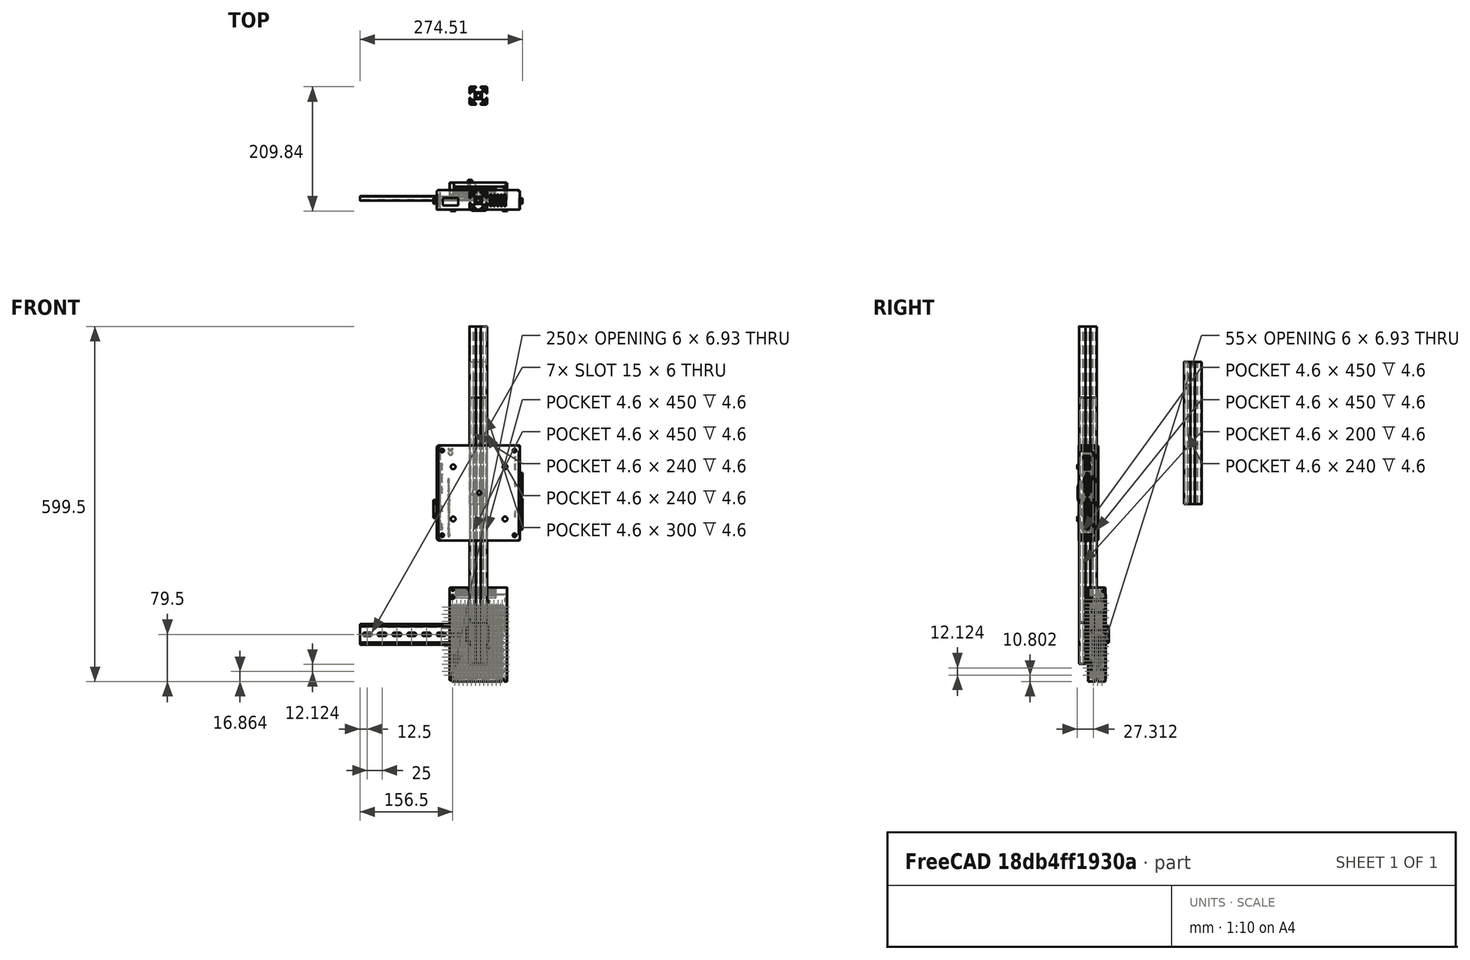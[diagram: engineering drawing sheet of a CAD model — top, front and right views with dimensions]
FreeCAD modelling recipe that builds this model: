
FCSTD DOCUMENT  (FreeCAD 1.0R39319 (Git))
Label: electronics-box
License: All rights reserved
objects: App::Link×40, App::FeaturePython×40, Part::Feature×11, App::Part×1, Assembly::JointGroup×1, Assembly::AssemblyObject×1
note: 11 computed .brp shape members not serialized (recipe doc carries the construction recipe); baked Part::Feature solids carry a one-line shape summary decoded from their .brp
EXTERNAL_REF file=din_mount.FCStd obj=Part
EXTERNAL_REF file=power-supply-bracket.FCStd obj=Part
EXTERNAL_REF file=dlp-power-supply-bracket.FCStd obj=Part
EXTERNAL_REF file=smc100c-bracket.FCStd obj=Part
EXTERNAL_REF file=ports-panel.FCStd obj=Part

FEATURE [Part::Feature] Part__Feature  label="alu-prof-3030-200-000"
  shape: bbox 30 x 30 x 200 mm, 122 faces (baked)
FEATURE [Part::Feature] Part__Feature001  label="alu-prof-3030-300-000"
  shape: bbox 30 x 30 x 300 mm, 122 faces (baked)
FEATURE [Part::Feature] Part__Feature002  label="alu-prof-3030-450-000"
  shape: bbox 30 x 30 x 450 mm, 122 faces (baked)
FEATURE [App::Link] alu_prof_3030_300_000  label="alu-prof-3030-300-001"
  LinkedObject = -> Part__Feature001
FEATURE [App::Link] alu_prof_3030_450_000  label="alu-prof-3030-450-001"
  LinkPlacement = pos=(415,-2.4e-15,235) rot=(0,-1,0;1.5708rad)
  LinkedObject = -> Part__Feature002
  Placement = pos=(415,-2.4e-15,235) rot=(0,-1,0;1.5708rad)
FEATURE [App::FeaturePython] GroundedJoint  # Assembly grounded joint (typed FeaturePython)
  ObjectToGround = -> alu_prof_3030_300_000
FEATURE [App::FeaturePython] Joint  label="Fixed"  # Assembly joint (typed FeaturePython)
  Activated = true
  AngleMax = 0
  AngleMin = 0
  Detach1 = false
  Detach2 = false
  Distance = 0
  Distance2 = 0
  EnableAngleMax = false
  EnableAngleMin = false
  EnableLengthMax = false
  EnableLengthMin = false
  JointType = 0 (Fixed)
  LengthMax = 0
  LengthMin = 0
  Offset2 = pos=(0,0,0) rot=(0,0,-1;1.5708rad)
  Placement1 = pos=(-15,-8.7,400) rot=(0.57735,0.57735,0.57735;4.18879rad)
  Placement2 = pos=(15,-8.7,220) rot=(0,0.707107,0.707107;3.14159rad)
  Reference1 = -> Assembly [alu_prof_3030_450_000.Edge78,alu_prof_3030_450_000.Edge78]
  Reference2 = -> Assembly [alu_prof_3030_300_000.Edge7,alu_prof_3030_300_000.Edge7]
FEATURE [App::Link] alu_prof_3030_300_001  label="alu-prof-3030-300-002"
  LinkPlacement = pos=(480,-1.166e-13,740) rot=(0,1,0;3.14159rad)
  LinkedObject = -> Part__Feature001
  Placement = pos=(480,-1.166e-13,740) rot=(0,1,0;3.14159rad)
FEATURE [App::Link] alu_prof_3030_200_000  label="alu-prof-3030-200-001"
  LinkPlacement = pos=(480,-235,505) rot=(1,0,0;4.71239rad)
  LinkedObject = -> Part__Feature
  Placement = pos=(480,-235,505) rot=(1,0,0;4.71239rad)
FEATURE [App::Link] alu_prof_3030_200_001  label="alu-prof-3030-200-002"
  LinkPlacement = pos=(9.88e-14,-235,505) rot=(-1,0,0;1.5708rad)
  LinkedObject = -> Part__Feature
  Placement = pos=(9.88e-14,-235,505) rot=(-1,0,0;1.5708rad)
FEATURE [App::Link] alu_prof_3030_200_002  label="alu-prof-3030-200-003"
  LinkPlacement = pos=(-9.59e-14,-235,235) rot=(1,0,0;4.71239rad)
  LinkedObject = -> Part__Feature
  Placement = pos=(-9.59e-14,-235,235) rot=(1,0,0;4.71239rad)
FEATURE [App::Link] alu_prof_3030_200_003  label="alu-prof-3030-200-004"
  LinkPlacement = pos=(480,-235,235) rot=(-1,0,0;1.5708rad)
  LinkedObject = -> Part__Feature
  Placement = pos=(480,-235,235) rot=(-1,0,0;1.5708rad)
FEATURE [App::FeaturePython] Joint001  label="Fixed001"  # Assembly joint (typed FeaturePython)
  Activated = true
  AngleMax = 0
  AngleMin = 0
  Detach1 = false
  Detach2 = false
  Distance = 0
  Distance2 = 0
  EnableAngleMax = false
  EnableAngleMin = false
  EnableLengthMax = false
  EnableLengthMin = false
  JointType = 0 (Fixed)
  LengthMax = 0
  LengthMin = 0
  Offset2 = pos=(0,0,0) rot=(0,0,-1;1.5708rad)
  Placement1 = pos=(15,-8.7,520) rot=(0.57735,0.57735,0.57735;4.18879rad)
  Placement2 = pos=(-15,-8.7,-50) rot=(0,-0.707107,0.707107;3.14159rad)
  Reference1 = -> Assembly [alu_prof_3030_300_001.Edge5,alu_prof_3030_300_001.Edge5]
  Reference2 = -> Assembly [alu_prof_3030_450_000.Edge153,alu_prof_3030_450_000.Edge153]
FEATURE [App::FeaturePython] Joint002  label="Fixed002"  # Assembly joint (typed FeaturePython)
  Activated = true
  AngleMax = 0
  AngleMin = 0
  Detach1 = false
  Detach2 = false
  Distance = 0
  Distance2 = 0
  EnableAngleMax = false
  EnableAngleMin = false
  EnableLengthMax = false
  EnableLengthMin = false
  JointType = 0 (Fixed)
  LengthMax = 0
  LengthMin = 0
  Offset2 = pos=(0,0,0) rot=(0,0,1;1.5708rad)
  Placement1 = pos=(-8.7,15,220) rot=(-0.707107,0,0.707107;3.14159rad)
  Placement2 = pos=(-8.7,-15,220) rot=(0.57735,-0.57735,0.57735;4.18879rad)
  Reference1 = -> Assembly [alu_prof_3030_200_002.Edge133,alu_prof_3030_200_002.Edge133]
  Reference2 = -> Assembly [alu_prof_3030_300_000.Edge205,alu_prof_3030_300_000.Edge205]
FEATURE [App::FeaturePython] Joint003  label="Fixed003"  # Assembly joint (typed FeaturePython)
  Activated = true
  AngleMax = 0
  AngleMin = 0
  Detach1 = false
  Detach2 = false
  Distance = 0
  Distance2 = 0
  EnableAngleMax = false
  EnableAngleMin = false
  EnableLengthMax = false
  EnableLengthMin = false
  JointType = 0 (Fixed)
  LengthMax = 0
  LengthMin = 0
  Offset2 = pos=(0,0,0) rot=(0,0,1;1.5708rad)
  Placement1 = pos=(-8.7,15,220) rot=(-0.707107,0,0.707107;3.14159rad)
  Placement2 = pos=(8.7,-15,520) rot=(0.57735,-0.57735,0.57735;4.18879rad)
  Reference1 = -> Assembly [alu_prof_3030_200_003.Edge133,alu_prof_3030_200_003.Edge133]
  Reference2 = -> Assembly [alu_prof_3030_300_001.Edge263,alu_prof_3030_300_001.Edge263]
FEATURE [App::FeaturePython] Joint004  label="Fixed004"  # Assembly joint (typed FeaturePython)
  Activated = true
  AngleMax = 0
  AngleMin = 0
  Detach1 = false
  Detach2 = false
  Distance = 0
  Distance2 = 0
  EnableAngleMax = false
  EnableAngleMin = false
  EnableLengthMax = false
  EnableLengthMin = false
  JointType = 0 (Fixed)
  LengthMax = 0
  LengthMin = 0
  Offset2 = pos=(0,0,0) rot=(0,0,-1;1.5708rad)
  Placement1 = pos=(-8.7,-15,220) rot=(0.707107,0,0.707107;3.14159rad)
  Placement2 = pos=(-8.7,-15,520) rot=(0.57735,0.57735,0.57735;2.0944rad)
  Reference1 = -> Assembly [alu_prof_3030_200_001.Edge205,alu_prof_3030_200_001.Edge205]
  Reference2 = -> Assembly [alu_prof_3030_300_000.Edge203,alu_prof_3030_300_000.Edge203]
FEATURE [App::FeaturePython] Joint005  label="Fixed005"  # Assembly joint (typed FeaturePython)
  Activated = true
  AngleMax = 0
  AngleMin = 0
  Detach1 = false
  Detach2 = false
  Distance = 0
  Distance2 = 0
  EnableAngleMax = false
  EnableAngleMin = false
  EnableLengthMax = false
  EnableLengthMin = false
  JointType = 0 (Fixed)
  LengthMax = 0
  LengthMin = 0
  Offset2 = pos=(0,0,0) rot=(0,0,-1;1.5708rad)
  Placement1 = pos=(-8.7,-15,220) rot=(0.707107,0,0.707107;3.14159rad)
  Placement2 = pos=(8.7,-15,220) rot=(0.57735,0.57735,0.57735;2.0944rad)
  Reference1 = -> Assembly [alu_prof_3030_200_000.Edge205,alu_prof_3030_200_000.Edge205]
  Reference2 = -> Assembly [alu_prof_3030_300_001.Edge264,alu_prof_3030_300_001.Edge264]
FEATURE [App::Link] alu_prof_3030_450_003  label="alu-prof-3030-450-004"
  LinkPlacement = pos=(415,-2e-15,505) rot=(0,1,0;4.71239rad)
  LinkedObject = -> Part__Feature002
  Placement = pos=(415,-2e-15,505) rot=(0,1,0;4.71239rad)
FEATURE [App::FeaturePython] Joint010  label="Fixed010"  # Assembly joint (typed FeaturePython)
  Activated = true
  AngleMax = 0
  AngleMin = 0
  Detach1 = false
  Detach2 = false
  Distance = 0
  Distance2 = 0
  EnableAngleMax = false
  EnableAngleMin = false
  EnableLengthMax = false
  EnableLengthMin = false
  JointType = 0 (Fixed)
  LengthMax = 0
  LengthMin = 0
  Offset2 = pos=(0,0,0) rot=(0,0,1;1.5708rad)
  Placement1 = pos=(15,-8.7,400) rot=(-0.57735,-0.57735,0.57735;4.18879rad)
  Placement2 = pos=(15,-8.7,520) rot=(1,0,0;4.71239rad)
  Reference1 = -> Assembly [alu_prof_3030_450_003.Edge14,alu_prof_3030_450_003.Edge14]
  Reference2 = -> Assembly [alu_prof_3030_300_000.Edge5,alu_prof_3030_300_000.Edge5]
FEATURE [Part::Feature] Part__Feature003  label="3030-angle-bracket-000"
  shape: bbox 36.72 x 36.72 x 28 mm, 72 faces (baked)
FEATURE [Part::Feature] Part__Feature004  label="SMC100CC"
  shape: bbox 150.5 x 35.5 x 163 mm, 2390 faces (baked)
FEATURE [Part::Feature] Part__Feature005  label="alu-prof-3030-240-000"
  Placement = pos=(0,177,0) rot=(0,0,1;0rad)
  shape: bbox 30 x 30 x 240 mm, 122 faces (baked)
FEATURE [App::Link] _030_angle_bracket_000  label="3030-angle-bracket-001"
  LinkPlacement = pos=(0.3,-197.5,250) rot=(-0.57735,-0.57735,-0.57735;4.18879rad)
  LinkedObject = -> Part__Feature003
  Placement = pos=(0.3,-197.5,250) rot=(-0.57735,-0.57735,-0.57735;4.18879rad)
FEATURE [App::Link] _030_angle_bracket_001  label="3030-angle-bracket-002"
  LinkPlacement = pos=(32.5,-15,505) rot=(1,0,0;3.14159rad)
  LinkedObject = -> Part__Feature003
  Placement = pos=(32.5,-15,505) rot=(1,0,0;3.14159rad)
FEATURE [App::Link] _030_angle_bracket_002  label="3030-angle-bracket-003"
  LinkPlacement = pos=(0.1,-15,267.5) rot=(0.707107,0,0.707107;3.14159rad)
  LinkedObject = -> Part__Feature003
  Placement = pos=(0.1,-15,267.5) rot=(0.707107,0,0.707107;3.14159rad)
FEATURE [App::Link] _030_angle_bracket_003  label="3030-angle-bracket-004"
  LinkPlacement = pos=(15,0.1,472.5) rot=(0.57735,0.57735,-0.57735;2.0944rad)
  LinkedObject = -> Part__Feature003
  Placement = pos=(15,0.1,472.5) rot=(0.57735,0.57735,-0.57735;2.0944rad)
FEATURE [App::Link] _030_angle_bracket_004  label="3030-angle-bracket-005"
  LinkPlacement = pos=(0.3,-215,472.5) rot=(0,-1,0;4.71239rad)
  LinkedObject = -> Part__Feature003
  Placement = pos=(0.3,-215,472.5) rot=(0,-1,0;4.71239rad)
FEATURE [App::Link] _030_angle_bracket_005  label="3030-angle-bracket-006"
  LinkPlacement = pos=(-0.3,-32.5,490) rot=(0.57735,-0.57735,0.57735;4.18879rad)
  LinkedObject = -> Part__Feature003
  Placement = pos=(-0.3,-32.5,490) rot=(0.57735,-0.57735,0.57735;4.18879rad)
FEATURE [App::FeaturePython] Joint013  label="Fixed013"  # Assembly joint (typed FeaturePython)
  Activated = true
  AngleMax = 0
  AngleMin = 0
  Detach1 = false
  Detach2 = false
  Distance = 0
  Distance2 = 0
  EnableAngleMax = false
  EnableAngleMin = false
  EnableLengthMax = false
  EnableLengthMin = false
  JointType = 0 (Fixed)
  LengthMax = 0
  LengthMin = 0
  Offset2 = pos=(0,0,13) rot=(0,0,1;1.5708rad)
  Placement1 = pos=(-17.5,0,0) rot=(0,0,1;0rad)
  Placement2 = pos=(15,0,220) rot=(1,0,0;4.71239rad)
  Reference1 = -> Assembly [_030_angle_bracket_001.Edge3,_030_angle_bracket_001.Edge3]
  Reference2 = -> Assembly [alu_prof_3030_200_001.Edge7,alu_prof_3030_200_001.Vertex4]
FEATURE [App::FeaturePython] Joint014  label="Fixed014"  # Assembly joint (typed FeaturePython)
  Activated = true
  AngleMax = 0
  AngleMin = 0
  Detach1 = false
  Detach2 = false
  Distance = 0
  Distance2 = 0
  EnableAngleMax = false
  EnableAngleMin = false
  EnableLengthMax = false
  EnableLengthMin = false
  JointType = 0 (Fixed)
  LengthMax = 0
  LengthMin = 0
  Offset2 = pos=(0,0,9) rot=(0,0,1;0rad)
  Placement1 = pos=(-17.5,0,3.4e-15) rot=(0,0,1;0rad)
  Placement2 = pos=(-0.3,15,220) rot=(-0.707107,0,0.707107;3.14159rad)
  Reference1 = -> Assembly [_030_angle_bracket_005.Edge3,_030_angle_bracket_005.Edge3]
  Reference2 = -> Assembly [alu_prof_3030_200_001.Edge73,alu_prof_3030_200_001.Edge73]
FEATURE [App::FeaturePython] Joint015  label="Fixed015"  # Assembly joint (typed FeaturePython)
  Activated = true
  AngleMax = 0
  AngleMin = 0
  Detach1 = false
  Detach2 = false
  Distance = 0
  Distance2 = 0
  EnableAngleMax = false
  EnableAngleMin = false
  EnableLengthMax = false
  EnableLengthMin = false
  JointType = 0 (Fixed)
  LengthMax = 0
  LengthMin = 0
  Offset2 = pos=(0,0,4.5) rot=(0,0,-1;1.5708rad)
  Placement1 = pos=(-17.5,1.8e-15,-3e-16) rot=(0,0,1;0rad)
  Placement2 = pos=(-15,0.1,400) rot=(0,0.707107,0.707107;3.14159rad)
  Reference1 = -> Assembly [_030_angle_bracket_003.Edge3,_030_angle_bracket_003.Edge3]
  Reference2 = -> Assembly [alu_prof_3030_450_003.Edge78,alu_prof_3030_450_003.Vertex78]
FEATURE [App::FeaturePython] Joint018  label="Fixed018"  # Assembly joint (typed FeaturePython)
  Activated = true
  AngleMax = 0
  AngleMin = 0
  Detach1 = false
  Detach2 = false
  Distance = 0
  Distance2 = 0
  EnableAngleMax = false
  EnableAngleMin = false
  EnableLengthMax = false
  EnableLengthMin = false
  JointType = 0 (Fixed)
  LengthMax = 0
  LengthMin = 0
  Offset2 = pos=(0,0,-4.5) rot=(0,0,-1;1.5708rad)
  Placement1 = pos=(-4.4,-15,220) rot=(0.707107,0,0.707107;3.14159rad)
  Placement2 = pos=(-17.5,0,-4.5) rot=(0,0,-1;1.5708rad)
  Reference1 = -> Assembly [alu_prof_3030_200_002.Edge205,alu_prof_3030_200_002.Vertex138]
  Reference2 = -> Assembly [_030_angle_bracket_002.Edge3,_030_angle_bracket_002.Edge3]
FEATURE [App::Link] _030_angle_bracket_006  label="3030-angle-bracket-007"
  LinkPlacement = pos=(447.5,-0.3,250) rot=(0,0.707107,0.707107;3.14159rad)
  LinkedObject = -> Part__Feature003
  Placement = pos=(447.5,-0.3,250) rot=(0,0.707107,0.707107;3.14159rad)
FEATURE [App::FeaturePython] Joint019  label="Fixed019"  # Assembly joint (typed FeaturePython)
  Activated = true
  AngleMax = 0
  AngleMin = 0
  Detach1 = false
  Detach2 = false
  Distance = 0
  Distance2 = 0
  EnableAngleMax = false
  EnableAngleMin = false
  EnableLengthMax = false
  EnableLengthMin = false
  JointType = 0 (Fixed)
  LengthMax = 0
  LengthMin = 0
  Offset2 = pos=(0,0,-9) rot=(0,0,1;0rad)
  Placement1 = pos=(-17.5,0,-4e-16) rot=(0,0,1;0rad)
  Placement2 = pos=(15,-0.3,-50) rot=(0.57735,0.57735,0.57735;4.18879rad)
  Reference1 = -> Assembly [_030_angle_bracket_006.Edge3,_030_angle_bracket_006.Edge3]
  Reference2 = -> Assembly [alu_prof_3030_450_000.Edge197,alu_prof_3030_450_000.Edge197]
FEATURE [App::Link] _030_angle_bracket_007  label="3030-angle-bracket-008"
  LinkPlacement = pos=(465,-1.3,472.5) rot=(-0.57735,0.57735,0.57735;2.0944rad)
  LinkedObject = -> Part__Feature003
  Placement = pos=(465,-1.3,472.5) rot=(-0.57735,0.57735,0.57735;2.0944rad)
FEATURE [App::FeaturePython] Joint020  label="Fixed020"  # Assembly joint (typed FeaturePython)
  Activated = true
  AngleMax = 0
  AngleMin = 0
  Detach1 = false
  Detach2 = false
  Distance = 0
  Distance2 = 0
  EnableAngleMax = false
  EnableAngleMin = false
  EnableLengthMax = false
  EnableLengthMin = false
  JointType = 0 (Fixed)
  LengthMax = 0
  LengthMin = 0
  Offset2 = pos=(0,0,-4) rot=(0,0,-1;1.5708rad)
  Placement1 = pos=(-17.5,0,14) rot=(0,0,1;0rad)
  Placement2 = pos=(-15,12.7,-50) rot=(0,-0.707107,0.707107;3.14159rad)
  Reference1 = -> Assembly [_030_angle_bracket_007.Edge3,_030_angle_bracket_007.Vertex3]
  Reference2 = -> Assembly [alu_prof_3030_450_003.Edge173,alu_prof_3030_450_003.Edge173]
FEATURE [App::Link] _030_angle_bracket_008  label="3030-angle-bracket-009"
  LinkPlacement = pos=(32.5,-15,234.7) rot=(-1,0,0;3.14159rad)
  LinkedObject = -> Part__Feature003
  Placement = pos=(32.5,-15,234.7) rot=(-1,0,0;3.14159rad)
FEATURE [App::Link] _030_angle_bracket_009  label="3030-angle-bracket-010"
  LinkPlacement = pos=(15,0.3,267.5) rot=(0.57735,0.57735,0.57735;4.18879rad)
  LinkedObject = -> Part__Feature003
  Placement = pos=(15,0.3,267.5) rot=(0.57735,0.57735,0.57735;4.18879rad)
FEATURE [App::Link] _030_angle_bracket_010  label="3030-angle-bracket-011"
  LinkPlacement = pos=(447.5,-15,235.3) rot=(0,0,1;3.14159rad)
  LinkedObject = -> Part__Feature003
  Placement = pos=(447.5,-15,235.3) rot=(0,0,1;3.14159rad)
FEATURE [App::FeaturePython] Joint021  label="Fixed021"  # Assembly joint (typed FeaturePython)
  Activated = true
  AngleMax = 0
  AngleMin = 0
  Detach1 = false
  Detach2 = false
  Distance = 0
  Distance2 = 0
  EnableAngleMax = false
  EnableAngleMin = false
  EnableLengthMax = false
  EnableLengthMin = false
  JointType = 0 (Fixed)
  LengthMax = 0
  LengthMin = 0
  Offset2 = pos=(0,0,9) rot=(0,0,1;1.5708rad)
  Placement1 = pos=(-17.5,0,0) rot=(0,0,1;0rad)
  Placement2 = pos=(15,0.3,220) rot=(1,0,0;4.71239rad)
  Reference1 = -> Assembly [_030_angle_bracket_008.Edge3,_030_angle_bracket_008.Edge3]
  Reference2 = -> Assembly [alu_prof_3030_200_002.Edge7,alu_prof_3030_200_002.Edge7]
FEATURE [App::FeaturePython] Joint022  label="Fixed022"  # Assembly joint (typed FeaturePython)
  Activated = true
  AngleMax = 0
  AngleMin = 0
  Detach1 = false
  Detach2 = false
  Distance = 0
  Distance2 = 0
  EnableAngleMax = false
  EnableAngleMin = false
  EnableLengthMax = false
  EnableLengthMin = false
  JointType = 0 (Fixed)
  LengthMax = 0
  LengthMin = 0
  Offset2 = pos=(0,0,-9) rot=(0,0,1;1.5708rad)
  Placement1 = pos=(-17.5,3.6e-15,-6e-16) rot=(0,0,1;0rad)
  Placement2 = pos=(15,0.3,400) rot=(-1,0,0;4.71239rad)
  Reference1 = -> Assembly [_030_angle_bracket_009.Edge3,_030_angle_bracket_009.Edge3]
  Reference2 = -> Assembly [alu_prof_3030_450_000.Edge14,alu_prof_3030_450_000.Edge14]
FEATURE [App::FeaturePython] Joint023  label="Fixed023"  # Assembly joint (typed FeaturePython)
  Activated = true
  AngleMax = 0
  AngleMin = 0
  Detach1 = false
  Detach2 = false
  Distance = 0
  Distance2 = 0
  EnableAngleMax = false
  EnableAngleMin = false
  EnableLengthMax = false
  EnableLengthMin = false
  JointType = 0 (Fixed)
  LengthMax = 0
  LengthMin = 0
  Offset2 = pos=(0,0,9) rot=(0,0,1;0rad)
  Placement1 = pos=(-17.5,0,0) rot=(0,0,1;0rad)
  Placement2 = pos=(0.3,-15,-50) rot=(0.707107,0,0.707107;3.14159rad)
  Reference1 = -> Assembly [_030_angle_bracket_010.Edge3,_030_angle_bracket_010.Edge3]
  Reference2 = -> Assembly [alu_prof_3030_450_000.Edge151,alu_prof_3030_450_000.Edge151]
FEATURE [App::Link] _030_angle_bracket_011  label="3030-angle-bracket-012"
  LinkPlacement = pos=(480.3,-15,267.5) rot=(0.707107,0,0.707107;3.14159rad)
  LinkedObject = -> Part__Feature003
  Placement = pos=(480.3,-15,267.5) rot=(0.707107,0,0.707107;3.14159rad)
FEATURE [App::Link] _030_angle_bracket_012  label="3030-angle-bracket-013"
  LinkPlacement = pos=(480.3,-197.5,250) rot=(0.57735,0.57735,0.57735;2.0944rad)
  LinkedObject = -> Part__Feature003
  Placement = pos=(480.3,-197.5,250) rot=(0.57735,0.57735,0.57735;2.0944rad)
FEATURE [App::Link] _030_angle_bracket_013  label="3030-angle-bracket-014"
  LinkPlacement = pos=(479.7,-215,472.5) rot=(0,1,0;1.5708rad)
  LinkedObject = -> Part__Feature003
  Placement = pos=(479.7,-215,472.5) rot=(0,1,0;1.5708rad)
FEATURE [App::FeaturePython] Joint024  label="Fixed024"  # Assembly joint (typed FeaturePython)
  Activated = true
  AngleMax = 0
  AngleMin = 0
  Detach1 = false
  Detach2 = false
  Distance = 0
  Distance2 = 0
  EnableAngleMax = false
  EnableAngleMin = false
  EnableLengthMax = false
  EnableLengthMin = false
  JointType = 0 (Fixed)
  LengthMax = 0
  LengthMin = 0
  Offset2 = pos=(0,0,9) rot=(0,0,1;1.5708rad)
  Placement1 = pos=(-17.5,-1.8e-15,0) rot=(0,0,1;0rad)
  Placement2 = pos=(0.3,-15,220) rot=(0.57735,-0.57735,0.57735;4.18879rad)
  Reference1 = -> Assembly [_030_angle_bracket_011.Edge3,_030_angle_bracket_011.Edge3]
  Reference2 = -> Assembly [alu_prof_3030_200_003.Edge205,alu_prof_3030_200_003.Edge205]
FEATURE [App::Link] _030_angle_bracket_014  label="3030-angle-bracket-015"
  LinkPlacement = pos=(480.3,-32.5,490) rot=(-0.57735,0.57735,-0.57735;2.0944rad)
  LinkedObject = -> Part__Feature003
  Placement = pos=(480.3,-32.5,490) rot=(-0.57735,0.57735,-0.57735;2.0944rad)
FEATURE [App::Link] _030_angle_bracket_015  label="3030-angle-bracket-016"
  LinkPlacement = pos=(447.5,-15,504.7) rot=(0,0,-1;3.14159rad)
  LinkedObject = -> Part__Feature003
  Placement = pos=(447.5,-15,504.7) rot=(0,0,-1;3.14159rad)
FEATURE [App::FeaturePython] Joint027  label="Fixed027"  # Assembly joint (typed FeaturePython)
  Activated = true
  AngleMax = 0
  AngleMin = 0
  Detach1 = false
  Detach2 = false
  Distance = 0
  Distance2 = 0
  EnableAngleMax = false
  EnableAngleMin = false
  EnableLengthMax = false
  EnableLengthMin = false
  JointType = 0 (Fixed)
  LengthMax = 0
  LengthMin = 0
  Offset2 = pos=(0,0,-9) rot=(0,0,1;0rad)
  Placement1 = pos=(-17.5,0,0) rot=(0,0,1;0rad)
  Placement2 = pos=(-0.3,-15,-50) rot=(0.707107,0,0.707107;3.14159rad)
  Reference1 = -> Assembly [_030_angle_bracket_015.Edge3,_030_angle_bracket_015.Edge3]
  Reference2 = -> Assembly [alu_prof_3030_450_003.Edge131,alu_prof_3030_450_003.Edge131]
FEATURE [App::FeaturePython] Joint028  label="Fixed028"  # Assembly joint (typed FeaturePython)
  Activated = true
  AngleMax = 0
  AngleMin = 0
  Detach1 = false
  Detach2 = false
  Distance = 0
  Distance2 = 0
  EnableAngleMax = false
  EnableAngleMin = false
  EnableLengthMax = false
  EnableLengthMin = false
  JointType = 0 (Fixed)
  LengthMax = 0
  LengthMin = 0
  Offset2 = pos=(0,0,-9) rot=(0,0,1;0rad)
  Placement1 = pos=(-17.5,0,0) rot=(0,0,1;0rad)
  Placement2 = pos=(0.3,15,220) rot=(-0.707107,0,0.707107;3.14159rad)
  Reference1 = -> Assembly [_030_angle_bracket_014.Edge3,_030_angle_bracket_014.Edge3]
  Reference2 = -> Assembly [alu_prof_3030_200_000.Edge133,alu_prof_3030_200_000.Edge133]
FEATURE [App::FeaturePython] Joint029  label="Fixed029"  # Assembly joint (typed FeaturePython)
  Activated = true
  AngleMax = 0
  AngleMin = 0
  Detach1 = false
  Detach2 = false
  Distance = 0
  Distance2 = 0
  EnableAngleMax = false
  EnableAngleMin = false
  EnableLengthMax = false
  EnableLengthMin = false
  JointType = 0 (Fixed)
  LengthMax = 0
  LengthMin = 0
  Offset2 = pos=(0,0,9) rot=(0,0,1;0rad)
  Placement1 = pos=(-17.5,-2.84e-14,1.2e-15) rot=(0,0,1;0rad)
  Placement2 = pos=(0.3,-15,20) rot=(0.707107,0,0.707107;3.14159rad)
  Reference1 = -> Assembly [_030_angle_bracket_000.Edge3,_030_angle_bracket_000.Edge3]
  Reference2 = -> Assembly [alu_prof_3030_200_002.Edge203,alu_prof_3030_200_002.Edge203]
FEATURE [App::FeaturePython] Joint030  label="Fixed030"  # Assembly joint (typed FeaturePython)
  Activated = true
  AngleMax = 0
  AngleMin = 0
  Detach1 = false
  Detach2 = false
  Distance = 0
  Distance2 = 0
  EnableAngleMax = false
  EnableAngleMin = false
  EnableLengthMax = false
  EnableLengthMin = false
  JointType = 0 (Fixed)
  LengthMax = 0
  LengthMin = 0
  Offset2 = pos=(0,0,5) rot=(0,0,-1;1.5708rad)
  Placement1 = pos=(-17.5,0,-14) rot=(0,0,1;0rad)
  Placement2 = pos=(-13.7,15,20) rot=(-0.57735,-0.57735,0.57735;2.0944rad)
  Reference1 = -> Assembly [_030_angle_bracket_004.Edge3,_030_angle_bracket_004.Vertex4]
  Reference2 = -> Assembly [alu_prof_3030_200_001.Edge131,alu_prof_3030_200_001.Edge131]
FEATURE [App::FeaturePython] Joint031  label="Fixed031"  # Assembly joint (typed FeaturePython)
  Activated = true
  AngleMax = 0
  AngleMin = 0
  Detach1 = false
  Detach2 = false
  Distance = 0
  Distance2 = 0
  EnableAngleMax = false
  EnableAngleMin = false
  EnableLengthMax = false
  EnableLengthMin = false
  JointType = 0 (Fixed)
  LengthMax = 0
  LengthMin = 0
  Offset2 = pos=(0,0,9) rot=(0,0,1;0rad)
  Placement1 = pos=(-17.5,0,0) rot=(0,0,1;0rad)
  Placement2 = pos=(0.3,-15,20) rot=(0.707107,0,0.707107;3.14159rad)
  Reference1 = -> Assembly [_030_angle_bracket_012.Edge3,_030_angle_bracket_012.Edge3]
  Reference2 = -> Assembly [alu_prof_3030_200_003.Edge203,alu_prof_3030_200_003.Edge203]
FEATURE [App::FeaturePython] Joint032  label="Fixed032"  # Assembly joint (typed FeaturePython)
  Activated = true
  AngleMax = 0
  AngleMin = 0
  Detach1 = false
  Detach2 = false
  Distance = 0
  Distance2 = 0
  EnableAngleMax = false
  EnableAngleMin = false
  EnableLengthMax = false
  EnableLengthMin = false
  JointType = 0 (Fixed)
  LengthMax = 0
  LengthMin = 0
  Offset2 = pos=(0,0,9) rot=(0,0,-1;1.5708rad)
  Placement1 = pos=(-17.5,0,0) rot=(0,0,1;0rad)
  Placement2 = pos=(-0.3,15,20) rot=(-0.57735,-0.57735,0.57735;2.0944rad)
  Reference1 = -> Assembly [_030_angle_bracket_013.Edge3,_030_angle_bracket_013.Edge3]
  Reference2 = -> Assembly [alu_prof_3030_200_000.Edge71,alu_prof_3030_200_000.Edge71]
FEATURE [App::Link] din_mount_part
  LinkPlacement = pos=(480,-79,490) rot=(0.707107,-0.707107,0;3.14159rad)
  LinkedObject = -> <external din_mount.FCStd>#Part
  Placement = pos=(480,-79,490) rot=(0.707107,-0.707107,0;3.14159rad)
FEATURE [App::Link] din_mount_part001
  LinkPlacement = pos=(480,-140,490) rot=(0.707107,-0.707107,0;3.14159rad)
  LinkedObject = -> <external din_mount.FCStd>#Part
  Placement = pos=(480,-140,490) rot=(0.707107,-0.707107,0;3.14159rad)
FEATURE [App::FeaturePython] Joint033  label="Fixed033"  # Assembly joint (typed FeaturePython)
  Activated = true
  AngleMax = 0
  AngleMin = 0
  Detach1 = false
  Detach2 = false
  Distance = 0
  Distance2 = 0
  EnableAngleMax = false
  EnableAngleMin = false
  EnableLengthMax = false
  EnableLengthMin = false
  JointType = 0 (Fixed)
  LengthMax = 0
  LengthMin = 0
  Offset2 = pos=(2,0,-36) rot=(0,0,-1;1.5708rad)
  Placement1 = pos=(0,15,0) rot=(-0.707107,0,0.707107;3.14159rad)
  Placement2 = pos=(-15,15,156) rot=(-0.707107,0.707107,0;3.14159rad)
  Reference1 = -> Assembly [din_mount_part.Body.Edge27,din_mount_part.Body.Edge27]
  Reference2 = -> Assembly [alu_prof_3030_200_000.Edge132,alu_prof_3030_200_000.Edge132]
FEATURE [Part::Feature] Part__Feature006  label="din_rail_180mm"
  shape: bbox 180 x 7.5 x 35 mm, 50 faces (baked)
FEATURE [App::Link] din_rail_180mm  label="din_rail_180mm001"
  LinkPlacement = pos=(465,3,437.5) rot=(0,0,-1;4.71239rad)
  LinkedObject = -> Part__Feature006
  Placement = pos=(465,3,437.5) rot=(0,0,-1;4.71239rad)
FEATURE [App::FeaturePython] Joint034  label="Fixed034"  # Assembly joint (typed FeaturePython)
  Activated = true
  AngleMax = 0
  AngleMin = 0
  Detach1 = false
  Detach2 = false
  Distance = 0
  Distance2 = 0
  EnableAngleMax = false
  EnableAngleMin = false
  EnableLengthMax = false
  EnableLengthMin = false
  JointType = 0 (Fixed)
  LengthMax = 0
  LengthMin = 0
  Offset1 = pos=(-7,0,0) rot=(0,0,1;0rad)
  Placement1 = pos=(-32,-7.92893,2.5) rot=(0,0,1;0rad)
  Placement2 = pos=(25,-7.92893,2.5) rot=(0,0,1;0rad)
  Reference1 = -> Assembly [din_mount_part001.Body.Edge37,din_mount_part001.Body.Edge37]
  Reference2 = -> Assembly [din_mount_part.Body.Edge47,din_mount_part.Body.Edge47]
FEATURE [App::FeaturePython] Joint035  label="Fixed035"  # Assembly joint (typed FeaturePython)
  Activated = true
  AngleMax = 0
  AngleMin = 0
  Detach1 = false
  Detach2 = false
  Distance = 0
  Distance2 = 0
  EnableAngleMax = false
  EnableAngleMin = false
  EnableLengthMax = false
  EnableLengthMin = false
  JointType = 0 (Fixed)
  LengthMax = 0
  LengthMin = 0
  Offset1 = pos=(0,-49,0) rot=(0,0,1;0rad)
  Offset2 = pos=(0,0,0) rot=(0,0,1;1.5708rad)
  Placement1 = pos=(-82,-8.2e-15,1.733e-13) rot=(-0.57735,-0.57735,0.57735;4.18879rad)
  Placement2 = pos=(0,15,52.5) rot=(0.57735,0.57735,0.57735;4.18879rad)
  Reference1 = -> Assembly [din_rail_180mm.Edge62,din_rail_180mm.Edge62]
  Reference2 = -> Assembly [din_mount_part.Body.Edge30,din_mount_part.Body.Edge30]
FEATURE [App::Link] alu_prof_3030_450_004  label="alu-prof-3030-450-005"
  LinkPlacement = pos=(65,-5.3e-15,415) rot=(0,-1,0;4.71239rad)
  LinkedObject = -> Part__Feature002
  Placement = pos=(65,-5.3e-15,415) rot=(0,-1,0;4.71239rad)
FEATURE [App::Link] _030_angle_bracket_016  label="3030-angle-bracket-017"
  LinkPlacement = pos=(32.5,-0.2,400) rot=(-1,0,0;1.5708rad)
  LinkedObject = -> Part__Feature003
  Placement = pos=(32.5,-0.2,400) rot=(-1,0,0;1.5708rad)
FEATURE [App::Link] _030_angle_bracket_017  label="3030-angle-bracket-018"
  LinkPlacement = pos=(447.5,-0.3,400) rot=(0,0.707107,-0.707107;3.14159rad)
  LinkedObject = -> Part__Feature003
  Placement = pos=(447.5,-0.3,400) rot=(0,0.707107,-0.707107;3.14159rad)
FEATURE [App::FeaturePython] Joint036  label="Fixed036"  # Assembly joint (typed FeaturePython)
  Activated = true
  AngleMax = 0
  AngleMin = 0
  Detach1 = false
  Detach2 = false
  Distance = 0
  Distance2 = 0
  EnableAngleMax = false
  EnableAngleMin = false
  EnableLengthMax = false
  EnableLengthMin = false
  JointType = 0 (Fixed)
  LengthMax = 0
  LengthMin = 0
  Offset1 = pos=(0,-90,0) rot=(0,0,1;0rad)
  Offset2 = pos=(0,0,0) rot=(0,0,1;3.14159rad)
  Placement1 = pos=(-105,8.7,400) rot=(0.57735,0.57735,0.57735;4.18879rad)
  Placement2 = pos=(15,8.7,-50) rot=(0.57735,-0.57735,-0.57735;4.18879rad)
  Reference1 = -> Assembly [alu_prof_3030_450_004.Edge58,alu_prof_3030_450_004.Edge58]
  Reference2 = -> Assembly [alu_prof_3030_450_003.Edge197,alu_prof_3030_450_003.Edge197]
FEATURE [App::FeaturePython] Joint037  label="Fixed037"  # Assembly joint (typed FeaturePython)
  Activated = true
  AngleMax = 0
  AngleMin = 0
  Detach1 = false
  Detach2 = false
  Distance = 0
  Distance2 = 0
  EnableAngleMax = false
  EnableAngleMin = false
  EnableLengthMax = false
  EnableLengthMin = false
  JointType = 0 (Fixed)
  LengthMax = 0
  LengthMin = 0
  Offset2 = pos=(0,0,22.5) rot=(0,0,1;0rad)
  Placement1 = pos=(-17.5,0,14) rot=(0,0,1;0rad)
  Placement2 = pos=(15,13.8,-50) rot=(0.57735,0.57735,0.57735;4.18879rad)
  Reference1 = -> Assembly [_030_angle_bracket_016.Edge3,_030_angle_bracket_016.Vertex3]
  Reference2 = -> Assembly [alu_prof_3030_450_004.Edge217,alu_prof_3030_450_004.Edge217]
FEATURE [App::FeaturePython] Joint038  label="Fixed038"  # Assembly joint (typed FeaturePython)
  Activated = true
  AngleMax = 0
  AngleMin = 0
  Detach1 = false
  Detach2 = false
  Distance = 0
  Distance2 = 0
  EnableAngleMax = false
  EnableAngleMin = false
  EnableLengthMax = false
  EnableLengthMin = false
  JointType = 0 (Fixed)
  LengthMax = 0
  LengthMin = 0
  Offset2 = pos=(0,0,9) rot=(0,0,1;0rad)
  Placement1 = pos=(-17.5,0,-6e-16) rot=(0,0,1;0rad)
  Placement2 = pos=(15,-0.3,400) rot=(-0.57735,-0.57735,0.57735;4.18879rad)
  Reference1 = -> Assembly [_030_angle_bracket_017.Edge3,_030_angle_bracket_017.Edge3]
  Reference2 = -> Assembly [alu_prof_3030_450_004.Edge34,alu_prof_3030_450_004.Edge34]
FEATURE [App::Link] power_supply_bracket_part  label="power-supply-bracket-part"
  LinkPlacement = pos=(283,15,400) rot=(0.57735,-0.57735,-0.57735;2.0944rad)
  LinkedObject = -> <external power-supply-bracket.FCStd>#Part
  Placement = pos=(283,15,400) rot=(0.57735,-0.57735,-0.57735;2.0944rad)
FEATURE [App::Link] power_supply_bracket_part001  label="power-supply-bracket-part001"
  LinkPlacement = pos=(347,15,400) rot=(0.57735,-0.57735,-0.57735;2.0944rad)
  LinkedObject = -> <external power-supply-bracket.FCStd>#Part
  Placement = pos=(347,15,400) rot=(0.57735,-0.57735,-0.57735;2.0944rad)
FEATURE [App::FeaturePython] Joint039  label="Fixed039"  # Assembly joint (typed FeaturePython)
  Activated = true
  AngleMax = 0
  AngleMin = 0
  Detach1 = false
  Detach2 = false
  Distance = 0
  Distance2 = 0
  EnableAngleMax = false
  EnableAngleMin = false
  EnableLengthMax = false
  EnableLengthMin = false
  JointType = 0 (Fixed)
  LengthMax = 0
  LengthMin = 0
  Offset2 = pos=(0,2,-120) rot=(0,0,-1;1.5708rad)
  Placement1 = pos=(0,30,-13) rot=(0,0,1;0rad)
  Placement2 = pos=(-15,15,295) rot=(-0.707107,0.707107,0;3.14159rad)
  Reference1 = -> Assembly [power_supply_bracket_part001.Body.Edge82,power_supply_bracket_part001.Body.Edge82]
  Reference2 = -> Assembly [alu_prof_3030_450_004.Edge292,alu_prof_3030_450_004.Edge292]
FEATURE [App::FeaturePython] Joint040  label="Fixed040"  # Assembly joint (typed FeaturePython)
  Activated = true
  AngleMax = 0
  AngleMin = 0
  Detach1 = false
  Detach2 = false
  Distance = 0
  Distance2 = 0
  EnableAngleMax = false
  EnableAngleMin = false
  EnableLengthMax = false
  EnableLengthMin = false
  JointType = 0 (Fixed)
  LengthMax = 0
  LengthMin = 0
  Offset2 = pos=(-30,0,0) rot=(0,0,1;0rad)
  Placement1 = pos=(15,30,-30) rot=(-0.707107,0,0.707107;3.14159rad)
  Placement2 = pos=(15,30,34) rot=(-0.707107,0,0.707107;3.14159rad)
  Reference1 = -> Assembly [power_supply_bracket_part.Body.Edge83,power_supply_bracket_part.Body.Edge83]
  Reference2 = -> Assembly [power_supply_bracket_part001.Body.Edge9,power_supply_bracket_part001.Body.Edge9]
FEATURE [Part::Feature] Part__Feature007  label="LRS-150"
  shape: bbox 97.19 x 29.5 x 159 mm, 315 faces (baked)
FEATURE [Part::Feature] Part__Feature008  label="LRS-151"
  shape: bbox 95.3 x 28.5 x 143 mm, 2203 faces (baked)
FEATURE [Part::Feature] Part__Feature009  label="LRS-152"
  shape: bbox 94.01 x 16.61 x 152.1 mm, 1017 faces (baked)
FEATURE [Part::Feature] Part__Feature010  label="LRS-153"
  shape: bbox 4.818 x 5.068 x 4.818 mm, 39 faces (baked)
FEATURE [App::Part] LRS_150  label="LRS-154"
  Group = -> [Part__Feature007,Part__Feature008,Part__Feature009,Part__Feature010]
  Origin = -> Origin002
FEATURE [App::Link] LRS_154  label="LRS-155"
  LinkPlacement = pos=(283,-104.5,414.75) rot=(-0.57735,-0.57735,0.57735;4.18879rad)
  LinkedObject = -> LRS_150
  Placement = pos=(283,-104.5,414.75) rot=(-0.57735,-0.57735,0.57735;4.18879rad)
FEATURE [App::Link] LRS_155  label="LRS-156"
  LinkPlacement = pos=(347,-103.25,414.75) rot=(-0.57735,-0.57735,0.57735;4.18879rad)
  LinkedObject = -> LRS_150
  Placement = pos=(347,-103.25,414.75) rot=(-0.57735,-0.57735,0.57735;4.18879rad)
FEATURE [App::FeaturePython] Joint041  label="Fixed041"  # Assembly joint (typed FeaturePython)
  Activated = true
  AngleMax = 0
  AngleMin = 0
  Detach1 = false
  Detach2 = false
  Distance = 0
  Distance2 = 0
  EnableAngleMax = false
  EnableAngleMin = false
  EnableLengthMax = false
  EnableLengthMin = false
  JointType = 0 (Fixed)
  LengthMax = 0
  LengthMin = 0
  Offset1 = pos=(0,0,0) rot=(0,1,0;0.785398rad)
  Placement1 = pos=(47.75,15,58.75) rot=(0,1,0;4.71239rad)
  Placement2 = pos=(177,-33,-15) rot=(-1,0,0;1.5708rad)
  Reference1 = -> Assembly [LRS_155.Part__Feature007.Edge487,LRS_155.Part__Feature007.Vertex360]
  Reference2 = -> Assembly [power_supply_bracket_part001.Body.Edge170,power_supply_bracket_part001.Body.Edge170]
FEATURE [App::FeaturePython] Joint042  label="Fixed042"  # Assembly joint (typed FeaturePython)
  Activated = true
  AngleMax = 0
  AngleMin = 0
  Detach1 = false
  Detach2 = false
  Distance = 0
  Distance2 = 0
  EnableAngleMax = false
  EnableAngleMin = false
  EnableLengthMax = false
  EnableLengthMin = false
  JointType = 0 (Fixed)
  LengthMax = 0
  LengthMin = 0
  Offset2 = pos=(0,0,0) rot=(0,0,1;3.14159rad)
  Placement1 = pos=(47.75,15,57.5) rot=(0,1,0;1.5708rad)
  Placement2 = pos=(177,-33,-15) rot=(0,0.707107,0.707107;3.14159rad)
  Reference1 = -> Assembly [LRS_154.Part__Feature007.Edge488,LRS_154.Part__Feature007.Edge488]
  Reference2 = -> Assembly [power_supply_bracket_part.Body.Edge170,power_supply_bracket_part.Body.Edge170]
FEATURE [App::Link] dlp_power_supply_bracket_part  label="dlp-power-supply-bracket-part"
  LinkPlacement = pos=(226,-36.5,425) rot=(0,0,1;0rad)
  LinkedObject = -> <external dlp-power-supply-bracket.FCStd>#Part
  Placement = pos=(226,-36.5,425) rot=(0,0,1;0rad)
FEATURE [App::FeaturePython] Joint043  label="Fixed043"  # Assembly joint (typed FeaturePython)
  Activated = true
  AngleMax = 0
  AngleMin = 0
  Detach1 = false
  Detach2 = false
  Distance = 0
  Distance2 = 0
  EnableAngleMax = false
  EnableAngleMin = false
  EnableLengthMax = false
  EnableLengthMin = false
  JointType = 0 (Fixed)
  LengthMax = 0
  LengthMin = 0
  Offset2 = pos=(0,0,-70) rot=(0,0,1;1.5708rad)
  Placement1 = pos=(0,21.5,5) rot=(0.707107,0,0.707107;3.14159rad)
  Placement2 = pos=(30,30,57) rot=(0.707107,0.707107,0;3.14159rad)
  Reference1 = -> Assembly [dlp_power_supply_bracket_part.Body.Edge15,dlp_power_supply_bracket_part.Body.Edge15]
  Reference2 = -> Assembly [power_supply_bracket_part.Body.Edge77,power_supply_bracket_part.Body.Edge77]
FEATURE [App::Link] smc100c_bracket_part  label="smc100c-bracket-part"
  LinkPlacement = pos=(171,-194,435) rot=(0,0,-1;4.71239rad)
  LinkedObject = -> <external smc100c-bracket.FCStd>#Part
  Placement = pos=(171,-194,435) rot=(0,0,-1;4.71239rad)
FEATURE [App::Link] smc100c_bracket_part001  label="smc100c-bracket-part001"
  LinkPlacement = pos=(116,-194,435) rot=(0,0,-1;4.71239rad)
  LinkedObject = -> <external smc100c-bracket.FCStd>#Part
  Placement = pos=(116,-194,435) rot=(0,0,-1;4.71239rad)
FEATURE [App::FeaturePython] Joint044  label="Fixed044"  # Assembly joint (typed FeaturePython)
  Activated = true
  AngleMax = 0
  AngleMin = 0
  Detach1 = false
  Detach2 = false
  Distance = 0
  Distance2 = 0
  EnableAngleMax = false
  EnableAngleMin = false
  EnableLengthMax = false
  EnableLengthMin = false
  JointType = 0 (Fixed)
  LengthMax = 0
  LengthMin = 0
  Offset2 = pos=(0,0,-140) rot=(0,0,1;1.5708rad)
  Placement1 = pos=(179,15,-5) rot=(0.57735,0.57735,0.57735;4.18879rad)
  Placement2 = pos=(30,30,127) rot=(0.707107,0.707107,0;3.14159rad)
  Reference1 = -> Assembly [smc100c_bracket_part.Body.Edge49,smc100c_bracket_part.Body.Edge49]
  Reference2 = -> Assembly [power_supply_bracket_part.Body.Edge77,power_supply_bracket_part.Body.Edge77]
FEATURE [App::FeaturePython] Joint045  label="Fixed045"  # Assembly joint (typed FeaturePython)
  Activated = true
  AngleMax = 0
  AngleMin = 0
  Detach1 = false
  Detach2 = false
  Distance = 0
  Distance2 = 0
  EnableAngleMax = false
  EnableAngleMin = false
  EnableLengthMax = false
  EnableLengthMin = false
  JointType = 0 (Fixed)
  LengthMax = 0
  LengthMin = 0
  Offset2 = pos=(0,0,40) rot=(0,0,1;0rad)
  Placement1 = pos=(179,15,-5) rot=(0.57735,0.57735,0.57735;4.18879rad)
  Placement2 = pos=(179,70,-5) rot=(0.57735,0.57735,0.57735;4.18879rad)
  Reference1 = -> Assembly [smc100c_bracket_part001.Body.Edge49,smc100c_bracket_part001.Body.Edge49]
  Reference2 = -> Assembly [smc100c_bracket_part.Body.Edge49,smc100c_bracket_part.Body.Vertex42]
FEATURE [App::Link] SMC100CC  label="SMC100CC001"
  LinkPlacement = pos=(92.7646,-343.5,357.708) rot=(-0.57735,0.57735,0.57735;2.0944rad)
  LinkedObject = -> Part__Feature004
  Placement = pos=(92.7646,-343.5,357.708) rot=(-0.57735,0.57735,0.57735;2.0944rad)
FEATURE [App::Link] SMC100CC001  label="SMC100CC002"
  LinkPlacement = pos=(147.765,-343.5,357.708) rot=(-0.57735,0.57735,0.57735;2.0944rad)
  LinkedObject = -> Part__Feature004
  Placement = pos=(147.765,-343.5,357.708) rot=(-0.57735,0.57735,0.57735;2.0944rad)
FEATURE [App::FeaturePython] Joint046  label="Fixed046"  # Assembly joint (typed FeaturePython)
  Activated = true
  AngleMax = 0
  AngleMin = 0
  Detach1 = false
  Detach2 = false
  Distance = 0
  Distance2 = 0
  EnableAngleMax = false
  EnableAngleMin = false
  EnableLengthMax = false
  EnableLengthMin = false
  JointType = 0 (Fixed)
  LengthMax = 0
  LengthMin = 0
  Offset2 = pos=(0,0,0) rot=(0,0,1;1.5708rad)
  Placement1 = pos=(1.70837,-17.2354,239) rot=(0,-0.707107,-0.707107;3.14159rad)
  Placement2 = pos=(89.5,6,-79) rot=(0.57735,-0.57735,0.57735;2.0944rad)
  Reference1 = -> Assembly [SMC100CC.Edge5281,SMC100CC.Edge5281]
  Reference2 = -> Assembly [smc100c_bracket_part001.Body.Edge20,smc100c_bracket_part001.Body.Edge20]
FEATURE [App::FeaturePython] Joint047  label="Fixed047"  # Assembly joint (typed FeaturePython)
  Activated = true
  AngleMax = 0
  AngleMin = 0
  Detach1 = false
  Detach2 = false
  Distance = 0
  Distance2 = 0
  EnableAngleMax = false
  EnableAngleMin = false
  EnableLengthMax = false
  EnableLengthMin = false
  JointType = 0 (Fixed)
  LengthMax = 0
  LengthMin = 0
  Offset2 = pos=(0,0,0) rot=(0,0,1;1.5708rad)
  Placement1 = pos=(1.70837,-17.2354,239) rot=(0,-0.707107,-0.707107;3.14159rad)
  Placement2 = pos=(89.5,6,-79) rot=(0.57735,-0.57735,0.57735;2.0944rad)
  Reference1 = -> Assembly [SMC100CC001.Edge5281,SMC100CC001.Edge5281]
  Reference2 = -> Assembly [smc100c_bracket_part.Body.Edge20,smc100c_bracket_part.Body.Edge20]
FEATURE [App::Link] ports_panel_part  label="ports-panel-part"
  LinkPlacement = pos=(501.2,-100,257.5) rot=(0.57735,-0.57735,-0.57735;2.0944rad)
  LinkedObject = -> <external ports-panel.FCStd>#Part
  Placement = pos=(501.2,-100,257.5) rot=(0.57735,-0.57735,-0.57735;2.0944rad)
FEATURE [App::FeaturePython] Joint048  label="Fixed048"  # Assembly joint (typed FeaturePython)
  Activated = true
  AngleMax = 0
  AngleMin = 0
  Detach1 = false
  Detach2 = false
  Distance = 0
  Distance2 = 0
  EnableAngleMax = false
  EnableAngleMin = false
  EnableLengthMax = false
  EnableLengthMin = false
  JointType = 0 (Fixed)
  LengthMax = 0
  LengthMin = 0
  Offset2 = pos=(0,0,-11.8) rot=(0,0,-1;1.5708rad)
  Placement1 = pos=(115,-2,6.2) rot=(0.57735,0.57735,0.57735;4.18879rad)
  Placement2 = pos=(15,-20.5,20) rot=(0,0.707107,0.707107;3.14159rad)
  Reference1 = -> Assembly [ports_panel_part.Body.Edge13,ports_panel_part.Body.Edge13]
  Reference2 = -> Assembly [alu_prof_3030_200_003.Edge5,alu_prof_3030_200_003.Edge5]
FEATURE [Assembly::JointGroup] Joints
  Group = -> [GroundedJoint,Joint,Joint001,Joint002,Joint003,Joint004,Joint005,Joint010,Joint013,Joint014,Joint015,Joint018,Joint019,Joint020,Joint021,Joint022,Joint023,Joint024,Joint027,Joint028,Joint029,Joint030,Joint031,Joint032,Joint033,Joint034,Joint035,Joint036,Joint037,Joint038,Joint039,Joint040,Joint041,Joint042,Joint043,Joint044,Joint045,Joint046,Joint047,Joint048]
FEATURE [Assembly::AssemblyObject] Assembly  label="electronics-box-assembly"
  Group = -> [Joints,alu_prof_3030_300_000,alu_prof_3030_450_000,GroundedJoint,Joint,alu_prof_3030_300_001,alu_prof_3030_200_000,alu_prof_3030_200_001,alu_prof_3030_200_002,alu_prof_3030_200_003,Joint001,Joint002,Joint003,Joint004,Joint005,alu_prof_3030_450_003,Joint010,_030_angle_bracket_000,_030_angle_bracket_001,_030_angle_bracket_002,_030_angle_bracket_003,_030_angle_bracket_004,_030_angle_bracket_005,+58 more]
  Origin = -> Origin
  Type = Assembly

RESOLVED EXTERNAL PARTS (link-assembly join: the EXTERNAL_REF files above that resolve inside this repo's crawl, each included once):
---- part din_mount.FCStd = doc fcstd_307fd711d50f ----
FCSTD DOCUMENT  (FreeCAD 1.0R39285 (Git))
Label: din_mount
License: All rights reserved
objects: Sketcher::SketchObject×4, PartDesign::Pad×2, PartDesign::Pocket×2, PartDesign::Chamfer×1, PartDesign::Body×1, App::Part×1
note: 24 computed .brp shape members not serialized (recipe doc carries the construction recipe); baked Part::Feature solids carry a one-line shape summary decoded from their .brp

FEATURE [Sketcher::SketchObject] Sketch
  ArcFitTolerance = 1e-06
  AttachmentSupport = -> [XY_Plane]
  FullyConstrained = true
  MakeInternals = false
  MapMode = 5
  expr: Constraints[33] = 10
  sketch-geometry (17):
    g0: LineSegment StartX=-17.9289 StartY=-15 StartZ=0 EndX=17.9289 EndY=-15 EndZ=0
    g1: LineSegment StartX=25 StartY=-7.92893 StartZ=0 EndX=25 EndY=7.92893 EndZ=0
    g2: LineSegment StartX=17.9289 StartY=15 StartZ=0 EndX=-17.9289 EndY=15 EndZ=0
    g3: LineSegment StartX=-25 StartY=7.92893 StartZ=0 EndX=-25 EndY=-7.92893 EndZ=0
    g4: GeomPoint [constr] X=0 Y=0 Z=0
    g5: ArcOfCircle [constr] CenterX=-17.9289 CenterY=7.92893 CenterZ=0 NormalX=0 NormalY=0 NormalZ=1 AngleXU=0 Radius=7.07107 StartAngle=1.5708 EndAngle=3.14159
    g6: GeomPoint [constr] X=-25 Y=15 Z=0
    g7: LineSegment StartX=-17.9289 StartY=15 StartZ=0 EndX=-25 EndY=7.92893 EndZ=0
    g8: ArcOfCircle [constr] CenterX=17.9289 CenterY=7.92893 CenterZ=0 NormalX=0 NormalY=0 NormalZ=1 AngleXU=0 Radius=7.07107 StartAngle=1e-16 EndAngle=1.5708
    g9: GeomPoint [constr] X=25 Y=15 Z=0
    g10: LineSegment StartX=25 StartY=7.92893 StartZ=0 EndX=17.9289 EndY=15 EndZ=0
    g11: ArcOfCircle [constr] CenterX=17.9289 CenterY=-7.92893 CenterZ=0 NormalX=0 NormalY=0 NormalZ=1 AngleXU=0 Radius=7.07107 StartAngle=4.71239 EndAngle=6.28319
    g12: GeomPoint [constr] X=25 Y=-15 Z=0
    g13: LineSegment StartX=17.9289 StartY=-15 StartZ=0 EndX=25 EndY=-7.92893 EndZ=0
    g14: ArcOfCircle [constr] CenterX=-17.9289 CenterY=-7.92893 CenterZ=0 NormalX=0 NormalY=0 NormalZ=1 AngleXU=0 Radius=7.07107 StartAngle=3.14159 EndAngle=4.71239
    g15: GeomPoint [constr] X=-25 Y=-15 Z=0
    g16: LineSegment StartX=-25 StartY=-7.92893 StartZ=0 EndX=-17.9289 EndY=-15 EndZ=0
  constraints (36):
    c: Horizontal(g0)
    c: Horizontal(g2)
    c: Vertical(g1)
    c: Vertical(g3)
    c: Symmetric(g9,g15,g4)
    c: Distance(g12,g15) = 50
    c: Distance(g15,g6) = 30
    c: Coincident(g4,g-1)
    c: PointOnObject(g6,g2)
    c: PointOnObject(g6,g3)
    c: Tangent(g2,g5) = -1.5708
    c: Tangent(g3,g5) = -1.5708
    c: Coincident(g7,g2)
    c: Coincident(g7,g3)
    c: PointOnObject(g9,g2)
    c: PointOnObject(g9,g1)
    c: Tangent(g2,g8) = -1.5708
    c: Tangent(g1,g8) = -1.5708
    c: Coincident(g10,g2)
    c: Coincident(g10,g1)
    c: PointOnObject(g12,g0)
    c: PointOnObject(g12,g1)
    c: Tangent(g0,g11) = -1.5708
    c: Tangent(g1,g11) = -1.5708
    c: Coincident(g13,g0)
    c: Coincident(g13,g1)
    c: PointOnObject(g15,g3)
    c: PointOnObject(g15,g0)
    c: Tangent(g3,g14) = -1.5708
    c: Tangent(g0,g14) = -1.5708
    c: Coincident(g16,g3)
    c: Coincident(g16,g0)
    c: Distance(g7,g7) = 10
    c: Distance(g10,g10) = 10
    c: Distance(g13,g13) = 10
    c: Distance(g16,g16) = 10
FEATURE [PartDesign::Pad] Pad
  Direction = (0,0,1)
  Length = 5
  Length2 = 10
  Profile = -> Sketch
  ReferenceAxis = -> Sketch [N_Axis]
  Refine = true
  Suppressed = false
  Type = 0
FEATURE [Sketcher::SketchObject] Sketch001
  ArcFitTolerance = 1e-06
  AttachmentSupport = -> [YZ_Plane]
  FullyConstrained = true
  MakeInternals = false
  MapMode = 5
  Placement = pos=(0,0,0) rot=(0.57735,0.57735,0.57735;2.0944rad)
  sketch-geometry (6):
    g0: LineSegment StartX=0 StartY=0 StartZ=0 EndX=-10 EndY=0 EndZ=0
    g1: LineSegment StartX=-10 StartY=0 StartZ=0 EndX=-10 EndY=15 EndZ=0
    g2: LineSegment StartX=0 StartY=0 StartZ=0 EndX=15 EndY=0 EndZ=0
    g3: LineSegment StartX=15 StartY=0 StartZ=0 EndX=15 EndY=60 EndZ=0
    g4: LineSegment StartX=15 StartY=60 StartZ=0 EndX=3 EndY=60 EndZ=0
    g5: LineSegment StartX=3 StartY=60 StartZ=0 EndX=-10 EndY=15 EndZ=0
  constraints (17):
    c: Distance(g0) = 10
    c: Coincident(g0,g-1)
    c: PointOnObject(g0,g-1)
    c: Distance(g1) = 15
    c: Coincident(g1,g0)
    c: Vertical(g1)
    c: Distance(g2) = 15
    c: Coincident(g2,g0)
    c: PointOnObject(g2,g-1)
    c: Distance(g3) = 60
    c: Coincident(g3,g2)
    c: Vertical(g3)
    c: Distance(g4) = 12
    c: Coincident(g4,g3)
    c: Horizontal(g4)
    c: Coincident(g5,g4)
    c: Coincident(g5,g1)
FEATURE [PartDesign::Pad] Pad001
  BaseFeature = -> Pad
  Direction = (1,0,0)
  Length = 15
  Length2 = 10
  Midplane = true
  Profile = -> Sketch001
  ReferenceAxis = -> Sketch001 [N_Axis]
  Refine = true
  Suppressed = false
  Type = 0
FEATURE [PartDesign::Chamfer] Chamfer
  Angle = 45
  Base = -> Pad001 [Edge37,Edge34,Edge29,Edge28,Edge33,Edge35,Edge30]
  BaseFeature = -> Pad001
  ChamferType = 0
  FlipDirection = false
  Refine = true
  Size = 2.5
  Size2 = 1
  SupportTransform = false
  Suppressed = false
  UseAllEdges = false
FEATURE [Sketcher::SketchObject] Sketch002
  ArcFitTolerance = 1e-06
  AttachmentSupport = -> [Chamfer]
  FullyConstrained = true
  MakeInternals = false
  MapMode = 5
  Placement = pos=(0,15,0) rot=(0,0.707107,0.707107;3.14159rad)
  sketch-geometry (2):
    g0: LineSegment [constr] StartX=0 StartY=0 StartZ=0 EndX=0 EndY=52.5 EndZ=0
    g1: Circle CenterX=0 CenterY=52.5 CenterZ=0 NormalX=0 NormalY=0 NormalZ=1 AngleXU=0 Radius=3.25
  constraints (5):
    c: Distance(g0) = 52.5
    c: Coincident(g0,g-1)
    c: Vertical(g0)
    c: Diameter(g1) = 6.5
    c: Coincident(g1,g0)
FEATURE [PartDesign::Pocket] Pocket
  BaseFeature = -> Chamfer
  Direction = (0,-1,2e-16)
  Length = 11
  Length2 = 5
  Profile = -> Sketch002
  ReferenceAxis = -> Sketch002 [N_Axis]
  Refine = true
  Suppressed = false
  Type = 0
FEATURE [Sketcher::SketchObject] Sketch003
  ArcFitTolerance = 1e-06
  AttachmentSupport = -> [Pocket]
  FullyConstrained = true
  MakeInternals = false
  MapMode = 5
  Placement = pos=(0,0,0) rot=(1,0,0;3.14159rad)
  sketch-geometry (4):
    g0: LineSegment [constr] StartX=0 StartY=0 StartZ=0 EndX=16 EndY=0 EndZ=0
    g1: LineSegment [constr] StartX=0 StartY=0 StartZ=0 EndX=-16 EndY=0 EndZ=0
    g2: Circle CenterX=-16 CenterY=0 CenterZ=0 NormalX=0 NormalY=0 NormalZ=1 AngleXU=0 Radius=2.6
    g3: Circle CenterX=16 CenterY=0 CenterZ=0 NormalX=0 NormalY=0 NormalZ=1 AngleXU=0 Radius=2.6
  constraints (10):
    c: Distance(g0) = 16
    c: Coincident(g0,g-1)
    c: PointOnObject(g0,g-1)
    c: Distance(g1) = 16
    c: Coincident(g1,g0)
    c: PointOnObject(g1,g-1)
    c: Diameter(g2) = 5.2
    c: Coincident(g2,g1)
    c: Diameter(g3) = 5.2
    c: Coincident(g3,g0)
FEATURE [PartDesign::Pocket] Pocket001
  BaseFeature = -> Pocket
  Direction = (0,0,1)
  Length = 5
  Length2 = 5
  Profile = -> Sketch003
  ReferenceAxis = -> Sketch003 [N_Axis]
  Refine = true
  Suppressed = false
  Type = 0
FEATURE [PartDesign::Body] Body  label="din_mount_body"
  AllowCompound = false
  Group = -> [Sketch,Pad,Sketch001,Pad001,Chamfer,Sketch002,Pocket,Sketch003,Pocket001]
  Origin = -> Origin
  Tip = -> Pocket001
FEATURE [App::Part] Part  label="din_mount_part"
  Group = -> [Body]
  Origin = -> Origin001
---- part dlp-power-supply-bracket.FCStd = doc fcstd_c4e9f56624bd ----
FCSTD DOCUMENT  (FreeCAD 1.0R39319 (Git))
Label: dlp-power-supply-bracket
License: All rights reserved
objects: Sketcher::SketchObject×5, PartDesign::Pad×5, PartDesign::Chamfer×3, PartDesign::Body×1, App::Part×1
note: 35 computed .brp shape members not serialized (recipe doc carries the construction recipe); baked Part::Feature solids carry a one-line shape summary decoded from their .brp

FEATURE [Sketcher::SketchObject] Sketch
  ArcFitTolerance = 1e-06
  AttachmentSupport = -> [XY_Plane001]
  FullyConstrained = true
  MakeInternals = false
  MapMode = 5
  sketch-geometry (10):
    g0: LineSegment StartX=-30.5 StartY=-16.5 StartZ=0 EndX=30.5 EndY=-16.5 EndZ=0
    g1: LineSegment StartX=30.5 StartY=-16.5 StartZ=0 EndX=30.5 EndY=16.5 EndZ=0
    g2: LineSegment StartX=30.5 StartY=16.5 StartZ=0 EndX=-30.5 EndY=16.5 EndZ=0
    g3: LineSegment StartX=-30.5 StartY=16.5 StartZ=0 EndX=-30.5 EndY=-16.5 EndZ=0
    g4: GeomPoint [constr] X=0 Y=0 Z=0
    g5: LineSegment StartX=-35.5 StartY=-21.5 StartZ=0 EndX=35.5 EndY=-21.5 EndZ=0
    g6: LineSegment StartX=35.5 StartY=-21.5 StartZ=0 EndX=35.5 EndY=21.5 EndZ=0
    g7: LineSegment StartX=35.5 StartY=21.5 StartZ=0 EndX=-35.5 EndY=21.5 EndZ=0
    g8: LineSegment StartX=-35.5 StartY=21.5 StartZ=0 EndX=-35.5 EndY=-21.5 EndZ=0
    g9: GeomPoint [constr] X=0 Y=0 Z=0
  constraints (24):
    c: Coincident(g0,g1)
    c: Coincident(g1,g2)
    c: Coincident(g2,g3)
    c: Coincident(g3,g0)
    c: Horizontal(g0)
    c: Horizontal(g2)
    c: Vertical(g1)
    c: Vertical(g3)
    c: Symmetric(g2,g0,g4)
    c: Distance(g1,g3) = 61
    c: Distance(g0,g2) = 33
    c: Coincident(g4,g-1)
    c: Coincident(g5,g6)
    c: Coincident(g6,g7)
    c: Coincident(g7,g8)
    c: Coincident(g8,g5)
    c: Horizontal(g5)
    c: Horizontal(g7)
    c: Vertical(g6)
    c: Vertical(g8)
    c: Symmetric(g7,g5,g9)
    c: Distance(g6,g8) = 71
    c: Distance(g5,g7) = 43
    c: Coincident(g9,g4)
FEATURE [PartDesign::Pad] Pad
  Direction = (0,0,1)
  Length = 10
  Length2 = 10
  Profile = -> Sketch
  ReferenceAxis = -> Sketch [N_Axis]
  Refine = true
  Suppressed = false
  Type = 0
FEATURE [Sketcher::SketchObject] Sketch001
  ArcFitTolerance = 1e-06
  AttachmentSupport = -> [Pad]
  FullyConstrained = true
  MakeInternals = false
  MapMode = 5
  Placement = pos=(0,0,0) rot=(1,0,0;3.14159rad)
  sketch-geometry (22):
    g0: LineSegment [constr] StartX=-30.5 StartY=-5 StartZ=0 EndX=30.5 EndY=-5 EndZ=0
    g1: LineSegment [constr] StartX=30.5 StartY=-5 StartZ=0 EndX=30.5 EndY=5 EndZ=0
    g2: LineSegment [constr] StartX=30.5 StartY=5 StartZ=0 EndX=-30.5 EndY=5 EndZ=0
    g3: LineSegment [constr] StartX=-30.5 StartY=5 StartZ=0 EndX=-30.5 EndY=-5 EndZ=0
    g4: GeomPoint [constr] X=0 Y=0 Z=0
    g5: LineSegment StartX=-30.5 StartY=5 StartZ=0 EndX=-35.5 EndY=5 EndZ=0
    g6: LineSegment StartX=-35.5 StartY=5 StartZ=0 EndX=-35.5 EndY=-5 EndZ=0
    g7: LineSegment StartX=-35.5 StartY=-5 StartZ=0 EndX=-30.5 EndY=-5 EndZ=0
    g8: LineSegment StartX=-30.5 StartY=-5 StartZ=0 EndX=-30.5 EndY=5 EndZ=0
    g9: LineSegment StartX=30.5 StartY=5 StartZ=0 EndX=30.5 EndY=-5 EndZ=0
    g10: LineSegment StartX=30.5 StartY=-5 StartZ=0 EndX=35.5 EndY=-5 EndZ=0
    g11: LineSegment StartX=35.5 StartY=-5 StartZ=0 EndX=35.5 EndY=5 EndZ=0
    g12: LineSegment StartX=35.5 StartY=5 StartZ=0 EndX=30.5 EndY=5 EndZ=0
    g13: LineSegment [constr] StartX=-5 StartY=-21.5 StartZ=0 EndX=5 EndY=-21.5 EndZ=0
    g14: LineSegment [constr] StartX=5 StartY=-21.5 StartZ=0 EndX=5 EndY=21.5 EndZ=0
    g15: LineSegment [constr] StartX=5 StartY=21.5 StartZ=0 EndX=-5 EndY=21.5 EndZ=0
    g16: LineSegment [constr] StartX=-5 StartY=21.5 StartZ=0 EndX=-5 EndY=-21.5 EndZ=0
    g17: GeomPoint [constr] X=0 Y=0 Z=0
    g18: LineSegment StartX=5 StartY=-21.5 StartZ=0 EndX=5 EndY=-16.5 EndZ=0
    g19: LineSegment StartX=5 StartY=-16.5 StartZ=0 EndX=-5 EndY=-16.5 EndZ=0
    g20: LineSegment StartX=-5 StartY=-16.5 StartZ=0 EndX=-5 EndY=-21.5 EndZ=0
    g21: LineSegment StartX=-5 StartY=-21.5 StartZ=0 EndX=5 EndY=-21.5 EndZ=0
  constraints (57):
    c: Coincident(g0,g1)
    c: Coincident(g1,g2)
    c: Coincident(g2,g3)
    c: Coincident(g3,g0)
    c: Horizontal(g0)
    c: Horizontal(g2)
    c: Vertical(g1)
    c: Vertical(g3)
    c: Symmetric(g2,g0,g4)
    c: Distance(g1,g3) = 61
    c: Distance(g0,g2) = 10
    c: Coincident(g4,g-1)
    c: Coincident(g5,g6)
    c: Coincident(g6,g7)
    c: Coincident(g7,g8)
    c: Coincident(g8,g5)
    c: Horizontal(g5)
    c: Horizontal(g7)
    c: Vertical(g6)
    c: Vertical(g8)
    c: Distance(g6,g8) = 5
    c: Distance(g5,g7) = 10
    c: Coincident(g5,g2)
    c: Coincident(g9,g10)
    c: Coincident(g10,g11)
    c: Coincident(g11,g12)
    c: Coincident(g12,g9)
    c: Vertical(g9)
    c: Vertical(g11)
    c: Horizontal(g10)
    c: Horizontal(g12)
    c: Distance(g9,g11) = 5
    c: Distance(g10,g12) = 10
    c: Coincident(g9,g1)
    c: Coincident(g13,g14)
    c: Coincident(g14,g15)
    c: Coincident(g15,g16)
    c: Coincident(g16,g13)
    c: Horizontal(g13)
    c: Horizontal(g15)
    c: Vertical(g14)
    c: Vertical(g16)
    c: Symmetric(g15,g13,g17)
    c: Distance(g14,g16) = 10
    c: Distance(g13,g15) = 43
    c: Coincident(g17,g4)
    c: Coincident(g18,g19)
    c: Coincident(g19,g20)
    c: Coincident(g20,g21)
    c: Coincident(g21,g18)
    c: Vertical(g18)
    c: Vertical(g20)
    c: Horizontal(g19)
    c: Horizontal(g21)
    c: Distance(g19,g21) = 5
    c: Coincident(g18,g13)
    c: PointOnObject(g19,g16)
FEATURE [PartDesign::Pad] Pad001
  BaseFeature = -> Pad
  Direction = (0,0,-1)
  Length = 120
  Length2 = 10
  Profile = -> Sketch001
  ReferenceAxis = -> Sketch001 [N_Axis]
  Refine = true
  Suppressed = false
  Type = 0
FEATURE [Sketcher::SketchObject] Sketch002
  ArcFitTolerance = 1e-06
  AttachmentSupport = -> [Pad001]
  FullyConstrained = true
  MakeInternals = false
  MapMode = 5
  Placement = pos=(0,16.5,0) rot=(1,0,0;1.5708rad)
  sketch-geometry (6):
    g0: LineSegment [constr] StartX=0 StartY=0 StartZ=0 EndX=7.2e-15 EndY=-117.5 EndZ=0
    g1: LineSegment StartX=-5 StartY=-120 StartZ=0 EndX=5 EndY=-120 EndZ=0
    g2: LineSegment StartX=5 StartY=-120 StartZ=0 EndX=5 EndY=-115 EndZ=0
    g3: LineSegment StartX=5 StartY=-115 StartZ=0 EndX=-5 EndY=-115 EndZ=0
    g4: LineSegment StartX=-5 StartY=-115 StartZ=0 EndX=-5 EndY=-120 EndZ=0
    g5: GeomPoint [constr] X=7.2e-15 Y=-117.5 Z=0
  constraints (15):
    c: Distance(g0) = 117.5
    c: Angle(g-1,g0) = -1.5708
    c: Coincident(g0,g-1)
    c: Coincident(g1,g2)
    c: Coincident(g2,g3)
    c: Coincident(g3,g4)
    c: Coincident(g4,g1)
    c: Horizontal(g1)
    c: Horizontal(g3)
    c: Vertical(g2)
    c: Vertical(g4)
    c: Symmetric(g3,g1,g5)
    c: Distance(g2,g4) = 10
    c: Distance(g1,g3) = 5
    c: Coincident(g5,g0)
FEATURE [PartDesign::Pad] Pad002
  BaseFeature = -> Pad001
  Direction = (0,-1,2e-16)
  Length = 5
  Length2 = 10
  Profile = -> Sketch002
  ReferenceAxis = -> Sketch002 [N_Axis]
  Refine = true
  Suppressed = false
  Type = 0
FEATURE [Sketcher::SketchObject] Sketch003
  ArcFitTolerance = 1e-06
  AttachmentSupport = -> [Pad002]
  FullyConstrained = true
  MakeInternals = false
  MapMode = 5
  Placement = pos=(0,0,-120) rot=(1,0,0;3.14159rad)
  sketch-geometry (15):
    g0: LineSegment [constr] StartX=-35.5 StartY=-5 StartZ=0 EndX=35.5 EndY=-5 EndZ=0
    g1: LineSegment [constr] StartX=35.5 StartY=-5 StartZ=0 EndX=35.5 EndY=5 EndZ=0
    g2: LineSegment [constr] StartX=35.5 StartY=5 StartZ=0 EndX=-35.5 EndY=5 EndZ=0
    g3: LineSegment [constr] StartX=-35.5 StartY=5 StartZ=0 EndX=-35.5 EndY=-5 EndZ=0
    g4: GeomPoint [constr] X=0 Y=0 Z=0
    g5: LineSegment StartX=-35.5 StartY=5 StartZ=0 EndX=-35.5 EndY=-5 EndZ=0
    g6: LineSegment [constr] StartX=-35.5 StartY=-5 StartZ=0 EndX=-19.5 EndY=-5 EndZ=0
    g7: LineSegment StartX=-19.5 StartY=-5 StartZ=0 EndX=-19.5 EndY=5 EndZ=0
    g8: LineSegment StartX=-19.5 StartY=5 StartZ=0 EndX=-35.5 EndY=5 EndZ=0
    g9: LineSegment StartX=35.5 StartY=5 StartZ=0 EndX=19.5 EndY=5 EndZ=0
    g10: LineSegment StartX=19.5 StartY=5 StartZ=0 EndX=19.5 EndY=-5 EndZ=0
    g11: LineSegment [constr] StartX=19.5 StartY=-5 StartZ=0 EndX=35.5 EndY=-5 EndZ=0
    g12: LineSegment StartX=35.5 StartY=-5 StartZ=0 EndX=35.5 EndY=5 EndZ=0
    g13: LineSegment StartX=-35.5 StartY=-5 StartZ=0 EndX=-19.5 EndY=-5 EndZ=0
    g14: LineSegment StartX=19.5 StartY=-5 StartZ=0 EndX=35.5 EndY=-5 EndZ=0
  constraints (38):
    c: Coincident(g0,g1)
    c: Coincident(g1,g2)
    c: Coincident(g2,g3)
    c: Coincident(g3,g0)
    c: Horizontal(g0)
    c: Horizontal(g2)
    c: Vertical(g1)
    c: Vertical(g3)
    c: Symmetric(g2,g0,g4)
    c: Distance(g1,g3) = 71
    c: Distance(g0,g2) = 10
    c: Coincident(g4,g-1)
    c: Coincident(g5,g6)
    c: Coincident(g6,g7)
    c: Coincident(g7,g8)
    c: Coincident(g8,g5)
    c: Vertical(g5)
    c: Vertical(g7)
    c: Horizontal(g6)
    c: Horizontal(g8)
    c: Distance(g5,g7) = 16
    c: Coincident(g5,g2)
    c: PointOnObject(g6,g0)
    c: Coincident(g9,g10)
    c: Coincident(g10,g11)
    c: Coincident(g11,g12)
    c: Coincident(g12,g9)
    c: Horizontal(g9)
    c: Horizontal(g11)
    c: Vertical(g10)
    c: Vertical(g12)
    c: Distance(g10,g12) = 16
    c: Coincident(g9,g1)
    c: PointOnObject(g10,g0)
    c: Coincident(g13,g0)
    c: Coincident(g13,g6)
    c: Coincident(g14,g10)
    c: Coincident(g14,g0)
FEATURE [PartDesign::Pad] Pad003
  BaseFeature = -> Pad002
  Direction = (0,0,-1)
  Length = 5
  Length2 = 10
  Profile = -> Sketch003
  ReferenceAxis = -> Sketch003 [N_Axis]
  Refine = true
  Reversed = true
  Suppressed = false
  Type = 0
FEATURE [PartDesign::Chamfer] Chamfer
  Angle = 45
  Base = -> Pad003 [Edge48,Edge53,Edge4,Edge1,Edge34,Edge31,Edge24,Edge59,Edge28,Edge58]
  BaseFeature = -> Pad003
  ChamferType = 0
  FlipDirection = false
  Refine = true
  Size = 5
  Size2 = 1
  SupportTransform = false
  Suppressed = false
  UseAllEdges = false
FEATURE [Sketcher::SketchObject] Sketch004
  ArcFitTolerance = 1e-06
  AttachmentSupport = -> [Chamfer]
  FullyConstrained = true
  MakeInternals = false
  MapMode = 5
  Placement = pos=(0,0,10) rot=(0,0,1;0rad)
  sketch-geometry (7):
    g0: LineSegment [constr] StartX=0 StartY=0 StartZ=0 EndX=0 EndY=36.5 EndZ=0
    g1: LineSegment StartX=-15 StartY=21.5 StartZ=0 EndX=15 EndY=21.5 EndZ=0
    g2: LineSegment StartX=15 StartY=21.5 StartZ=0 EndX=15 EndY=51.5 EndZ=0
    g3: LineSegment StartX=15 StartY=51.5 StartZ=0 EndX=-15 EndY=51.5 EndZ=0
    g4: LineSegment StartX=-15 StartY=51.5 StartZ=0 EndX=-15 EndY=21.5 EndZ=0
    g5: GeomPoint [constr] X=0 Y=36.5 Z=0
    g6: Circle CenterX=0 CenterY=36.5 CenterZ=0 NormalX=0 NormalY=0 NormalZ=1 AngleXU=0 Radius=2.6
  constraints (17):
    c: Distance(g0) = 36.5
    c: Coincident(g0,g-1)
    c: PointOnObject(g0,g-2)
    c: Coincident(g1,g2)
    c: Coincident(g2,g3)
    c: Coincident(g3,g4)
    c: Coincident(g4,g1)
    c: Horizontal(g1)
    c: Horizontal(g3)
    c: Vertical(g2)
    c: Vertical(g4)
    c: Symmetric(g3,g1,g5)
    c: Distance(g2,g4) = 30
    c: Distance(g1,g3) = 30
    c: Coincident(g5,g0)
    c: Diameter(g6) = 5.2
    c: Coincident(g6,g0)
FEATURE [PartDesign::Pad] Pad004
  BaseFeature = -> Chamfer
  Direction = (0,0,1)
  Length = 5
  Length2 = 10
  Profile = -> Sketch004
  ReferenceAxis = -> Sketch004 [N_Axis]
  Refine = true
  Reversed = true
  Suppressed = false
  Type = 0
FEATURE [PartDesign::Chamfer] Chamfer001
  Angle = 45
  Base = -> Pad004 [Edge40,Edge42,Edge96,Edge90]
  BaseFeature = -> Pad004
  ChamferType = 0
  FlipDirection = false
  Refine = true
  Size = 5
  Size2 = 1
  SupportTransform = false
  Suppressed = false
  UseAllEdges = false
FEATURE [PartDesign::Chamfer] Chamfer002
  Angle = 45
  Base = -> Chamfer001 [Edge78,Edge11,Edge92]
  BaseFeature = -> Chamfer001
  ChamferType = 0
  FlipDirection = false
  Refine = true
  Size = 2
  Size2 = 1
  SupportTransform = false
  Suppressed = false
  UseAllEdges = false
FEATURE [PartDesign::Body] Body  label="dlp-power-supply-bracket-body"
  AllowCompound = false
  Group = -> [Sketch,Pad,Sketch001,Pad001,Sketch002,Pad002,Sketch003,Pad003,Chamfer,Sketch004,Pad004,Chamfer001,Chamfer002]
  Origin = -> Origin001
  Tip = -> Chamfer002
FEATURE [App::Part] Part  label="dlp-power-supply-bracket-part"
  Group = -> [Body]
  Origin = -> Origin
---- part ports-panel.FCStd = doc fcstd_98e8bd0c9e7b ----
FCSTD DOCUMENT  (FreeCAD 1.0R39319 (Git))
Label: ports-panel
License: All rights reserved
objects: Sketcher::SketchObject×9, PartDesign::Pocket×7, PartDesign::Pad×2, PartDesign::Chamfer×2, PartDesign::Body×1, App::Part×1
note: 52 computed .brp shape members not serialized (recipe doc carries the construction recipe); baked Part::Feature solids carry a one-line shape summary decoded from their .brp

FEATURE [Sketcher::SketchObject] Sketch
  ArcFitTolerance = 1e-06
  AttachmentSupport = -> [XY_Plane]
  FullyConstrained = true
  MakeInternals = false
  MapMode = 5
  sketch-geometry (5):
    g0: LineSegment StartX=-115 StartY=-37.5 StartZ=0 EndX=115 EndY=-37.5 EndZ=0
    g1: LineSegment StartX=115 StartY=-37.5 StartZ=0 EndX=115 EndY=37.5 EndZ=0
    g2: LineSegment StartX=115 StartY=37.5 StartZ=0 EndX=-115 EndY=37.5 EndZ=0
    g3: LineSegment StartX=-115 StartY=37.5 StartZ=0 EndX=-115 EndY=-37.5 EndZ=0
    g4: GeomPoint [constr] X=0 Y=-1e-16 Z=0
  constraints (12):
    c: Coincident(g0,g1)
    c: Coincident(g1,g2)
    c: Coincident(g2,g3)
    c: Coincident(g3,g0)
    c: Horizontal(g0)
    c: Horizontal(g2)
    c: Vertical(g1)
    c: Vertical(g3)
    c: Symmetric(g2,g0,g4)
    c: Distance(g1,g3) = 230
    c: Distance(g0,g2) = 75
    c: Coincident(g4,g-1)
FEATURE [PartDesign::Pad] Pad
  Direction = (0,0,1)
  Length = 6.2
  Length2 = 10
  Profile = -> Sketch
  ReferenceAxis = -> Sketch [N_Axis]
  Refine = true
  Suppressed = false
  Type = 0
FEATURE [Sketcher::SketchObject] Sketch001
  ArcFitTolerance = 1e-06
  AttachmentSupport = -> [Pad]
  FullyConstrained = true
  MakeInternals = false
  MapMode = 5
  Placement = pos=(0,0,6.2) rot=(0,0,1;0rad)
  sketch-geometry (9):
    g0: LineSegment [constr] StartX=-115 StartY=-37.5 StartZ=0 EndX=115 EndY=-37.5 EndZ=0
    g1: LineSegment [constr] StartX=115 StartY=-37.5 StartZ=0 EndX=115 EndY=37.5 EndZ=0
    g2: LineSegment [constr] StartX=115 StartY=37.5 StartZ=0 EndX=-115 EndY=37.5 EndZ=0
    g3: LineSegment [constr] StartX=-115 StartY=37.5 StartZ=0 EndX=-115 EndY=-37.5 EndZ=0
    g4: GeomPoint [constr] X=0 Y=0 Z=0
    g5: LineSegment StartX=115 StartY=37.5 StartZ=0 EndX=-96 EndY=37.5 EndZ=0
    g6: LineSegment StartX=-96 StartY=37.5 StartZ=0 EndX=-96 EndY=33.5 EndZ=0
    g7: LineSegment StartX=-96 StartY=33.5 StartZ=0 EndX=115 EndY=33.5 EndZ=0
    g8: LineSegment StartX=115 StartY=33.5 StartZ=0 EndX=115 EndY=37.5 EndZ=0
  constraints (23):
    c: Coincident(g0,g1)
    c: Coincident(g1,g2)
    c: Coincident(g2,g3)
    c: Coincident(g3,g0)
    c: Horizontal(g0)
    c: Horizontal(g2)
    c: Vertical(g1)
    c: Vertical(g3)
    c: Symmetric(g2,g0,g4)
    c: Distance(g1,g3) = 230
    c: Distance(g0,g2) = 75
    c: Coincident(g4,g-1)
    c: Coincident(g5,g6)
    c: Coincident(g6,g7)
    c: Coincident(g7,g8)
    c: Coincident(g8,g5)
    c: Horizontal(g5)
    c: Horizontal(g7)
    c: Vertical(g6)
    c: Vertical(g8)
    c: Distance(g6,g8) = 211
    c: Distance(g5,g7) = 4
    c: Coincident(g5,g1)
FEATURE [PartDesign::Pocket] Pocket
  BaseFeature = -> Pad
  Direction = (0,0,-1)
  Length = 3.2
  Length2 = 5
  Profile = -> Sketch001
  ReferenceAxis = -> Sketch001 [N_Axis]
  Refine = true
  Suppressed = false
  Type = 0
FEATURE [PartDesign::Chamfer] Chamfer
  Angle = 45
  Base = -> Pocket [Edge6,Edge3,Edge8]
  BaseFeature = -> Pocket
  ChamferType = 0
  FlipDirection = false
  Refine = true
  Size = 2
  Size2 = 1
  SupportTransform = false
  Suppressed = false
  UseAllEdges = false
FEATURE [Sketcher::SketchObject] Sketch002
  ArcFitTolerance = 1e-06
  AttachmentSupport = -> [Chamfer]
  FullyConstrained = true
  MakeInternals = false
  MapMode = 5
  Placement = pos=(0,0,6.2) rot=(0,0,1;0rad)
  sketch-geometry (9):
    g0: LineSegment [constr] StartX=-100 StartY=-22.5 StartZ=0 EndX=100 EndY=-22.5 EndZ=0
    g1: LineSegment [constr] StartX=100 StartY=-22.5 StartZ=0 EndX=100 EndY=22.5 EndZ=0
    g2: LineSegment [constr] StartX=100 StartY=22.5 StartZ=0 EndX=-100 EndY=22.5 EndZ=0
    g3: LineSegment [constr] StartX=-100 StartY=22.5 StartZ=0 EndX=-100 EndY=-22.5 EndZ=0
    g4: GeomPoint [constr] X=0 Y=0 Z=0
    g5: Circle CenterX=-100 CenterY=-22.5 CenterZ=0 NormalX=0 NormalY=0 NormalZ=1 AngleXU=0 Radius=2.6
    g6: Circle CenterX=0 CenterY=-22.5 CenterZ=0 NormalX=0 NormalY=0 NormalZ=1 AngleXU=0 Radius=2.6
    g7: Circle CenterX=100 CenterY=-22.5 CenterZ=0 NormalX=0 NormalY=0 NormalZ=1 AngleXU=0 Radius=2.6
    g8: Circle CenterX=-100 CenterY=22.5 CenterZ=0 NormalX=0 NormalY=0 NormalZ=1 AngleXU=0 Radius=2.6
  constraints (20):
    c: Coincident(g0,g1)
    c: Coincident(g1,g2)
    c: Coincident(g2,g3)
    c: Coincident(g3,g0)
    c: Horizontal(g0)
    c: Horizontal(g2)
    c: Vertical(g1)
    c: Vertical(g3)
    c: Symmetric(g2,g0,g4)
    c: Distance(g1,g3) = 200
    c: Distance(g0,g2) = 45
    c: Coincident(g4,g-1)
    c: Diameter(g5) = 5.2
    c: Coincident(g5,g0)
    c: Diameter(g6) = 5.2
    c: Symmetric(g0,g0,g6)
    c: Diameter(g7) = 5.2
    c: Coincident(g7,g0)
    c: Diameter(g8) = 5.2
    c: Coincident(g8,g2)
FEATURE [PartDesign::Pocket] Pocket001
  BaseFeature = -> Chamfer
  Direction = (0,0,-1)
  Length = 10
  Length2 = 5
  Profile = -> Sketch002
  ReferenceAxis = -> Sketch002 [N_Axis]
  Refine = true
  Suppressed = false
  Type = 0
FEATURE [Sketcher::SketchObject] Sketch003
  ArcFitTolerance = 1e-06
  AttachmentSupport = -> [Pocket001]
  FullyConstrained = true
  MakeInternals = false
  MapMode = 5
  Placement = pos=(0,0,0) rot=(1,0,0;3.14159rad)
  sketch-geometry (17):
    g0: LineSegment [constr] StartX=-115 StartY=-37.5 StartZ=0 EndX=115 EndY=-37.5 EndZ=0
    g1: LineSegment [constr] StartX=115 StartY=-37.5 StartZ=0 EndX=115 EndY=37.5 EndZ=0
    g2: LineSegment [constr] StartX=115 StartY=37.5 StartZ=0 EndX=-115 EndY=37.5 EndZ=0
    g3: LineSegment [constr] StartX=-115 StartY=37.5 StartZ=0 EndX=-115 EndY=-37.5 EndZ=0
    g4: GeomPoint [constr] X=0 Y=0 Z=0
    g5: LineSegment [constr] StartX=115 StartY=37.5 StartZ=0 EndX=-115 EndY=37.5 EndZ=0
    g6: LineSegment [constr] StartX=-115 StartY=37.5 StartZ=0 EndX=-115 EndY=7.5 EndZ=0
    g7: LineSegment [constr] StartX=-115 StartY=7.5 StartZ=0 EndX=115 EndY=7.5 EndZ=0
    g8: LineSegment [constr] StartX=115 StartY=7.5 StartZ=0 EndX=115 EndY=37.5 EndZ=0
    g9: LineSegment [constr] StartX=0 StartY=0 StartZ=0 EndX=0 EndY=-1 EndZ=0
    g10: LineSegment [constr] StartX=0 StartY=-1 StartZ=0 EndX=20 EndY=-1 EndZ=0
    g11: LineSegment [constr] StartX=20 StartY=-1 StartZ=0 EndX=20 EndY=0 EndZ=0
    g12: LineSegment [constr] StartX=20 StartY=0 StartZ=0 EndX=0 EndY=0 EndZ=0
    g13: LineSegment StartX=20 StartY=-1 StartZ=0 EndX=20 EndY=-28.2 EndZ=0
    g14: LineSegment StartX=20 StartY=-28.2 StartZ=0 EndX=67.4 EndY=-28.2 EndZ=0
    g15: LineSegment StartX=67.4 StartY=-28.2 StartZ=0 EndX=67.4 EndY=-1 EndZ=0
    g16: LineSegment StartX=67.4 StartY=-1 StartZ=0 EndX=20 EndY=-1 EndZ=0
  constraints (45):
    c: Coincident(g0,g1)
    c: Coincident(g1,g2)
    c: Coincident(g2,g3)
    c: Coincident(g3,g0)
    c: Horizontal(g0)
    c: Horizontal(g2)
    c: Vertical(g1)
    c: Vertical(g3)
    c: Symmetric(g2,g0,g4)
    c: Distance(g1,g3) = 230
    c: Distance(g0,g2) = 75
    c: Coincident(g4,g-1)
    c: Coincident(g5,g6)
    c: Coincident(g6,g7)
    c: Coincident(g7,g8)
    c: Coincident(g8,g5)
    c: Horizontal(g5)
    c: Horizontal(g7)
    c: Vertical(g6)
    c: Vertical(g8)
    c: Distance(g5,g7) = 30
    c: Coincident(g5,g1)
    c: PointOnObject(g6,g3)
    c: Coincident(g9,g10)
    c: Coincident(g10,g11)
    c: Coincident(g11,g12)
    c: Coincident(g12,g9)
    c: Vertical(g9)
    c: Vertical(g11)
    c: Horizontal(g10)
    c: Horizontal(g12)
    c: Distance(g9,g11) = 20
    c: Distance(g10,g12) = 1
    c: Coincident(g9,g4)
    c: Coincident(g13,g14)
    c: Coincident(g14,g15)
    c: Coincident(g15,g16)
    c: Coincident(g16,g13)
    c: Vertical(g13)
    c: Vertical(g15)
    c: Horizontal(g14)
    c: Horizontal(g16)
    c: Distance(g13,g15) = 47.4
    c: Distance(g14,g16) = 27.2
    c: Coincident(g13,g10)
FEATURE [PartDesign::Pocket] Pocket002
  BaseFeature = -> Pocket001
  Direction = (0,0,1)
  Length = 7
  Length2 = 5
  Profile = -> Sketch003
  ReferenceAxis = -> Sketch003 [N_Axis]
  Refine = true
  Suppressed = false
  Type = 0
FEATURE [Sketcher::SketchObject] Sketch004
  ArcFitTolerance = 1e-06
  AttachmentSupport = -> [Pocket002]
  FullyConstrained = true
  MakeInternals = false
  MapMode = 5
  Placement = pos=(0,0,6.2) rot=(0,0,1;0rad)
  sketch-geometry (15):
    g0: LineSegment [constr] StartX=0 StartY=0 StartZ=0 EndX=30.7 EndY=0 EndZ=0
    g1: LineSegment [constr] StartX=30.7 StartY=0 StartZ=0 EndX=30.7 EndY=14.6 EndZ=0
    g2: LineSegment [constr] StartX=30.7 StartY=14.6 StartZ=0 EndX=0 EndY=14.6 EndZ=0
    g3: LineSegment [constr] StartX=0 StartY=14.6 StartZ=0 EndX=0 EndY=0 EndZ=0
    g4: LineSegment StartX=23.2 StartY=-0.4 StartZ=0 EndX=38.2 EndY=-0.4 EndZ=0
    g5: LineSegment StartX=38.2 StartY=-0.4 StartZ=0 EndX=38.2 EndY=29.6 EndZ=0
    g6: LineSegment StartX=38.2 StartY=29.6 StartZ=0 EndX=23.2 EndY=29.6 EndZ=0
    g7: LineSegment StartX=23.2 StartY=29.6 StartZ=0 EndX=23.2 EndY=-0.4 EndZ=0
    g8: GeomPoint [constr] X=30.7 Y=14.6 Z=0
    g9: LineSegment [constr] StartX=30.7 StartY=14.6 StartZ=0 EndX=56.7 EndY=14.6 EndZ=0
    g10: LineSegment StartX=49.2 StartY=-0.4 StartZ=0 EndX=64.2 EndY=-0.4 EndZ=0
    g11: LineSegment StartX=64.2 StartY=-0.4 StartZ=0 EndX=64.2 EndY=29.6 EndZ=0
    g12: LineSegment StartX=64.2 StartY=29.6 StartZ=0 EndX=49.2 EndY=29.6 EndZ=0
    g13: LineSegment StartX=49.2 StartY=29.6 StartZ=0 EndX=49.2 EndY=-0.4 EndZ=0
    g14: GeomPoint [constr] X=56.7 Y=14.6 Z=0
  constraints (38):
    c: Coincident(g0,g1)
    c: Coincident(g1,g2)
    c: Coincident(g2,g3)
    c: Coincident(g3,g0)
    c: Horizontal(g0)
    c: Horizontal(g2)
    c: Vertical(g1)
    c: Vertical(g3)
    c: Distance(g1,g3) = 30.7
    c: Distance(g0,g2) = 14.6
    c: Coincident(g0,g-1)
    c: Coincident(g4,g5)
    c: Coincident(g5,g6)
    c: Coincident(g6,g7)
    c: Coincident(g7,g4)
    c: Horizontal(g4)
    c: Horizontal(g6)
    c: Vertical(g5)
    c: Vertical(g7)
    c: Symmetric(g6,g4,g8)
    c: Distance(g5,g7) = 15
    c: Distance(g4,g6) = 30
    c: Coincident(g8,g1)
    c: Distance(g9) = 26
    c: Coincident(g9,g1)
    c: Horizontal(g9)
    c: Coincident(g10,g11)
    c: Coincident(g11,g12)
    c: Coincident(g12,g13)
    c: Coincident(g13,g10)
    c: Horizontal(g10)
    c: Horizontal(g12)
    c: Vertical(g11)
    c: Vertical(g13)
    c: Symmetric(g12,g10,g14)
    c: Distance(g11,g13) = 15
    c: Distance(g10,g12) = 30
    c: Coincident(g14,g9)
FEATURE [PartDesign::Pocket] Pocket003
  BaseFeature = -> Pocket002
  Direction = (0,0,-1)
  Length = 5.6
  Length2 = 5
  Profile = -> Sketch004
  ReferenceAxis = -> Sketch004 [N_Axis]
  Refine = true
  Suppressed = false
  Type = 0
FEATURE [Sketcher::SketchObject] Sketch005
  ArcFitTolerance = 1e-06
  AttachmentSupport = -> [Pocket003]
  FullyConstrained = true
  MakeInternals = false
  MapMode = 5
  Placement = pos=(0,0,6.2) rot=(0,0,1;0rad)
  sketch-geometry (18):
    g0: LineSegment [constr] StartX=-115 StartY=-37.5 StartZ=0 EndX=115 EndY=-37.5 EndZ=0
    g1: LineSegment [constr] StartX=115 StartY=-37.5 StartZ=0 EndX=115 EndY=37.5 EndZ=0
    g2: LineSegment [constr] StartX=115 StartY=37.5 StartZ=0 EndX=-115 EndY=37.5 EndZ=0
    g3: LineSegment [constr] StartX=-115 StartY=37.5 StartZ=0 EndX=-115 EndY=-37.5 EndZ=0
    g4: GeomPoint [constr] X=0 Y=0 Z=0
    g5: LineSegment [constr] StartX=115 StartY=-37.5 StartZ=0 EndX=115 EndY=-7.5 EndZ=0
    g6: LineSegment [constr] StartX=115 StartY=-7.5 StartZ=0 EndX=-115 EndY=-7.5 EndZ=0
    g7: LineSegment [constr] StartX=-115 StartY=-7.5 StartZ=0 EndX=-115 EndY=-37.5 EndZ=0
    g8: LineSegment [constr] StartX=-115 StartY=-37.5 StartZ=0 EndX=115 EndY=-37.5 EndZ=0
    g9: LineSegment [constr] StartX=0 StartY=0 StartZ=0 EndX=0 EndY=14.2 EndZ=0
    g10: LineSegment [constr] StartX=0 StartY=14.2 StartZ=0 EndX=-40 EndY=14.2 EndZ=0
    g11: LineSegment [constr] StartX=-40 StartY=14.2 StartZ=0 EndX=-40 EndY=0 EndZ=0
    g12: LineSegment [constr] StartX=-40 StartY=0 StartZ=0 EndX=0 EndY=0 EndZ=0
    g13: LineSegment StartX=-48 StartY=7.6 StartZ=0 EndX=-32 EndY=7.6 EndZ=0
    g14: LineSegment StartX=-32 StartY=7.6 StartZ=0 EndX=-32 EndY=20.8 EndZ=0
    g15: LineSegment StartX=-32 StartY=20.8 StartZ=0 EndX=-48 EndY=20.8 EndZ=0
    g16: LineSegment StartX=-48 StartY=20.8 StartZ=0 EndX=-48 EndY=7.6 EndZ=0
    g17: GeomPoint [constr] X=-40 Y=14.2 Z=0
  constraints (46):
    c: Coincident(g0,g1)
    c: Coincident(g1,g2)
    c: Coincident(g2,g3)
    c: Coincident(g3,g0)
    c: Horizontal(g0)
    c: Horizontal(g2)
    c: Vertical(g1)
    c: Vertical(g3)
    c: Symmetric(g2,g0,g4)
    c: Distance(g1,g3) = 230
    c: Distance(g0,g2) = 75
    c: Coincident(g4,g-1)
    c: Coincident(g5,g6)
    c: Coincident(g6,g7)
    c: Coincident(g7,g8)
    c: Coincident(g8,g5)
    c: Vertical(g5)
    c: Vertical(g7)
    c: Horizontal(g6)
    c: Horizontal(g8)
    c: Distance(g6,g8) = 30
    c: Coincident(g5,g0)
    c: PointOnObject(g6,g3)
    c: Coincident(g9,g10)
    c: Coincident(g10,g11)
    c: Coincident(g11,g12)
    c: Coincident(g12,g9)
    c: Vertical(g9)
    c: Vertical(g11)
    c: Horizontal(g10)
    c: Horizontal(g12)
    c: Distance(g9,g11) = 40
    c: Distance(g10,g12) = 14.2
    c: Coincident(g9,g4)
    c: Coincident(g13,g14)
    c: Coincident(g14,g15)
    c: Coincident(g15,g16)
    c: Coincident(g16,g13)
    c: Horizontal(g13)
    c: Horizontal(g15)
    c: Vertical(g14)
    c: Vertical(g16)
    c: Symmetric(g15,g13,g17)
    c: Distance(g14,g16) = 16
    c: Distance(g13,g15) = 13.2
    c: Coincident(g17,g10)
FEATURE [PartDesign::Pocket] Pocket004
  BaseFeature = -> Pocket003
  Direction = (0,0,-1)
  Length = 8
  Length2 = 5
  Profile = -> Sketch005
  ReferenceAxis = -> Sketch005 [N_Axis]
  Refine = true
  Suppressed = false
  Type = 0
FEATURE [Sketcher::SketchObject] Sketch006
  ArcFitTolerance = 1e-06
  AttachmentSupport = -> [Pocket004]
  FullyConstrained = true
  MakeInternals = false
  MapMode = 5
  Placement = pos=(0,0,6.2) rot=(0,0,1;0rad)
  sketch-geometry (9):
    g0: LineSegment [constr] StartX=0 StartY=0 StartZ=0 EndX=0 EndY=14.2 EndZ=0
    g1: LineSegment [constr] StartX=0 StartY=14.2 StartZ=0 EndX=-40 EndY=14.2 EndZ=0
    g2: LineSegment [constr] StartX=-40 StartY=14.2 StartZ=0 EndX=-40 EndY=0 EndZ=0
    g3: LineSegment [constr] StartX=-40 StartY=0 StartZ=0 EndX=0 EndY=0 EndZ=0
    g4: LineSegment StartX=-50.25 StartY=4.95 StartZ=0 EndX=-29.75 EndY=4.95 EndZ=0
    g5: LineSegment StartX=-29.75 StartY=4.95 StartZ=0 EndX=-29.75 EndY=23.45 EndZ=0
    g6: LineSegment StartX=-29.75 StartY=23.45 StartZ=0 EndX=-50.25 EndY=23.45 EndZ=0
    g7: LineSegment StartX=-50.25 StartY=23.45 StartZ=0 EndX=-50.25 EndY=4.95 EndZ=0
    g8: GeomPoint [constr] X=-40 Y=14.2 Z=0
  constraints (23):
    c: Coincident(g0,g1)
    c: Coincident(g1,g2)
    c: Coincident(g2,g3)
    c: Coincident(g3,g0)
    c: Vertical(g0)
    c: Vertical(g2)
    c: Horizontal(g1)
    c: Horizontal(g3)
    c: Distance(g0,g2) = 40
    c: Distance(g1,g3) = 14.2
    c: Coincident(g0,g-1)
    c: Coincident(g4,g5)
    c: Coincident(g5,g6)
    c: Coincident(g6,g7)
    c: Coincident(g7,g4)
    c: Horizontal(g4)
    c: Horizontal(g6)
    c: Vertical(g5)
    c: Vertical(g7)
    c: Symmetric(g6,g4,g8)
    c: Distance(g5,g7) = 20.5
    c: Distance(g4,g6) = 18.5
    c: Coincident(g8,g1)
FEATURE [PartDesign::Pocket] Pocket005
  BaseFeature = -> Pocket004
  Direction = (0,0,-1)
  Length = 5.6
  Length2 = 5
  Profile = -> Sketch006
  ReferenceAxis = -> Sketch006 [N_Axis]
  Refine = true
  Suppressed = false
  Type = 0
FEATURE [Sketcher::SketchObject] Sketch007
  ArcFitTolerance = 1e-06
  AttachmentSupport = -> [Pocket005]
  FullyConstrained = true
  MakeInternals = false
  MapMode = 5
  Placement = pos=(0,0,6.2) rot=(0,0,1;0rad)
  sketch-geometry (14):
    g0: LineSegment [constr] StartX=0 StartY=0 StartZ=0 EndX=0 EndY=14.2 EndZ=0
    g1: LineSegment [constr] StartX=0 StartY=14.2 StartZ=0 EndX=-40 EndY=14.2 EndZ=0
    g2: LineSegment [constr] StartX=-40 StartY=14.2 StartZ=0 EndX=-40 EndY=0 EndZ=0
    g3: LineSegment [constr] StartX=-40 StartY=0 StartZ=0 EndX=0 EndY=0 EndZ=0
    g4: LineSegment StartX=-50.25 StartY=4.95 StartZ=0 EndX=-29.75 EndY=4.95 EndZ=0
    g5: LineSegment StartX=-29.75 StartY=4.95 StartZ=0 EndX=-29.75 EndY=23.45 EndZ=0
    g6: LineSegment StartX=-29.75 StartY=23.45 StartZ=0 EndX=-50.25 EndY=23.45 EndZ=0
    g7: LineSegment StartX=-50.25 StartY=23.45 StartZ=0 EndX=-50.25 EndY=4.95 EndZ=0
    g8: GeomPoint [constr] X=-40 Y=14.2 Z=0
    g9: LineSegment StartX=-53.5 StartY=1.7 StartZ=0 EndX=-26.5 EndY=1.7 EndZ=0
    g10: LineSegment StartX=-26.5 StartY=1.7 StartZ=0 EndX=-26.5 EndY=26.7 EndZ=0
    g11: LineSegment StartX=-26.5 StartY=26.7 StartZ=0 EndX=-53.5 EndY=26.7 EndZ=0
    g12: LineSegment StartX=-53.5 StartY=26.7 StartZ=0 EndX=-53.5 EndY=1.7 EndZ=0
    g13: GeomPoint [constr] X=-40 Y=14.2 Z=0
  constraints (35):
    c: Coincident(g0,g1)
    c: Coincident(g1,g2)
    c: Coincident(g2,g3)
    c: Coincident(g3,g0)
    c: Vertical(g0)
    c: Vertical(g2)
    c: Horizontal(g1)
    c: Horizontal(g3)
    c: Distance(g0,g2) = 40
    c: Distance(g1,g3) = 14.2
    c: Coincident(g0,g-1)
    c: Coincident(g4,g5)
    c: Coincident(g5,g6)
    c: Coincident(g6,g7)
    c: Coincident(g7,g4)
    c: Horizontal(g4)
    c: Horizontal(g6)
    c: Vertical(g5)
    c: Vertical(g7)
    c: Symmetric(g6,g4,g8)
    c: Distance(g5,g7) = 20.5
    c: Distance(g4,g6) = 18.5
    c: Coincident(g8,g1)
    c: Coincident(g9,g10)
    c: Coincident(g10,g11)
    c: Coincident(g11,g12)
    c: Coincident(g12,g9)
    c: Horizontal(g9)
    c: Horizontal(g11)
    c: Vertical(g10)
    c: Vertical(g12)
    c: Symmetric(g11,g9,g13)
    c: Distance(g10,g12) = 27
    c: Distance(g9,g11) = 25
    c: Coincident(g13,g1)
FEATURE [PartDesign::Pad] Pad001
  BaseFeature = -> Pocket005
  Direction = (0,0,1)
  Length = 20
  Length2 = 10
  Profile = -> Sketch007
  ReferenceAxis = -> Sketch007 [N_Axis]
  Refine = true
  Suppressed = false
  Type = 0
FEATURE [PartDesign::Chamfer] Chamfer001
  Angle = 45
  Base = -> Pad001 [Edge72,Edge73,Edge77,Edge75]
  BaseFeature = -> Pad001
  ChamferType = 0
  FlipDirection = false
  Refine = true
  Size = 3
  Size2 = 1
  SupportTransform = false
  Suppressed = false
  UseAllEdges = false
FEATURE [Sketcher::SketchObject] Sketch008
  ArcFitTolerance = 1e-06
  AttachmentSupport = -> [Chamfer001]
  FullyConstrained = true
  MakeInternals = false
  MapMode = 5
  Placement = pos=(-53.5,0,0) rot=(0.57735,-0.57735,-0.57735;2.0944rad)
  sketch-geometry (9):
    g0: LineSegment [constr] StartX=0 StartY=0 StartZ=0 EndX=0 EndY=6.2 EndZ=0
    g1: LineSegment [constr] StartX=0 StartY=6.2 StartZ=0 EndX=-26.7 EndY=6.2 EndZ=0
    g2: LineSegment [constr] StartX=-26.7 StartY=6.2 StartZ=0 EndX=-26.7 EndY=0 EndZ=0
    g3: LineSegment [constr] StartX=-26.7 StartY=0 StartZ=0 EndX=0 EndY=0 EndZ=0
    g4: LineSegment [constr] StartX=-26.7 StartY=6.2 StartZ=0 EndX=-14.2 EndY=6.2 EndZ=0
    g5: LineSegment [constr] StartX=-14.2 StartY=6.2 StartZ=0 EndX=-14.2 EndY=16.2 EndZ=0
    g6: LineSegment [constr] StartX=-14.2 StartY=16.2 StartZ=0 EndX=-26.7 EndY=16.2 EndZ=0
    g7: LineSegment [constr] StartX=-26.7 StartY=16.2 StartZ=0 EndX=-26.7 EndY=6.2 EndZ=0
    g8: Circle CenterX=-14.2 CenterY=16.2 CenterZ=0 NormalX=0 NormalY=0 NormalZ=1 AngleXU=0 Radius=1.25
  constraints (24):
    c: Coincident(g0,g1)
    c: Coincident(g1,g2)
    c: Coincident(g2,g3)
    c: Coincident(g3,g0)
    c: Vertical(g0)
    c: Vertical(g2)
    c: Horizontal(g1)
    c: Horizontal(g3)
    c: Distance(g0,g2) = 26.7
    c: Distance(g1,g3) = 6.2
    c: Coincident(g0,g-1)
    c: Coincident(g4,g5)
    c: Coincident(g5,g6)
    c: Coincident(g6,g7)
    c: Coincident(g7,g4)
    c: Horizontal(g4)
    c: Horizontal(g6)
    c: Vertical(g5)
    c: Vertical(g7)
    c: Distance(g5,g7) = 12.5
    c: Distance(g4,g6) = 10
    c: Coincident(g4,g1)
    c: Diameter(g8) = 2.5
    c: Coincident(g8,g5)
FEATURE [PartDesign::Pocket] Pocket006
  BaseFeature = -> Chamfer001
  Direction = (1,0,0)
  Length = 30
  Length2 = 5
  Profile = -> Sketch008
  ReferenceAxis = -> Sketch008 [N_Axis]
  Refine = true
  Suppressed = false
  Type = 0
FEATURE [PartDesign::Body] Body  label="ports-panel-body"
  AllowCompound = false
  Group = -> [Sketch,Pad,Sketch001,Pocket,Chamfer,Sketch002,Pocket001,Sketch003,Pocket002,Sketch004,Pocket003,Sketch005,Pocket004,Sketch006,Pocket005,Sketch007,Pad001,Chamfer001,Sketch008,Pocket006]
  Origin = -> Origin
  Tip = -> Pocket006
FEATURE [App::Part] Part  label="ports-panel-part"
  Group = -> [Body]
  Origin = -> Origin001
---- part power-supply-bracket.FCStd = doc fcstd_fb01fa926125 ----
FCSTD DOCUMENT  (FreeCAD 1.0R39285 (Git))
Label: power-supply-bracket
License: All rights reserved
LicenseURL: https://en.wikipedia.org/wiki/All_rights_reserved
objects: Sketcher::SketchObject×9, PartDesign::Pad×5, PartDesign::Chamfer×4, PartDesign::Hole×2, PartDesign::Fillet×1, PartDesign::Body×1, App::Part×1
note: 55 computed .brp shape members not serialized (recipe doc carries the construction recipe); baked Part::Feature solids carry a one-line shape summary decoded from their .brp

FEATURE [Sketcher::SketchObject] Sketch
  ArcFitTolerance = 1e-06
  AttachmentSupport = -> [XY_Plane]
  FullyConstrained = true
  MakeInternals = false
  MapMode = 5
  sketch-geometry (106):
    g0: LineSegment [constr] StartX=0 StartY=0 StartZ=0 EndX=30 EndY=0 EndZ=0
    g1: LineSegment StartX=30 StartY=0 StartZ=0 EndX=30 EndY=30 EndZ=0
    g2: LineSegment StartX=30 StartY=30 StartZ=0 EndX=0 EndY=30 EndZ=0
    g3: LineSegment [constr] StartX=0 StartY=30 StartZ=0 EndX=0 EndY=0 EndZ=0
    g4: LineSegment StartX=0 StartY=30 StartZ=0 EndX=0 EndY=34 EndZ=0
    g5: LineSegment [constr] StartX=0 StartY=34 StartZ=0 EndX=34 EndY=34 EndZ=0
    g6: LineSegment [constr] StartX=34 StartY=34 StartZ=0 EndX=34 EndY=0 EndZ=0
    g7: LineSegment [constr] StartX=34 StartY=0 StartZ=0 EndX=30 EndY=0 EndZ=0
    g8: LineSegment [constr] StartX=34 StartY=34 StartZ=0 EndX=34 EndY=64 EndZ=0
    g9: LineSegment StartX=0 StartY=34 StartZ=0 EndX=34 EndY=64 EndZ=0
    g10: LineSegment [constr] StartX=34 StartY=64 StartZ=0 EndX=34 EndY=-33 EndZ=0
    g11: LineSegment [constr] StartX=34 StartY=-33 StartZ=0 EndX=199 EndY=-33 EndZ=0
    g12: LineSegment StartX=199 StartY=-33 StartZ=0 EndX=199 EndY=64 EndZ=0
    g13: LineSegment StartX=199 StartY=64 StartZ=0 EndX=34 EndY=64 EndZ=0
    g14: LineSegment [constr] StartX=34 StartY=64 StartZ=0 EndX=34 EndY=58.5 EndZ=0
    g15: LineSegment [constr] StartX=44.5 StartY=64 StartZ=0 EndX=34 EndY=64 EndZ=0
    g16: LineSegment [constr] StartX=199 StartY=-33 StartZ=0 EndX=199 EndY=-26.5 EndZ=0
    g17: LineSegment [constr] StartX=199 StartY=-26.5 StartZ=0 EndX=196 EndY=-26.5 EndZ=0
    g18: LineSegment [constr] StartX=196 StartY=-26.5 StartZ=0 EndX=196 EndY=-33 EndZ=0
    g19: LineSegment [constr] StartX=196 StartY=-33 StartZ=0 EndX=199 EndY=-33 EndZ=0
    g20: LineSegment [constr] StartX=199 StartY=64 StartZ=0 EndX=40 EndY=64 EndZ=0
    g21: LineSegment [constr] StartX=40 StartY=64 StartZ=0 EndX=40 EndY=-33 EndZ=0
    g22: LineSegment [constr] StartX=40 StartY=-33 StartZ=0 EndX=199 EndY=-33 EndZ=0
    g23: LineSegment [constr] StartX=199 StartY=-33 StartZ=0 EndX=199 EndY=64 EndZ=0
    g24: LineSegment [constr] StartX=40 StartY=64 StartZ=0 EndX=40 EndY=58.5 EndZ=0
    g25: LineSegment [constr] StartX=40 StartY=58.5 StartZ=0 EndX=44.5 EndY=58.5 EndZ=0
    g26: LineSegment [constr] StartX=44.5 StartY=58.5 StartZ=0 EndX=44.5 EndY=64 EndZ=0
    g27: LineSegment [constr] StartX=44.5 StartY=64 StartZ=0 EndX=40 EndY=64 EndZ=0
    g28: LineSegment [constr] StartX=34 StartY=-33 StartZ=0 EndX=30 EndY=-33 EndZ=0
    g29: LineSegment StartX=30 StartY=0 StartZ=0 EndX=30 EndY=-33 EndZ=0
    g30: LineSegment StartX=30 StartY=-33 StartZ=0 EndX=30 EndY=-37 EndZ=0
    g31: LineSegment StartX=30 StartY=-37 StartZ=0 EndX=199 EndY=-37 EndZ=0
    g32: LineSegment StartX=199 StartY=-37 StartZ=0 EndX=199 EndY=-33 EndZ=0
    g33: LineSegment [constr] StartX=34 StartY=64 StartZ=0 EndX=34 EndY=49 EndZ=0
    g34: LineSegment [constr] StartX=34 StartY=49 StartZ=0 EndX=49 EndY=49 EndZ=0
    g35: LineSegment [constr] StartX=49 StartY=49 StartZ=0 EndX=49 EndY=64 EndZ=0
    g36: LineSegment [constr] StartX=49 StartY=64 StartZ=0 EndX=34 EndY=64 EndZ=0
    g37: LineSegment [constr] StartX=199 StartY=64 StartZ=0 EndX=184 EndY=64 EndZ=0
    g38: LineSegment [constr] StartX=184 StartY=64 StartZ=0 EndX=184 EndY=49 EndZ=0
    g39: LineSegment [constr] StartX=184 StartY=49 StartZ=0 EndX=199 EndY=49 EndZ=0
    g40: LineSegment [constr] StartX=199 StartY=49 StartZ=0 EndX=199 EndY=64 EndZ=0
    g41: LineSegment [constr] StartX=34 StartY=-33 StartZ=0 EndX=49 EndY=-33 EndZ=0
    g42: LineSegment [constr] StartX=49 StartY=-33 StartZ=0 EndX=49 EndY=-18 EndZ=0
    g43: LineSegment [constr] StartX=49 StartY=-18 StartZ=0 EndX=34 EndY=-18 EndZ=0
    g44: LineSegment [constr] StartX=34 StartY=-18 StartZ=0 EndX=34 EndY=-33 EndZ=0
    g45: LineSegment [constr] StartX=199 StartY=-33 StartZ=0 EndX=199 EndY=-18 EndZ=0
    g46: LineSegment [constr] StartX=199 StartY=-18 StartZ=0 EndX=184 EndY=-18 EndZ=0
    g47: LineSegment [constr] StartX=184 StartY=-18 StartZ=0 EndX=184 EndY=-33 EndZ=0
    g48: LineSegment [constr] StartX=184 StartY=-33 StartZ=0 EndX=199 EndY=-33 EndZ=0
    g49: LineSegment [constr] StartX=49 StartY=49 StartZ=0 EndX=184 EndY=-18 EndZ=0
    g50: LineSegment [constr] StartX=49 StartY=-18 StartZ=0 EndX=184 EndY=49 EndZ=0
    g51: LineSegment [constr] StartX=109 StartY=8 StartZ=0 EndX=124 EndY=8 EndZ=0
    g52: LineSegment [constr] StartX=124 StartY=8 StartZ=0 EndX=124 EndY=23 EndZ=0
    g53: LineSegment [constr] StartX=124 StartY=23 StartZ=0 EndX=109 EndY=23 EndZ=0
    g54: LineSegment [constr] StartX=109 StartY=23 StartZ=0 EndX=109 EndY=8 EndZ=0
    g55: GeomPoint [constr] X=116.5 Y=15.5 Z=0
    g56: LineSegment [constr] StartX=49 StartY=49 StartZ=0 EndX=184 EndY=49 EndZ=0
    g57: LineSegment [constr] StartX=184 StartY=49 StartZ=0 EndX=184 EndY=-18 EndZ=0
    g58: LineSegment [constr] StartX=184 StartY=-18 StartZ=0 EndX=49 EndY=-18 EndZ=0
    g59: LineSegment [constr] StartX=49 StartY=-18 StartZ=0 EndX=49 EndY=49 EndZ=0
    g60: LineSegment [constr] StartX=116.5 StartY=23 StartZ=0 EndX=49 EndY=56.5 EndZ=0
    g61: LineSegment [constr] StartX=116.5 StartY=23 StartZ=0 EndX=184 EndY=56.5 EndZ=0
    g62: LineSegment [constr] StartX=116.5 StartY=8 StartZ=0 EndX=49 EndY=-25.5 EndZ=0
    g63: LineSegment [constr] StartX=116.5 StartY=8 StartZ=0 EndX=184 EndY=-25.5 EndZ=0
    g64: LineSegment [constr] StartX=49 StartY=49 StartZ=0 EndX=64 EndY=49 EndZ=0
    g65: LineSegment [constr] StartX=49 StartY=-18 StartZ=0 EndX=64 EndY=-18 EndZ=0
    g66: LineSegment [constr] StartX=184 StartY=-18 StartZ=0 EndX=169 EndY=-18 EndZ=0
    g67: LineSegment [constr] StartX=184 StartY=49 StartZ=0 EndX=169 EndY=49 EndZ=0
    g68: LineSegment StartX=64 StartY=49 StartZ=0 EndX=116.5 EndY=23 EndZ=0
    g69: LineSegment StartX=169 StartY=49 StartZ=0 EndX=116.5 EndY=23 EndZ=0
    g70: LineSegment [constr] StartX=49 StartY=49 StartZ=0 EndX=116.5 EndY=15.5 EndZ=0
    g71: LineSegment [constr] StartX=116.5 StartY=15.5 StartZ=0 EndX=49 EndY=-18 EndZ=0
    g72: LineSegment [constr] StartX=49 StartY=49 StartZ=0 EndX=49 EndY=41.5 EndZ=0
    g73: LineSegment [constr] StartX=116.5 StartY=8 StartZ=0 EndX=49 EndY=41.5 EndZ=0
    g74: LineSegment [constr] StartX=184 StartY=49 StartZ=0 EndX=184 EndY=41.5 EndZ=0
    g75: LineSegment [constr] StartX=184 StartY=41.5 StartZ=0 EndX=116.5 EndY=8 EndZ=0
    g76: LineSegment [constr] StartX=49 StartY=-18 StartZ=0 EndX=49 EndY=-10.5 EndZ=0
    g77: LineSegment [constr] StartX=184 StartY=-18 StartZ=0 EndX=184 EndY=-10.5 EndZ=0
    g78: LineSegment [constr] StartX=184 StartY=-10.5 StartZ=0 EndX=116.5 EndY=23 EndZ=0
    g79: LineSegment [constr] StartX=116.5 StartY=23 StartZ=0 EndX=49 EndY=-10.5 EndZ=0
    g80: LineSegment StartX=64 StartY=49 StartZ=0 EndX=169 EndY=49 EndZ=0
    g81: LineSegment StartX=116.5 StartY=8 StartZ=0 EndX=64 EndY=-18 EndZ=0
    g82: LineSegment StartX=169 StartY=-18 StartZ=0 EndX=116.5 EndY=8 EndZ=0
    g83: LineSegment StartX=64 StartY=-18 StartZ=0 EndX=169 EndY=-18 EndZ=0
    g84: LineSegment [constr] StartX=116.5 StartY=15.5 StartZ=0 EndX=101.388 EndY=15.5 EndZ=0
    g85: LineSegment [constr] StartX=116.5 StartY=15.5 StartZ=0 EndX=131.612 EndY=15.5 EndZ=0
    g86: LineSegment StartX=49 StartY=41.5 StartZ=0 EndX=101.388 EndY=15.5 EndZ=0
    g87: LineSegment StartX=101.388 StartY=15.5 StartZ=0 EndX=49 EndY=-10.5 EndZ=0
    g88: LineSegment StartX=49 StartY=-10.5 StartZ=0 EndX=49 EndY=41.5 EndZ=0
    g89: LineSegment StartX=184 StartY=41.5 StartZ=0 EndX=131.612 EndY=15.5 EndZ=0
    g90: LineSegment StartX=131.612 StartY=15.5 StartZ=0 EndX=184 EndY=-10.5 EndZ=0
    g91: LineSegment StartX=184 StartY=-10.5 StartZ=0 EndX=184 EndY=41.5 EndZ=0
    g92: Circle [constr] CenterX=44.5 CenterY=58.5 CenterZ=0 NormalX=0 NormalY=0 NormalZ=1 AngleXU=0 Radius=1.75
    g93: Circle [constr] CenterX=196 CenterY=-26.5 CenterZ=0 NormalX=0 NormalY=0 NormalZ=1 AngleXU=0 Radius=1.75
    g94: LineSegment [constr] StartX=199 StartY=64 StartZ=0 EndX=194.5 EndY=64 EndZ=0
    g95: LineSegment [constr] StartX=194.5 StartY=64 StartZ=0 EndX=194.5 EndY=58.5 EndZ=0
    g96: LineSegment [constr] StartX=194.5 StartY=58.5 StartZ=0 EndX=199 EndY=58.5 EndZ=0
    g97: LineSegment [constr] StartX=199 StartY=58.5 StartZ=0 EndX=199 EndY=64 EndZ=0
    g98: Circle [constr] CenterX=194.5 CenterY=58.5 CenterZ=0 NormalX=0 NormalY=0 NormalZ=1 AngleXU=0 Radius=1.75
    g99: LineSegment [constr] StartX=194.5 StartY=58.5 StartZ=0 EndX=42 EndY=58.5 EndZ=0
    g100: LineSegment [constr] StartX=42 StartY=58.5 StartZ=0 EndX=42 EndY=-26.5 EndZ=0
    g101: Circle CenterX=42 CenterY=-26.5 CenterZ=0 NormalX=0 NormalY=0 NormalZ=1 AngleXU=0 Radius=1.75
    g102: ArcOfCircle CenterX=194.5 CenterY=58.5 CenterZ=0 NormalX=0 NormalY=0 NormalZ=1 AngleXU=0 Radius=1.75 StartAngle=4.71239 EndAngle=7.85398
    g103: ArcOfCircle CenterX=190.5 CenterY=58.5 CenterZ=0 NormalX=0 NormalY=0 NormalZ=1 AngleXU=0 Radius=1.75 StartAngle=1.5708 EndAngle=4.71239
    g104: LineSegment StartX=194.5 StartY=56.75 StartZ=0 EndX=190.5 EndY=56.75 EndZ=0
    g105: LineSegment StartX=194.5 StartY=60.25 StartZ=0 EndX=190.5 EndY=60.25 EndZ=0
  constraints (266):
    c: Coincident(g0,g1)
    c: Coincident(g1,g2)
    c: Coincident(g2,g3)
    c: Coincident(g3,g0)
    c: Horizontal(g0)
    c: Horizontal(g2)
    c: Vertical(g1)
    c: Vertical(g3)
    c: Distance(g1,g3) = 30
    c: Distance(g0,g2) = 30
    c: Coincident(g0,g-1)
    c: Distance(g4) = 4
    c: Coincident(g4,g2)
    c: PointOnObject(g4,g-2)
    c: Distance(g5) = 34
    c: Coincident(g5,g4)
    c: Horizontal(g5)
    c: Coincident(g6,g5)
    c: PointOnObject(g6,g-1)
    c: Vertical(g6)
    c: Coincident(g7,g6)
    c: Coincident(g7,g0)
    c: Distance(g8) = 30
    c: Coincident(g8,g5)
    c: Vertical(g8)
    c: Coincident(g9,g4)
    c: Coincident(g9,g8)
    c: Coincident(g10,g11)
    c: Coincident(g11,g12)
    c: Coincident(g12,g13)
    c: Coincident(g13,g10)
    c: Vertical(g10)
    c: Vertical(g12)
    c: Horizontal(g11)
    c: Horizontal(g13)
    c: Distance(g10,g12) = 165
    c: Distance(g11,g13) = 97
    c: Coincident(g10,g8)
    c: Coincident(g15,g14)
    c: Vertical(g14)
    c: Horizontal(g15)
    c: Distance(g14,g15) = 10.5
    c: Distance(g14,g15) = 5.5
    c: Coincident(g14,g8)
    c: Coincident(g16,g17)
    c: Coincident(g17,g18)
    c: Coincident(g18,g19)
    c: Coincident(g19,g16)
    c: Vertical(g16)
    c: Vertical(g18)
    c: Horizontal(g17)
    c: Horizontal(g19)
    c: Distance(g16,g18) = 3
    c: Distance(g17,g19) = 6.5
    c: Coincident(g16,g11)
    c: Coincident(g20,g21)
    c: Coincident(g21,g22)
    c: Coincident(g22,g23)
    c: Coincident(g23,g20)
    c: Horizontal(g20)
    c: Horizontal(g22)
    c: Vertical(g21)
    c: Vertical(g23)
    c: Distance(g21,g23) = 159
    c: Coincident(g20,g12)
    c: PointOnObject(g21,g11)
    c: Coincident(g24,g25)
    c: Coincident(g25,g26)
    c: Coincident(g26,g27)
    c: Coincident(g27,g24)
    c: Vertical(g24)
    c: Vertical(g26)
    c: Horizontal(g25)
    c: Horizontal(g27)
    c: Distance(g24,g26) = 4.5
    c: Distance(g25,g27) = 5.5
    c: Coincident(g24,g20)
    c: Distance(g28) = 4
    c: Coincident(g28,g10)
    c: Horizontal(g28)
    c: Coincident(g29,g0)
    c: Coincident(g29,g28)
    c: Distance(g30) = 4
    c: Coincident(g30,g28)
    c: Vertical(g30)
    c: Distance(g31) = 169
    c: Coincident(g31,g30)
    c: Horizontal(g31)
    c: Coincident(g32,g31)
    c: Coincident(g32,g11)
    c: Coincident(g33,g34)
    c: Coincident(g34,g35)
    c: Coincident(g35,g36)
    c: Coincident(g36,g33)
    c: Vertical(g33)
    c: Vertical(g35)
    c: Horizontal(g34)
    c: Horizontal(g36)
    c: Distance(g33,g35) = 15
    c: Distance(g34,g36) = 15
    c: Coincident(g33,g8)
    c: Coincident(g37,g38)
    c: Coincident(g38,g39)
    c: Coincident(g39,g40)
    c: Coincident(g40,g37)
    c: Horizontal(g37)
    c: Horizontal(g39)
    c: Vertical(g38)
    c: Vertical(g40)
    c: Distance(g38,g40) = 15
    c: Distance(g37,g39) = 15
    c: Coincident(g37,g12)
    c: Coincident(g41,g42)
    c: Coincident(g42,g43)
    c: Coincident(g43,g44)
    c: Coincident(g44,g41)
    c: Horizontal(g41)
    c: Horizontal(g43)
    c: Vertical(g42)
    c: Vertical(g44)
    c: Distance(g42,g44) = 15
    c: Distance(g41,g43) = 15
    c: Coincident(g41,g10)
    c: Coincident(g45,g46)
    c: Coincident(g46,g47)
    c: Coincident(g47,g48)
    c: Coincident(g48,g45)
    c: Vertical(g45)
    c: Vertical(g47)
    c: Horizontal(g46)
    c: Horizontal(g48)
    c: Distance(g45,g47) = 15
    c: Distance(g46,g48) = 15
    c: Coincident(g45,g11)
    c: Coincident(g49,g34)
    c: Coincident(g49,g46)
    c: Coincident(g50,g42)
    c: Coincident(g50,g38)
    c: Coincident(g51,g52)
    c: Coincident(g52,g53)
    c: Coincident(g53,g54)
    c: Coincident(g54,g51)
    c: Horizontal(g51)
    c: Horizontal(g53)
    c: Vertical(g52)
    c: Vertical(g54)
    c: Symmetric(g53,g51,g55)
    c: Distance(g52,g54) = 15
    c: Distance(g51,g53) = 15
    c: Symmetric(g49,g49,g55)
    c: Coincident(g56,g34)
    c: Coincident(g56,g38)
    c: Coincident(g57,g38)
    c: Coincident(g57,g46)
    c: Coincident(g58,g46)
    c: Coincident(g58,g42)
    c: Coincident(g59,g42)
    c: Coincident(g59,g34)
    c: Symmetric(g53,g53,g60)
    c: Symmetric(g35,g35,g60)
    c: Coincident(g61,g60)
    c: Symmetric(g38,g38,g61)
    c: Symmetric(g51,g51,g62)
    c: Symmetric(g42,g42,g62)
    c: Coincident(g63,g62)
    c: Symmetric(g47,g47,g63)
    c: Distance(g64) = 15
    c: Coincident(g64,g34)
    c: PointOnObject(g64,g56)
    c: Distance(g65) = 15
    c: Coincident(g65,g42)
    c: PointOnObject(g65,g58)
    c: Distance(g66) = 15
    c: Coincident(g66,g46)
    c: PointOnObject(g66,g58)
    c: Distance(g67) = 15
    c: Coincident(g67,g38)
    c: PointOnObject(g67,g56)
    c: Coincident(g68,g64)
    c: Coincident(g68,g60)
    c: Coincident(g69,g67)
    c: Coincident(g69,g60)
    c: Coincident(g70,g34)
    c: Coincident(g70,g55)
    c: Coincident(g71,g55)
    c: Coincident(g71,g42)
    c: Distance(g72) = 7.5
    c: Coincident(g72,g34)
    c: PointOnObject(g72,g59)
    c: Coincident(g73,g62)
    c: Coincident(g73,g72)
    c: Distance(g74) = 7.5
    c: Coincident(g74,g38)
    c: PointOnObject(g74,g57)
    c: Coincident(g75,g74)
    c: Coincident(g75,g62)
    c: Distance(g76) = 7.5
    c: Coincident(g76,g42)
    c: PointOnObject(g76,g59)
    c: Distance(g77) = 7.5
    c: Coincident(g77,g46)
    c: PointOnObject(g77,g57)
    c: Coincident(g78,g77)
    c: Coincident(g78,g60)
    c: Coincident(g79,g60)
    c: Coincident(g79,g76)
    c: Coincident(g80,g64)
    c: Coincident(g80,g67)
    c: Coincident(g81,g62)
    c: Coincident(g81,g65)
    c: Coincident(g82,g66)
    c: Coincident(g82,g62)
    c: Coincident(g83,g65)
    c: Coincident(g83,g66)
    c: Coincident(g84,g55)
    c: PointOnObject(g84,g73)
    c: Horizontal(g84)
    c: Coincident(g85,g55)
    c: PointOnObject(g85,g75)
    c: Horizontal(g85)
    c: Coincident(g86,g72)
    c: Coincident(g86,g84)
    c: Coincident(g87,g84)
    c: Coincident(g87,g76)
    c: Coincident(g88,g76)
    c: Coincident(g88,g72)
    c: Coincident(g89,g74)
    c: Coincident(g89,g85)
    c: Coincident(g90,g85)
    c: Coincident(g90,g77)
    c: Coincident(g91,g77)
    c: Coincident(g91,g74)
    c: Diameter(g92) = 3.5
    c: Coincident(g92,g25)
    c: Diameter(g93) = 3.5
    c: Coincident(g93,g17)
    c: Coincident(g94,g95)
    c: Coincident(g95,g96)
    c: Coincident(g96,g97)
    c: Coincident(g97,g94)
    c: Horizontal(g94)
    c: Horizontal(g96)
    c: Vertical(g95)
    c: Vertical(g97)
    c: Distance(g95,g97) = 4.5
    c: Distance(g94,g96) = 5.5
    c: Coincident(g94,g12)
    c: Diameter(g98) = 3.5
    c: Coincident(g98,g95)
    c: Distance(g99) = 152.5
    c: Coincident(g99,g95)
    c: PointOnObject(g99,g25)
    c: Distance(g100) = 85
    c: Coincident(g100,g99)
    c: Vertical(g100)
    c: Diameter(g101) = 3.5
    c: Coincident(g101,g100)
    c: Tangent(g102,g104) = 1.5708
    c: Tangent(g102,g105) = -1.5708
    c: Tangent(g103,g104) = 1.5708
    c: Tangent(g103,g105) = -1.5708
    c: Equal(g102,g103)
    c: Horizontal(g105)
    c: Distance(g102,g103) = 4
    c: Radius(g102) = 1.75
    c: Coincident(g102,g95)
FEATURE [PartDesign::Pad] Pad
  Direction = (0,0,1)
  Length = 4
  Length2 = 10
  Profile = -> Sketch
  ReferenceAxis = -> Sketch [N_Axis]
  Refine = true
  Suppressed = false
  Type = 0
FEATURE [Sketcher::SketchObject] Sketch001
  ArcFitTolerance = 1e-06
  AttachmentSupport = -> [Pad]
  FullyConstrained = true
  MakeInternals = false
  MapMode = 5
  Placement = pos=(0,0,4) rot=(0,0,1;0rad)
  sketch-geometry (96):
    g0: LineSegment [constr] StartX=0 StartY=0 StartZ=0 EndX=30 EndY=0 EndZ=0
    g1: LineSegment StartX=30 StartY=0 StartZ=0 EndX=30 EndY=30 EndZ=0
    g2: LineSegment StartX=30 StartY=30 StartZ=0 EndX=0 EndY=30 EndZ=0
    g3: LineSegment [constr] StartX=0 StartY=30 StartZ=0 EndX=0 EndY=0 EndZ=0
    g4: LineSegment StartX=0 StartY=30 StartZ=0 EndX=0 EndY=34 EndZ=0
    g5: LineSegment [constr] StartX=0 StartY=34 StartZ=0 EndX=34 EndY=34 EndZ=0
    g6: LineSegment [constr] StartX=34 StartY=34 StartZ=0 EndX=34 EndY=0 EndZ=0
    g7: LineSegment [constr] StartX=34 StartY=0 StartZ=0 EndX=30 EndY=0 EndZ=0
    g8: LineSegment [constr] StartX=34 StartY=34 StartZ=0 EndX=34 EndY=64 EndZ=0
    g9: LineSegment [constr] StartX=0 StartY=34 StartZ=0 EndX=34 EndY=64 EndZ=0
    g10: LineSegment [constr] StartX=34 StartY=64 StartZ=0 EndX=34 EndY=-33 EndZ=0
    g11: LineSegment [constr] StartX=34 StartY=-33 StartZ=0 EndX=199 EndY=-33 EndZ=0
    g12: LineSegment [constr] StartX=199 StartY=-33 StartZ=0 EndX=199 EndY=64 EndZ=0
    g13: LineSegment [constr] StartX=199 StartY=64 StartZ=0 EndX=34 EndY=64 EndZ=0
    g14: LineSegment [constr] StartX=34 StartY=64 StartZ=0 EndX=34 EndY=58.5 EndZ=0
    g15: LineSegment [constr] StartX=44.5 StartY=64 StartZ=0 EndX=34 EndY=64 EndZ=0
    g16: LineSegment [constr] StartX=199 StartY=-33 StartZ=0 EndX=199 EndY=-26.5 EndZ=0
    g17: LineSegment [constr] StartX=199 StartY=-26.5 StartZ=0 EndX=196 EndY=-26.5 EndZ=0
    g18: LineSegment [constr] StartX=196 StartY=-26.5 StartZ=0 EndX=196 EndY=-33 EndZ=0
    g19: LineSegment [constr] StartX=196 StartY=-33 StartZ=0 EndX=199 EndY=-33 EndZ=0
    g20: LineSegment [constr] StartX=199 StartY=64 StartZ=0 EndX=40 EndY=64 EndZ=0
    g21: LineSegment [constr] StartX=40 StartY=64 StartZ=0 EndX=40 EndY=-33 EndZ=0
    g22: LineSegment [constr] StartX=40 StartY=-33 StartZ=0 EndX=199 EndY=-33 EndZ=0
    g23: LineSegment [constr] StartX=199 StartY=-33 StartZ=0 EndX=199 EndY=64 EndZ=0
    g24: LineSegment [constr] StartX=40 StartY=64 StartZ=0 EndX=40 EndY=58.5 EndZ=0
    g25: LineSegment [constr] StartX=40 StartY=58.5 StartZ=0 EndX=44.5 EndY=58.5 EndZ=0
    g26: LineSegment [constr] StartX=44.5 StartY=58.5 StartZ=0 EndX=44.5 EndY=64 EndZ=0
    g27: LineSegment [constr] StartX=44.5 StartY=64 StartZ=0 EndX=40 EndY=64 EndZ=0
    g28: LineSegment [constr] StartX=34 StartY=-33 StartZ=0 EndX=30 EndY=-33 EndZ=0
    g29: LineSegment StartX=30 StartY=0 StartZ=0 EndX=30 EndY=-33 EndZ=0
    g30: LineSegment StartX=30 StartY=-33 StartZ=0 EndX=30 EndY=-37 EndZ=0
    g31: LineSegment StartX=30 StartY=-37 StartZ=0 EndX=199 EndY=-37 EndZ=0
    g32: LineSegment [constr] StartX=199 StartY=-37 StartZ=0 EndX=199 EndY=-33 EndZ=0
    g33: LineSegment [constr] StartX=34 StartY=64 StartZ=0 EndX=34 EndY=49 EndZ=0
    g34: LineSegment [constr] StartX=34 StartY=49 StartZ=0 EndX=49 EndY=49 EndZ=0
    g35: LineSegment [constr] StartX=49 StartY=49 StartZ=0 EndX=49 EndY=64 EndZ=0
    g36: LineSegment [constr] StartX=49 StartY=64 StartZ=0 EndX=34 EndY=64 EndZ=0
    g37: LineSegment [constr] StartX=199 StartY=64 StartZ=0 EndX=184 EndY=64 EndZ=0
    g38: LineSegment [constr] StartX=184 StartY=64 StartZ=0 EndX=184 EndY=49 EndZ=0
    g39: LineSegment [constr] StartX=184 StartY=49 StartZ=0 EndX=199 EndY=49 EndZ=0
    g40: LineSegment [constr] StartX=199 StartY=49 StartZ=0 EndX=199 EndY=64 EndZ=0
    g41: LineSegment [constr] StartX=34 StartY=-33 StartZ=0 EndX=49 EndY=-33 EndZ=0
    g42: LineSegment [constr] StartX=49 StartY=-33 StartZ=0 EndX=49 EndY=-18 EndZ=0
    g43: LineSegment [constr] StartX=49 StartY=-18 StartZ=0 EndX=34 EndY=-18 EndZ=0
    g44: LineSegment [constr] StartX=34 StartY=-18 StartZ=0 EndX=34 EndY=-33 EndZ=0
    g45: LineSegment [constr] StartX=199 StartY=-33 StartZ=0 EndX=199 EndY=-18 EndZ=0
    g46: LineSegment [constr] StartX=199 StartY=-18 StartZ=0 EndX=184 EndY=-18 EndZ=0
    g47: LineSegment [constr] StartX=184 StartY=-18 StartZ=0 EndX=184 EndY=-33 EndZ=0
    g48: LineSegment [constr] StartX=184 StartY=-33 StartZ=0 EndX=199 EndY=-33 EndZ=0
    g49: LineSegment [constr] StartX=49 StartY=49 StartZ=0 EndX=184 EndY=-18 EndZ=0
    g50: LineSegment [constr] StartX=49 StartY=-18 StartZ=0 EndX=184 EndY=49 EndZ=0
    g51: LineSegment [constr] StartX=109 StartY=8 StartZ=0 EndX=124 EndY=8 EndZ=0
    g52: LineSegment [constr] StartX=124 StartY=8 StartZ=0 EndX=124 EndY=23 EndZ=0
    g53: LineSegment [constr] StartX=124 StartY=23 StartZ=0 EndX=109 EndY=23 EndZ=0
    g54: LineSegment [constr] StartX=109 StartY=23 StartZ=0 EndX=109 EndY=8 EndZ=0
    g55: GeomPoint [constr] X=116.5 Y=15.5 Z=0
    g56: LineSegment [constr] StartX=49 StartY=49 StartZ=0 EndX=184 EndY=49 EndZ=0
    g57: LineSegment [constr] StartX=184 StartY=49 StartZ=0 EndX=184 EndY=-18 EndZ=0
    g58: LineSegment [constr] StartX=184 StartY=-18 StartZ=0 EndX=49 EndY=-18 EndZ=0
    g59: LineSegment [constr] StartX=49 StartY=-18 StartZ=0 EndX=49 EndY=49 EndZ=0
    g60: LineSegment [constr] StartX=116.5 StartY=23 StartZ=0 EndX=49 EndY=56.5 EndZ=0
    g61: LineSegment [constr] StartX=116.5 StartY=23 StartZ=0 EndX=184 EndY=56.5 EndZ=0
    g62: LineSegment [constr] StartX=116.5 StartY=8 StartZ=0 EndX=49 EndY=-25.5 EndZ=0
    g63: LineSegment [constr] StartX=116.5 StartY=8 StartZ=0 EndX=184 EndY=-25.5 EndZ=0
    g64: LineSegment [constr] StartX=49 StartY=49 StartZ=0 EndX=64 EndY=49 EndZ=0
    g65: LineSegment [constr] StartX=49 StartY=-18 StartZ=0 EndX=64 EndY=-18 EndZ=0
    g66: LineSegment [constr] StartX=184 StartY=-18 StartZ=0 EndX=169 EndY=-18 EndZ=0
    g67: LineSegment [constr] StartX=184 StartY=49 StartZ=0 EndX=169 EndY=49 EndZ=0
    g68: LineSegment [constr] StartX=64 StartY=49 StartZ=0 EndX=116.5 EndY=23 EndZ=0
    g69: LineSegment [constr] StartX=169 StartY=49 StartZ=0 EndX=116.5 EndY=23 EndZ=0
    g70: LineSegment [constr] StartX=49 StartY=49 StartZ=0 EndX=116.5 EndY=15.5 EndZ=0
    g71: LineSegment [constr] StartX=116.5 StartY=15.5 StartZ=0 EndX=49 EndY=-18 EndZ=0
    g72: LineSegment [constr] StartX=49 StartY=49 StartZ=0 EndX=49 EndY=41.5 EndZ=0
    g73: LineSegment [constr] StartX=116.5 StartY=8 StartZ=0 EndX=49 EndY=41.5 EndZ=0
    g74: LineSegment [constr] StartX=184 StartY=49 StartZ=0 EndX=184 EndY=41.5 EndZ=0
    g75: LineSegment [constr] StartX=184 StartY=41.5 StartZ=0 EndX=116.5 EndY=8 EndZ=0
    g76: LineSegment [constr] StartX=49 StartY=-18 StartZ=0 EndX=49 EndY=-10.5 EndZ=0
    g77: LineSegment [constr] StartX=184 StartY=-18 StartZ=0 EndX=184 EndY=-10.5 EndZ=0
    g78: LineSegment [constr] StartX=184 StartY=-10.5 StartZ=0 EndX=116.5 EndY=23 EndZ=0
    g79: LineSegment [constr] StartX=116.5 StartY=23 StartZ=0 EndX=49 EndY=-10.5 EndZ=0
    g80: LineSegment [constr] StartX=64 StartY=49 StartZ=0 EndX=169 EndY=49 EndZ=0
    g81: LineSegment [constr] StartX=116.5 StartY=8 StartZ=0 EndX=64 EndY=-18 EndZ=0
    g82: LineSegment [constr] StartX=169 StartY=-18 StartZ=0 EndX=116.5 EndY=8 EndZ=0
    g83: LineSegment [constr] StartX=64 StartY=-18 StartZ=0 EndX=169 EndY=-18 EndZ=0
    g84: LineSegment [constr] StartX=116.5 StartY=15.5 StartZ=0 EndX=101.388 EndY=15.5 EndZ=0
    g85: LineSegment [constr] StartX=116.5 StartY=15.5 StartZ=0 EndX=131.612 EndY=15.5 EndZ=0
    g86: LineSegment [constr] StartX=49 StartY=41.5 StartZ=0 EndX=101.388 EndY=15.5 EndZ=0
    g87: LineSegment [constr] StartX=101.388 StartY=15.5 StartZ=0 EndX=49 EndY=-10.5 EndZ=0
    g88: LineSegment [constr] StartX=49 StartY=-10.5 StartZ=0 EndX=49 EndY=41.5 EndZ=0
    g89: LineSegment [constr] StartX=184 StartY=41.5 StartZ=0 EndX=131.612 EndY=15.5 EndZ=0
    g90: LineSegment [constr] StartX=131.612 StartY=15.5 StartZ=0 EndX=184 EndY=-10.5 EndZ=0
    g91: LineSegment [constr] StartX=184 StartY=-10.5 StartZ=0 EndX=184 EndY=41.5 EndZ=0
    g92: LineSegment StartX=0 StartY=34 StartZ=0 EndX=34 EndY=34 EndZ=0
    g93: LineSegment StartX=34 StartY=34 StartZ=0 EndX=34 EndY=-33 EndZ=0
    g94: LineSegment StartX=199 StartY=-33 StartZ=0 EndX=34 EndY=-33 EndZ=0
    g95: LineSegment StartX=199 StartY=-33 StartZ=0 EndX=199 EndY=-37 EndZ=0
  constraints (240):
    c: Coincident(g0,g1)
    c: Coincident(g1,g2)
    c: Coincident(g2,g3)
    c: Coincident(g3,g0)
    c: Horizontal(g0)
    c: Horizontal(g2)
    c: Vertical(g1)
    c: Vertical(g3)
    c: Distance(g1,g3) = 30
    c: Distance(g0,g2) = 30
    c: Coincident(g0,g-1)
    c: Distance(g4) = 4
    c: Coincident(g4,g2)
    c: PointOnObject(g4,g-2)
    c: Distance(g5) = 34
    c: Coincident(g5,g4)
    c: Horizontal(g5)
    c: Coincident(g6,g5)
    c: PointOnObject(g6,g-1)
    c: Vertical(g6)
    c: Coincident(g7,g6)
    c: Coincident(g7,g0)
    c: Distance(g8) = 30
    c: Coincident(g8,g5)
    c: Vertical(g8)
    c: Coincident(g9,g4)
    c: Coincident(g9,g8)
    c: Coincident(g10,g11)
    c: Coincident(g11,g12)
    c: Coincident(g12,g13)
    c: Coincident(g13,g10)
    c: Vertical(g10)
    c: Vertical(g12)
    c: Horizontal(g11)
    c: Horizontal(g13)
    c: Distance(g10,g12) = 165
    c: Distance(g11,g13) = 97
    c: Coincident(g10,g8)
    c: Coincident(g15,g14)
    c: Vertical(g14)
    c: Horizontal(g15)
    c: Distance(g14,g15) = 10.5
    c: Distance(g14,g15) = 5.5
    c: Coincident(g14,g8)
    c: Coincident(g16,g17)
    c: Coincident(g17,g18)
    c: Coincident(g18,g19)
    c: Coincident(g19,g16)
    c: Vertical(g16)
    c: Vertical(g18)
    c: Horizontal(g17)
    c: Horizontal(g19)
    c: Distance(g16,g18) = 3
    c: Distance(g17,g19) = 6.5
    c: Coincident(g16,g11)
    c: Coincident(g20,g21)
    c: Coincident(g21,g22)
    c: Coincident(g22,g23)
    c: Coincident(g23,g20)
    c: Horizontal(g20)
    c: Horizontal(g22)
    c: Vertical(g21)
    c: Vertical(g23)
    c: Distance(g21,g23) = 159
    c: Coincident(g20,g12)
    c: PointOnObject(g21,g11)
    c: Coincident(g24,g25)
    c: Coincident(g25,g26)
    c: Coincident(g26,g27)
    c: Coincident(g27,g24)
    c: Vertical(g24)
    c: Vertical(g26)
    c: Horizontal(g25)
    c: Horizontal(g27)
    c: Distance(g24,g26) = 4.5
    c: Distance(g25,g27) = 5.5
    c: Coincident(g24,g20)
    c: Distance(g28) = 4
    c: Coincident(g28,g10)
    c: Horizontal(g28)
    c: Coincident(g29,g0)
    c: Coincident(g29,g28)
    c: Distance(g30) = 4
    c: Coincident(g30,g28)
    c: Vertical(g30)
    c: Distance(g31) = 169
    c: Coincident(g31,g30)
    c: Horizontal(g31)
    c: Coincident(g32,g31)
    c: Coincident(g32,g11)
    c: Coincident(g33,g34)
    c: Coincident(g34,g35)
    c: Coincident(g35,g36)
    c: Coincident(g36,g33)
    c: Vertical(g33)
    c: Vertical(g35)
    c: Horizontal(g34)
    c: Horizontal(g36)
    c: Distance(g33,g35) = 15
    c: Distance(g34,g36) = 15
    c: Coincident(g33,g8)
    c: Coincident(g37,g38)
    c: Coincident(g38,g39)
    c: Coincident(g39,g40)
    c: Coincident(g40,g37)
    c: Horizontal(g37)
    c: Horizontal(g39)
    c: Vertical(g38)
    c: Vertical(g40)
    c: Distance(g38,g40) = 15
    c: Distance(g37,g39) = 15
    c: Coincident(g37,g12)
    c: Coincident(g41,g42)
    c: Coincident(g42,g43)
    c: Coincident(g43,g44)
    c: Coincident(g44,g41)
    c: Horizontal(g41)
    c: Horizontal(g43)
    c: Vertical(g42)
    c: Vertical(g44)
    c: Distance(g42,g44) = 15
    c: Distance(g41,g43) = 15
    c: Coincident(g41,g10)
    c: Coincident(g45,g46)
    c: Coincident(g46,g47)
    c: Coincident(g47,g48)
    c: Coincident(g48,g45)
    c: Vertical(g45)
    c: Vertical(g47)
    c: Horizontal(g46)
    c: Horizontal(g48)
    c: Distance(g45,g47) = 15
    c: Distance(g46,g48) = 15
    c: Coincident(g45,g11)
    c: Coincident(g49,g34)
    c: Coincident(g49,g46)
    c: Coincident(g50,g42)
    c: Coincident(g50,g38)
    c: Coincident(g51,g52)
    c: Coincident(g52,g53)
    c: Coincident(g53,g54)
    c: Coincident(g54,g51)
    c: Horizontal(g51)
    c: Horizontal(g53)
    c: Vertical(g52)
    c: Vertical(g54)
    c: Symmetric(g53,g51,g55)
    c: Distance(g52,g54) = 15
    c: Distance(g51,g53) = 15
    c: Symmetric(g49,g49,g55)
    c: Coincident(g56,g34)
    c: Coincident(g56,g38)
    c: Coincident(g57,g38)
    c: Coincident(g57,g46)
    c: Coincident(g58,g46)
    c: Coincident(g58,g42)
    c: Coincident(g59,g42)
    c: Coincident(g59,g34)
    c: Symmetric(g53,g53,g60)
    c: Symmetric(g35,g35,g60)
    c: Coincident(g61,g60)
    c: Symmetric(g38,g38,g61)
    c: Symmetric(g51,g51,g62)
    c: Symmetric(g42,g42,g62)
    c: Coincident(g63,g62)
    c: Symmetric(g47,g47,g63)
    c: Distance(g64) = 15
    c: Coincident(g64,g34)
    c: PointOnObject(g64,g56)
    c: Distance(g65) = 15
    c: Coincident(g65,g42)
    c: PointOnObject(g65,g58)
    c: Distance(g66) = 15
    c: Coincident(g66,g46)
    c: PointOnObject(g66,g58)
    c: Distance(g67) = 15
    c: Coincident(g67,g38)
    c: PointOnObject(g67,g56)
    c: Coincident(g68,g64)
    c: Coincident(g68,g60)
    c: Coincident(g69,g67)
    c: Coincident(g69,g60)
    c: Coincident(g70,g34)
    c: Coincident(g70,g55)
    c: Coincident(g71,g55)
    c: Coincident(g71,g42)
    c: Distance(g72) = 7.5
    c: Coincident(g72,g34)
    c: PointOnObject(g72,g59)
    c: Coincident(g73,g62)
    c: Coincident(g73,g72)
    c: Distance(g74) = 7.5
    c: Coincident(g74,g38)
    c: PointOnObject(g74,g57)
    c: Coincident(g75,g74)
    c: Coincident(g75,g62)
    c: Distance(g76) = 7.5
    c: Coincident(g76,g42)
    c: PointOnObject(g76,g59)
    c: Distance(g77) = 7.5
    c: Coincident(g77,g46)
    c: PointOnObject(g77,g57)
    c: Coincident(g78,g77)
    c: Coincident(g78,g60)
    c: Coincident(g79,g60)
    c: Coincident(g79,g76)
    c: Coincident(g80,g64)
    c: Coincident(g80,g67)
    c: Coincident(g81,g62)
    c: Coincident(g81,g65)
    c: Coincident(g82,g66)
    c: Coincident(g82,g62)
    c: Coincident(g83,g65)
    c: Coincident(g83,g66)
    c: Coincident(g84,g55)
    c: PointOnObject(g84,g73)
    c: Horizontal(g84)
    c: Coincident(g85,g55)
    c: PointOnObject(g85,g75)
    c: Horizontal(g85)
    c: Coincident(g86,g72)
    c: Coincident(g86,g84)
    c: Coincident(g87,g84)
    c: Coincident(g87,g76)
    c: Coincident(g88,g76)
    c: Coincident(g88,g72)
    c: Coincident(g89,g74)
    c: Coincident(g89,g85)
    c: Coincident(g90,g85)
    c: Coincident(g90,g77)
    c: Coincident(g91,g77)
    c: Coincident(g91,g74)
    c: Coincident(g92,g4)
    c: Coincident(g92,g5)
    c: Coincident(g93,g5)
    c: Coincident(g93,g10)
    c: Coincident(g94,g11)
    c: Coincident(g94,g10)
    c: Coincident(g95,g11)
    c: Coincident(g95,g31)
FEATURE [PartDesign::Pad] Pad001
  BaseFeature = -> Pad
  Direction = (0,0,1)
  Length = 34
  Length2 = 10
  Profile = -> Sketch001
  ReferenceAxis = -> Sketch001 [N_Axis]
  Refine = true
  Reversed = true
  Suppressed = false
  Type = 0
FEATURE [PartDesign::Fillet] Fillet
  Base = -> Pad001 [Edge43,Edge44,Edge46,Edge50,Edge49,Edge52,Edge58,Edge61,Edge62,Edge56,Edge55,Edge64]
  BaseFeature = -> Pad001
  Radius = 3
  Refine = true
  SupportTransform = false
  Suppressed = false
  UseAllEdges = false
FEATURE [Sketcher::SketchObject] Sketch004
  ArcFitTolerance = 1e-06
  FullyConstrained = true
  MakeInternals = false
  MapMode = 5
  Placement = pos=(0,64,0) rot=(0,0.707107,0.707107;3.14159rad)
  sketch-geometry (10):
    g0: LineSegment [constr] StartX=0 StartY=0 StartZ=0 EndX=0 EndY=4 EndZ=0
    g1: LineSegment [constr] StartX=0 StartY=4 StartZ=0 EndX=-30 EndY=4 EndZ=0
    g2: LineSegment [constr] StartX=-30 StartY=4 StartZ=0 EndX=-30 EndY=0 EndZ=0
    g3: LineSegment [constr] StartX=-30 StartY=0 StartZ=0 EndX=0 EndY=0 EndZ=0
    g4: LineSegment [constr] StartX=0 StartY=4 StartZ=0 EndX=0 EndY=34 EndZ=0
    g5: LineSegment [constr] StartX=0 StartY=34 StartZ=0 EndX=-30 EndY=34 EndZ=0
    g6: LineSegment [constr] StartX=-30 StartY=34 StartZ=0 EndX=-30 EndY=4 EndZ=0
    g7: LineSegment [constr] StartX=-30 StartY=4 StartZ=0 EndX=0 EndY=4 EndZ=0
    g8: LineSegment [constr] StartX=-30 StartY=34 StartZ=0 EndX=-1.6e-15 EndY=4 EndZ=0
    g9: Circle CenterX=-15 CenterY=19 CenterZ=0 NormalX=0 NormalY=0 NormalZ=1 AngleXU=0 Radius=2.5
  constraints (26):
    c: Coincident(g0,g1)
    c: Coincident(g1,g2)
    c: Coincident(g2,g3)
    c: Coincident(g3,g0)
    c: Vertical(g0)
    c: Vertical(g2)
    c: Horizontal(g1)
    c: Horizontal(g3)
    c: Distance(g0,g2) = 30
    c: Distance(g1,g3) = 4
    c: Coincident(g0,g-1)
    c: Coincident(g4,g5)
    c: Coincident(g5,g6)
    c: Coincident(g6,g7)
    c: Coincident(g7,g4)
    c: Vertical(g4)
    c: Vertical(g6)
    c: Horizontal(g5)
    c: Horizontal(g7)
    c: Distance(g4,g6) = 30
    c: Distance(g5,g7) = 30
    c: Coincident(g4,g0)
    c: Coincident(g8,g5)
    c: Coincident(g8,g0)
    c: Diameter(g9) = 5
    c: Symmetric(g8,g8,g9)
FEATURE [Sketcher::SketchObject] Sketch005
  ArcFitTolerance = 1e-06
  AttachmentSupport = -> [Pad001]
  FullyConstrained = true
  MakeInternals = false
  MapMode = 5
  Placement = pos=(0,0,0) rot=(1,0,0;3.14159rad)
FEATURE [PartDesign::Chamfer] Chamfer
  Angle = 45
  Base = -> Fillet [Edge51]
  BaseFeature = -> Fillet
  ChamferType = 0
  FlipDirection = false
  Refine = true
  Size = 3
  Size2 = 1
  SupportTransform = false
  Suppressed = false
  UseAllEdges = false
FEATURE [Sketcher::SketchObject] Sketch006
  ArcFitTolerance = 1e-06
  AttachmentSupport = -> [Chamfer]
  FullyConstrained = true
  MakeInternals = false
  MapMode = 5
  Placement = pos=(0,34,0) rot=(0,0.707107,0.707107;3.14159rad)
  sketch-geometry (10):
    g0: LineSegment [constr] StartX=0 StartY=0 StartZ=0 EndX=-34 EndY=0 EndZ=0
    g1: LineSegment [constr] StartX=-34 StartY=0 StartZ=0 EndX=-34 EndY=-30 EndZ=0
    g2: LineSegment [constr] StartX=-34 StartY=-30 StartZ=0 EndX=0 EndY=-30 EndZ=0
    g3: LineSegment [constr] StartX=0 StartY=-30 StartZ=0 EndX=0 EndY=0 EndZ=0
    g4: LineSegment [constr] StartX=-34 StartY=0 StartZ=0 EndX=-34 EndY=-30 EndZ=0
    g5: LineSegment [constr] StartX=-34 StartY=-30 StartZ=0 EndX=-30 EndY=-30 EndZ=0
    g6: LineSegment [constr] StartX=-30 StartY=-30 StartZ=0 EndX=-30 EndY=0 EndZ=0
    g7: LineSegment [constr] StartX=-30 StartY=0 StartZ=0 EndX=-34 EndY=0 EndZ=0
    g8: LineSegment [constr] StartX=-30 StartY=0 StartZ=0 EndX=-1.6e-15 EndY=-30 EndZ=0
    g9: Circle CenterX=-15 CenterY=-15 CenterZ=0 NormalX=0 NormalY=0 NormalZ=1 AngleXU=0 Radius=2.75
  constraints (26):
    c: Coincident(g0,g1)
    c: Coincident(g1,g2)
    c: Coincident(g2,g3)
    c: Coincident(g3,g0)
    c: Horizontal(g0)
    c: Horizontal(g2)
    c: Vertical(g1)
    c: Vertical(g3)
    c: Distance(g1,g3) = 34
    c: Distance(g0,g2) = 30
    c: Coincident(g0,g-1)
    c: Coincident(g4,g5)
    c: Coincident(g5,g6)
    c: Coincident(g6,g7)
    c: Coincident(g7,g4)
    c: Vertical(g4)
    c: Vertical(g6)
    c: Horizontal(g5)
    c: Horizontal(g7)
    c: Distance(g4,g6) = 4
    c: Coincident(g4,g0)
    c: PointOnObject(g5,g2)
    c: Coincident(g8,g6)
    c: Coincident(g8,g2)
    c: Diameter(g9) = 5.5
    c: Symmetric(g8,g8,g9)
FEATURE [PartDesign::Hole] Hole
  BaseFeature = -> Chamfer
  CustomThreadClearance = 0
  Depth = 25
  DepthType = 0
  Diameter = 5.8
  DrillForDepth = false
  DrillPoint = 1
  DrillPointAngle = 118
  HoleCutCountersinkAngle = 90
  HoleCutCustomValues = false
  HoleCutDepth = 0
  HoleCutDiameter = 6.1
  HoleCutType = 0
  ModelThread = false
  Profile = -> Sketch006
  Refine = true
  Suppressed = false
  Tapered = false
  TaperedAngle = 90
  ThreadClass = 0
  ThreadDepth = 25
  ThreadDepthType = 0
  ThreadDirection = 0
  ThreadFit = 2
  ThreadSize = 13
  ThreadType = 1
  Threaded = false
  UseCustomThreadClearance = false
FEATURE [Sketcher::SketchObject] Sketch007
  ArcFitTolerance = 1e-06
  AttachmentSupport = -> [Hole]
  FullyConstrained = true
  MakeInternals = false
  MapMode = 5
  Placement = pos=(0,-33,0) rot=(0,0.707107,0.707107;3.14159rad)
  sketch-geometry (16):
    g0: LineSegment [constr] StartX=0 StartY=0 StartZ=0 EndX=-34 EndY=0 EndZ=0
    g1: LineSegment [constr] StartX=-34 StartY=0 StartZ=0 EndX=-34 EndY=-26 EndZ=0
    g2: LineSegment [constr] StartX=-34 StartY=-26 StartZ=0 EndX=0 EndY=-26 EndZ=0
    g3: LineSegment [constr] StartX=0 StartY=-26 StartZ=0 EndX=0 EndY=0 EndZ=0
    g4: LineSegment [constr] StartX=-34 StartY=0 StartZ=0 EndX=-199 EndY=0 EndZ=0
    g5: LineSegment [constr] StartX=-199 StartY=0 StartZ=0 EndX=-199 EndY=-30 EndZ=0
    g6: LineSegment [constr] StartX=-199 StartY=-30 StartZ=0 EndX=-34 EndY=-30 EndZ=0
    g7: LineSegment [constr] StartX=-34 StartY=-30 StartZ=0 EndX=-34 EndY=0 EndZ=0
    g8: LineSegment [constr] StartX=-199 StartY=0 StartZ=0 EndX=-177 EndY=0 EndZ=0
    g9: LineSegment [constr] StartX=-177 StartY=0 StartZ=0 EndX=-60 EndY=0 EndZ=0
    g10: LineSegment [constr] StartX=-177 StartY=0 StartZ=0 EndX=-177 EndY=-15 EndZ=0
    g11: LineSegment [constr] StartX=-60 StartY=0 StartZ=0 EndX=-60 EndY=-6 EndZ=0
    g12: LineSegment [constr] StartX=-60 StartY=-6 StartZ=0 EndX=-60 EndY=-24 EndZ=0
    g13: Circle CenterX=-177 CenterY=-15 CenterZ=0 NormalX=0 NormalY=0 NormalZ=1 AngleXU=0 Radius=1.5
    g14: Circle CenterX=-60 CenterY=-6 CenterZ=0 NormalX=0 NormalY=0 NormalZ=1 AngleXU=0 Radius=1.5
    g15: Circle CenterX=-60 CenterY=-24 CenterZ=0 NormalX=0 NormalY=0 NormalZ=1 AngleXU=0 Radius=1.5
  constraints (43):
    c: Coincident(g0,g1)
    c: Coincident(g1,g2)
    c: Coincident(g2,g3)
    c: Coincident(g3,g0)
    c: Horizontal(g0)
    c: Horizontal(g2)
    c: Vertical(g1)
    c: Vertical(g3)
    c: Distance(g1,g3) = 34
    c: Distance(g0,g2) = 26
    c: Coincident(g0,g-1)
    c: Coincident(g4,g5)
    c: Coincident(g5,g6)
    c: Coincident(g6,g7)
    c: Coincident(g7,g4)
    c: Horizontal(g4)
    c: Horizontal(g6)
    c: Vertical(g5)
    c: Vertical(g7)
    c: Distance(g5,g7) = 165
    c: Distance(g4,g6) = 30
    c: Coincident(g4,g0)
    c: Distance(g8) = 22
    c: Coincident(g8,g4)
    c: PointOnObject(g8,g4)
    c: Distance(g9) = 117
    c: Coincident(g9,g8)
    c: PointOnObject(g9,g4)
    c: Distance(g10) = 15
    c: Coincident(g10,g8)
    c: Vertical(g10)
    c: Distance(g11) = 6
    c: Coincident(g11,g9)
    c: Vertical(g11)
    c: Distance(g12) = 18
    c: Coincident(g12,g11)
    c: Vertical(g12)
    c: Diameter(g13) = 3
    c: Coincident(g13,g10)
    c: Diameter(g14) = 3
    c: Coincident(g14,g11)
    c: Diameter(g15) = 3
    c: Coincident(g15,g12)
FEATURE [PartDesign::Hole] Hole001
  BaseFeature = -> Hole
  CustomThreadClearance = 0
  Depth = 25
  DepthType = 0
  Diameter = 3.6
  DrillForDepth = false
  DrillPoint = 1
  DrillPointAngle = 118
  HoleCutCountersinkAngle = 90
  HoleCutCustomValues = false
  HoleCutDepth = 0
  HoleCutDiameter = 6.1
  HoleCutType = 0
  ModelThread = false
  Profile = -> Sketch007
  Refine = true
  Suppressed = false
  Tapered = false
  TaperedAngle = 90
  ThreadClass = 0
  ThreadDepth = 25
  ThreadDepthType = 0
  ThreadDirection = 0
  ThreadFit = 2
  ThreadSize = 9
  ThreadType = 1
  Threaded = false
  UseCustomThreadClearance = false
FEATURE [PartDesign::Chamfer] Chamfer001
  Angle = 45
  Base = -> Hole001 [Edge125,Edge49]
  BaseFeature = -> Hole001
  ChamferType = 0
  FlipDirection = false
  Refine = true
  Size = 3
  Size2 = 1
  SupportTransform = false
  Suppressed = false
  UseAllEdges = false
FEATURE [PartDesign::Chamfer] Chamfer002
  Angle = 45
  Base = -> Chamfer001 [Edge45]
  BaseFeature = -> Chamfer001
  ChamferType = 0
  FlipDirection = false
  Refine = true
  Size = 7
  Size2 = 1
  SupportTransform = false
  Suppressed = false
  UseAllEdges = false
FEATURE [Sketcher::SketchObject] Sketch008
  ArcFitTolerance = 1e-06
  AttachmentSupport = -> [Chamfer002]
  FullyConstrained = true
  MakeInternals = false
  MapMode = 5
  Placement = pos=(0,0,4) rot=(0,0,1;0rad)
  sketch-geometry (10):
    g0: LineSegment [constr] StartX=0 StartY=0 StartZ=0 EndX=0 EndY=-37 EndZ=0
    g1: LineSegment [constr] StartX=0 StartY=-37 StartZ=0 EndX=30 EndY=-37 EndZ=0
    g2: LineSegment [constr] StartX=30 StartY=-37 StartZ=0 EndX=30 EndY=0 EndZ=0
    g3: LineSegment [constr] StartX=30 StartY=0 StartZ=0 EndX=0 EndY=0 EndZ=0
    g4: LineSegment [constr] StartX=30 StartY=-37 StartZ=0 EndX=114.5 EndY=-37 EndZ=0
    g5: LineSegment [constr] StartX=114.5 StartY=-37 StartZ=0 EndX=119.5 EndY=-37 EndZ=0
    g6: LineSegment StartX=119.5 StartY=-37 StartZ=0 EndX=109.5 EndY=-37 EndZ=0
    g7: LineSegment StartX=109.5 StartY=-37 StartZ=0 EndX=109.5 EndY=-47 EndZ=0
    g8: LineSegment StartX=109.5 StartY=-47 StartZ=0 EndX=119.5 EndY=-47 EndZ=0
    g9: LineSegment StartX=119.5 StartY=-47 StartZ=0 EndX=119.5 EndY=-37 EndZ=0
  constraints (28):
    c: Coincident(g0,g1)
    c: Coincident(g1,g2)
    c: Coincident(g2,g3)
    c: Coincident(g3,g0)
    c: Vertical(g0)
    c: Vertical(g2)
    c: Horizontal(g1)
    c: Horizontal(g3)
    c: Distance(g0,g2) = 30
    c: Distance(g1,g3) = 37
    c: Coincident(g0,g-1)
    c: Distance(g4) = 84.5
    c: Coincident(g4,g1)
    c: Horizontal(g4)
    c: Distance(g5) = 5
    c: Coincident(g5,g4)
    c: Horizontal(g5)
    c: Coincident(g6,g7)
    c: Coincident(g7,g8)
    c: Coincident(g8,g9)
    c: Coincident(g9,g6)
    c: Horizontal(g6)
    c: Horizontal(g8)
    c: Vertical(g7)
    c: Vertical(g9)
    c: Distance(g7,g9) = 10
    c: Distance(g6,g8) = 10
    c: Coincident(g6,g5)
FEATURE [PartDesign::Pad] Pad002
  BaseFeature = -> Chamfer002
  Direction = (0,0,1)
  Length = 4
  Length2 = 10
  Profile = -> Sketch008
  ReferenceAxis = -> Sketch008 [N_Axis]
  Refine = true
  Reversed = true
  Suppressed = false
  Type = 0
FEATURE [Sketcher::SketchObject] Sketch009
  ArcFitTolerance = 1e-06
  AttachmentSupport = -> [Pad002]
  FullyConstrained = true
  MakeInternals = false
  MapMode = 5
  Placement = pos=(0,0,0) rot=(1,0,0;3.14159rad)
  sketch-geometry (9):
    g0: LineSegment [constr] StartX=0 StartY=0 StartZ=0 EndX=109.5 EndY=0 EndZ=0
    g1: LineSegment [constr] StartX=109.5 StartY=0 StartZ=0 EndX=109.5 EndY=37 EndZ=0
    g2: LineSegment [constr] StartX=109.5 StartY=37 StartZ=0 EndX=0 EndY=37 EndZ=0
    g3: LineSegment [constr] StartX=0 StartY=37 StartZ=0 EndX=0 EndY=0 EndZ=0
    g4: LineSegment [constr] StartX=109.5 StartY=37 StartZ=0 EndX=109.5 EndY=43 EndZ=0
    g5: LineSegment StartX=109.5 StartY=43 StartZ=0 EndX=119.5 EndY=43 EndZ=0
    g6: LineSegment StartX=119.5 StartY=43 StartZ=0 EndX=119.5 EndY=47 EndZ=0
    g7: LineSegment StartX=119.5 StartY=47 StartZ=0 EndX=109.5 EndY=47 EndZ=0
    g8: LineSegment StartX=109.5 StartY=47 StartZ=0 EndX=109.5 EndY=43 EndZ=0
  constraints (25):
    c: Coincident(g0,g1)
    c: Coincident(g1,g2)
    c: Coincident(g2,g3)
    c: Coincident(g3,g0)
    c: Horizontal(g0)
    c: Horizontal(g2)
    c: Vertical(g1)
    c: Vertical(g3)
    c: Distance(g1,g3) = 109.5
    c: Distance(g0,g2) = 37
    c: Coincident(g0,g-1)
    c: Distance(g4) = 6
    c: Coincident(g4,g1)
    c: Vertical(g4)
    c: Coincident(g5,g6)
    c: Coincident(g6,g7)
    c: Coincident(g7,g8)
    c: Coincident(g8,g5)
    c: Horizontal(g5)
    c: Horizontal(g7)
    c: Vertical(g6)
    c: Vertical(g8)
    c: Distance(g6,g8) = 10
    c: Distance(g5,g7) = 4
    c: Coincident(g5,g4)
FEATURE [PartDesign::Pad] Pad003
  BaseFeature = -> Pad002
  Direction = (0,0,-1)
  Length = 30
  Length2 = 10
  Profile = -> Sketch009
  ReferenceAxis = -> Sketch009 [N_Axis]
  Refine = true
  Suppressed = false
  Type = 0
FEATURE [Sketcher::SketchObject] Sketch010
  ArcFitTolerance = 1e-06
  AttachmentSupport = -> [Pad003]
  FullyConstrained = true
  MakeInternals = false
  MapMode = 5
  Placement = pos=(0,-43,0) rot=(0,0.707107,0.707107;3.14159rad)
  sketch-geometry (8):
    g0: LineSegment [constr] StartX=0 StartY=0 StartZ=0 EndX=-109.5 EndY=0 EndZ=0
    g1: LineSegment [constr] StartX=-109.5 StartY=0 StartZ=0 EndX=-109.5 EndY=-30 EndZ=0
    g2: LineSegment [constr] StartX=-109.5 StartY=-30 StartZ=0 EndX=0 EndY=-30 EndZ=0
    g3: LineSegment [constr] StartX=0 StartY=-30 StartZ=0 EndX=0 EndY=0 EndZ=0
    g4: LineSegment StartX=-109.5 StartY=-30 StartZ=0 EndX=-109.5 EndY=-26 EndZ=0
    g5: LineSegment StartX=-109.5 StartY=-26 StartZ=0 EndX=-119.5 EndY=-26 EndZ=0
    g6: LineSegment StartX=-119.5 StartY=-26 StartZ=0 EndX=-119.5 EndY=-30 EndZ=0
    g7: LineSegment StartX=-119.5 StartY=-30 StartZ=0 EndX=-109.5 EndY=-30 EndZ=0
  constraints (22):
    c: Coincident(g0,g1)
    c: Coincident(g1,g2)
    c: Coincident(g2,g3)
    c: Coincident(g3,g0)
    c: Horizontal(g0)
    c: Horizontal(g2)
    c: Vertical(g1)
    c: Vertical(g3)
    c: Distance(g1,g3) = 109.5
    c: Distance(g0,g2) = 30
    c: Coincident(g0,g-1)
    c: Coincident(g4,g5)
    c: Coincident(g5,g6)
    c: Coincident(g6,g7)
    c: Coincident(g7,g4)
    c: Vertical(g4)
    c: Vertical(g6)
    c: Horizontal(g5)
    c: Horizontal(g7)
    c: Distance(g4,g6) = 10
    c: Distance(g5,g7) = 4
    c: Coincident(g4,g1)
FEATURE [PartDesign::Pad] Pad004
  BaseFeature = -> Pad003
  Direction = (0,1,-2e-16)
  Length = 4
  Length2 = 10
  Profile = -> Sketch010
  ReferenceAxis = -> Sketch010 [N_Axis]
  Refine = true
  Suppressed = false
  Type = 0
FEATURE [PartDesign::Chamfer] Chamfer003
  Angle = 45
  Base = -> Pad004 [Edge130,Edge152,Edge158,Edge155]
  BaseFeature = -> Pad004
  ChamferType = 0
  FlipDirection = false
  Refine = true
  Size = 3.99
  Size2 = 1
  SupportTransform = false
  Suppressed = false
  UseAllEdges = false
FEATURE [PartDesign::Body] Body  label="power-supply-bracket-body"
  AllowCompound = false
  Group = -> [Sketch,Pad,Sketch001,Pad001,Fillet,Sketch004,Sketch005,Chamfer,Sketch006,Hole,Sketch007,Hole001,Chamfer001,Chamfer002,Sketch008,Pad002,Sketch009,Pad003,Sketch010,Pad004,Chamfer003]
  Origin = -> Origin
  Tip = -> Chamfer003
FEATURE [App::Part] Part  label="power-supply-bracket-part"
  Group = -> [Body]
  Origin = -> Origin001
---- part smc100c-bracket.FCStd = doc fcstd_0991f6a71109 ----
FCSTD DOCUMENT  (FreeCAD 1.0R39319 (Git))
Label: smc100c-bracket
License: All rights reserved
objects: PartDesign::Chamfer×6, Sketcher::SketchObject×5, PartDesign::Pad×3, PartDesign::Pocket×1, PartDesign::Body×1, App::Part×1
note: 41 computed .brp shape members not serialized (recipe doc carries the construction recipe); baked Part::Feature solids carry a one-line shape summary decoded from their .brp

FEATURE [Sketcher::SketchObject] Sketch
  ArcFitTolerance = 1e-06
  AttachmentSupport = -> [XZ_Plane]
  FullyConstrained = true
  MakeInternals = false
  MapMode = 5
  Placement = pos=(0,0,0) rot=(1,0,0;1.5708rad)
  sketch-geometry (62):
    g0: LineSegment [constr] StartX=0 StartY=0 StartZ=0 EndX=0 EndY=-5 EndZ=0
    g1: LineSegment [constr] StartX=0 StartY=-5 StartZ=0 EndX=5 EndY=-5 EndZ=0
    g2: LineSegment [constr] StartX=5 StartY=-5 StartZ=0 EndX=5 EndY=0 EndZ=0
    g3: LineSegment [constr] StartX=5 StartY=0 StartZ=0 EndX=0 EndY=0 EndZ=0
    g4: LineSegment [constr] StartX=5 StartY=-5 StartZ=0 EndX=5 EndY=-153 EndZ=0
    g5: LineSegment [constr] StartX=5 StartY=-153 StartZ=0 EndX=174 EndY=-153 EndZ=0
    g6: LineSegment [constr] StartX=174 StartY=-153 StartZ=0 EndX=174 EndY=-5 EndZ=0
    g7: LineSegment [constr] StartX=174 StartY=-5 StartZ=0 EndX=5 EndY=-5 EndZ=0
    g8: Circle CenterX=89.5 CenterY=-79 CenterZ=0 NormalX=0 NormalY=0 NormalZ=1 AngleXU=0 Radius=2.6
    g9: LineSegment StartX=0 StartY=0 StartZ=0 EndX=0 EndY=-158 EndZ=0
    g10: LineSegment StartX=0 StartY=-158 StartZ=0 EndX=179 EndY=-158 EndZ=0
    g11: LineSegment StartX=179 StartY=-158 StartZ=0 EndX=179 EndY=0 EndZ=0
    g12: LineSegment StartX=179 StartY=0 StartZ=0 EndX=0 EndY=0 EndZ=0
    g13: LineSegment [constr] StartX=0 StartY=0 StartZ=0 EndX=0 EndY=-16 EndZ=0
    g14: LineSegment [constr] StartX=0 StartY=-16 StartZ=0 EndX=16 EndY=-16 EndZ=0
    g15: LineSegment [constr] StartX=16 StartY=-16 StartZ=0 EndX=16 EndY=0 EndZ=0
    g16: LineSegment [constr] StartX=16 StartY=0 StartZ=0 EndX=0 EndY=0 EndZ=0
    g17: LineSegment [constr] StartX=0 StartY=-158 StartZ=0 EndX=16 EndY=-158 EndZ=0
    g18: LineSegment [constr] StartX=16 StartY=-158 StartZ=0 EndX=16 EndY=-142 EndZ=0
    g19: LineSegment [constr] StartX=16 StartY=-142 StartZ=0 EndX=0 EndY=-142 EndZ=0
    g20: LineSegment [constr] StartX=0 StartY=-142 StartZ=0 EndX=0 EndY=-158 EndZ=0
    g21: LineSegment [constr] StartX=179 StartY=-158 StartZ=0 EndX=179 EndY=-142 EndZ=0
    g22: LineSegment [constr] StartX=179 StartY=-142 StartZ=0 EndX=163 EndY=-142 EndZ=0
    g23: LineSegment [constr] StartX=163 StartY=-142 StartZ=0 EndX=163 EndY=-158 EndZ=0
    g24: LineSegment [constr] StartX=163 StartY=-158 StartZ=0 EndX=179 EndY=-158 EndZ=0
    g25: LineSegment [constr] StartX=179 StartY=0 StartZ=0 EndX=163 EndY=0 EndZ=0
    g26: LineSegment [constr] StartX=163 StartY=0 StartZ=0 EndX=163 EndY=-16 EndZ=0
    g27: LineSegment [constr] StartX=163 StartY=-16 StartZ=0 EndX=179 EndY=-16 EndZ=0
    g28: LineSegment [constr] StartX=179 StartY=-16 StartZ=0 EndX=179 EndY=0 EndZ=0
    g29: LineSegment [constr] StartX=163 StartY=-16 StartZ=0 EndX=151.7 EndY=-16 EndZ=0
    g30: LineSegment [constr] StartX=151.7 StartY=-16 StartZ=0 EndX=151.7 EndY=-27.3 EndZ=0
    g31: LineSegment [constr] StartX=151.7 StartY=-27.3 StartZ=0 EndX=163 EndY=-27.3 EndZ=0
    g32: LineSegment [constr] StartX=163 StartY=-27.3 StartZ=0 EndX=163 EndY=-16 EndZ=0
    g33: LineSegment [constr] StartX=163 StartY=-142 StartZ=0 EndX=163 EndY=-130.7 EndZ=0
    g34: LineSegment [constr] StartX=163 StartY=-130.7 StartZ=0 EndX=151.7 EndY=-130.7 EndZ=0
    g35: LineSegment [constr] StartX=151.7 StartY=-130.7 StartZ=0 EndX=151.7 EndY=-142 EndZ=0
    g36: LineSegment [constr] StartX=151.7 StartY=-142 StartZ=0 EndX=163 EndY=-142 EndZ=0
    g37: LineSegment [constr] StartX=16 StartY=-142 StartZ=0 EndX=27.3 EndY=-142 EndZ=0
    g38: LineSegment [constr] StartX=27.3 StartY=-142 StartZ=0 EndX=27.3 EndY=-130.7 EndZ=0
    g39: LineSegment [constr] StartX=27.3 StartY=-130.7 StartZ=0 EndX=16 EndY=-130.7 EndZ=0
    g40: LineSegment [constr] StartX=16 StartY=-130.7 StartZ=0 EndX=16 EndY=-142 EndZ=0
    g41: LineSegment [constr] StartX=16 StartY=-16 StartZ=0 EndX=16 EndY=-27.3 EndZ=0
    g42: LineSegment [constr] StartX=16 StartY=-27.3 StartZ=0 EndX=27.3 EndY=-27.3 EndZ=0
    g43: LineSegment [constr] StartX=27.3 StartY=-27.3 StartZ=0 EndX=27.3 EndY=-16 EndZ=0
    g44: LineSegment [constr] StartX=27.3 StartY=-16 StartZ=0 EndX=16 EndY=-16 EndZ=0
    g45: LineSegment StartX=16 StartY=-27.3 StartZ=0 EndX=16 EndY=-130.7 EndZ=0
    g46: LineSegment StartX=27.3 StartY=-142 StartZ=0 EndX=151.7 EndY=-142 EndZ=0
    g47: LineSegment StartX=163 StartY=-130.7 StartZ=0 EndX=163 EndY=-27.3 EndZ=0
    g48: LineSegment StartX=151.7 StartY=-16 StartZ=0 EndX=27.3 EndY=-16 EndZ=0
    g49: LineSegment [constr] StartX=78.185 StartY=-90.315 StartZ=0 EndX=100.815 EndY=-90.315 EndZ=0
    g50: LineSegment [constr] StartX=100.815 StartY=-90.315 StartZ=0 EndX=100.815 EndY=-67.685 EndZ=0
    g51: LineSegment [constr] StartX=100.815 StartY=-67.685 StartZ=0 EndX=78.185 EndY=-67.685 EndZ=0
    g52: LineSegment [constr] StartX=78.185 StartY=-67.685 StartZ=0 EndX=78.185 EndY=-90.315 EndZ=0
    g53: GeomPoint [constr] X=89.5 Y=-79 Z=0
    g54: LineSegment StartX=27.3 StartY=-142 StartZ=0 EndX=89.5 EndY=-90.315 EndZ=0
    g55: LineSegment StartX=89.5 StartY=-90.315 StartZ=0 EndX=151.7 EndY=-142 EndZ=0
    g56: LineSegment StartX=163 StartY=-130.7 StartZ=0 EndX=100.815 EndY=-79 EndZ=0
    g57: LineSegment StartX=100.815 StartY=-79 StartZ=0 EndX=163 EndY=-27.3 EndZ=0
    g58: LineSegment StartX=151.7 StartY=-16 StartZ=0 EndX=89.5 EndY=-67.685 EndZ=0
    g59: LineSegment StartX=89.5 StartY=-67.685 StartZ=0 EndX=27.3 EndY=-16 EndZ=0
    g60: LineSegment StartX=16 StartY=-27.3 StartZ=0 EndX=78.185 EndY=-79 EndZ=0
    g61: LineSegment StartX=78.185 StartY=-79 StartZ=0 EndX=16 EndY=-130.7 EndZ=0
  constraints (159):
    c: Coincident(g0,g1)
    c: Coincident(g1,g2)
    c: Coincident(g2,g3)
    c: Coincident(g3,g0)
    c: Vertical(g0)
    c: Vertical(g2)
    c: Horizontal(g1)
    c: Horizontal(g3)
    c: Distance(g0,g2) = 5
    c: Distance(g1,g3) = 5
    c: Coincident(g0,g-1)
    c: Coincident(g4,g5)
    c: Coincident(g5,g6)
    c: Coincident(g6,g7)
    c: Coincident(g7,g4)
    c: Vertical(g4)
    c: Vertical(g6)
    c: Horizontal(g5)
    c: Horizontal(g7)
    c: Distance(g4,g6) = 169
    c: Distance(g5,g7) = 148
    c: Coincident(g4,g1)
    c: Diameter(g8) = 5.2
    c: Symmetric(g6,g4,g8)
    c: Distance(g9) = 158
    c: Coincident(g9,g0)
    c: PointOnObject(g9,g-2)
    c: Distance(g10) = 179
    c: Coincident(g10,g9)
    c: Horizontal(g10)
    c: Coincident(g11,g10)
    c: PointOnObject(g11,g-1)
    c: Vertical(g11)
    c: Coincident(g12,g11)
    c: Coincident(g12,g0)
    c: Coincident(g13,g14)
    c: Coincident(g14,g15)
    c: Coincident(g15,g16)
    c: Coincident(g16,g13)
    c: Vertical(g13)
    c: Vertical(g15)
    c: Horizontal(g14)
    c: Horizontal(g16)
    c: Distance(g13,g15) = 16
    c: Distance(g14,g16) = 16
    c: Coincident(g13,g0)
    c: Coincident(g17,g18)
    c: Coincident(g18,g19)
    c: Coincident(g19,g20)
    c: Coincident(g20,g17)
    c: Horizontal(g17)
    c: Horizontal(g19)
    c: Vertical(g18)
    c: Vertical(g20)
    c: Distance(g18,g20) = 16
    c: Distance(g17,g19) = 16
    c: Coincident(g17,g9)
    c: Coincident(g21,g22)
    c: Coincident(g22,g23)
    c: Coincident(g23,g24)
    c: Coincident(g24,g21)
    c: Vertical(g21)
    c: Vertical(g23)
    c: Horizontal(g22)
    c: Horizontal(g24)
    c: Distance(g21,g23) = 16
    c: Distance(g22,g24) = 16
    c: Coincident(g21,g10)
    c: Coincident(g25,g26)
    c: Coincident(g26,g27)
    c: Coincident(g27,g28)
    c: Coincident(g28,g25)
    c: Horizontal(g25)
    c: Horizontal(g27)
    c: Vertical(g26)
    c: Vertical(g28)
    c: Distance(g26,g28) = 16
    c: Distance(g25,g27) = 16
    c: Coincident(g25,g11)
    c: Coincident(g29,g30)
    c: Coincident(g30,g31)
    c: Coincident(g31,g32)
    c: Coincident(g32,g29)
    c: Horizontal(g29)
    c: Horizontal(g31)
    c: Vertical(g30)
    c: Vertical(g32)
    c: Distance(g30,g32) = 11.3
    c: Distance(g29,g31) = 11.3
    c: Coincident(g29,g26)
    c: Coincident(g33,g34)
    c: Coincident(g34,g35)
    c: Coincident(g35,g36)
    c: Coincident(g36,g33)
    c: Vertical(g33)
    c: Vertical(g35)
    c: Horizontal(g34)
    c: Horizontal(g36)
    c: Distance(g33,g35) = 11.3
    c: Distance(g34,g36) = 11.3
    c: Coincident(g33,g22)
    c: Coincident(g37,g38)
    c: Coincident(g38,g39)
    c: Coincident(g39,g40)
    c: Coincident(g40,g37)
    c: Horizontal(g37)
    c: Horizontal(g39)
    c: Vertical(g38)
    c: Vertical(g40)
    c: Distance(g38,g40) = 11.3
    c: Distance(g37,g39) = 11.3
    c: Coincident(g37,g18)
    c: Coincident(g41,g42)
    c: Coincident(g42,g43)
    c: Coincident(g43,g44)
    c: Coincident(g44,g41)
    c: Vertical(g41)
    c: Vertical(g43)
    c: Horizontal(g42)
    c: Horizontal(g44)
    c: Distance(g41,g43) = 11.3
    c: Distance(g42,g44) = 11.3
    c: Coincident(g41,g14)
    c: Coincident(g45,g41)
    c: Coincident(g45,g39)
    c: Coincident(g46,g37)
    c: Coincident(g46,g35)
    c: Coincident(g47,g33)
    c: Coincident(g47,g31)
    c: Coincident(g48,g29)
    c: Coincident(g48,g43)
    c: Coincident(g49,g50)
    c: Coincident(g50,g51)
    c: Coincident(g51,g52)
    c: Coincident(g52,g49)
    c: Horizontal(g49)
    c: Horizontal(g51)
    c: Vertical(g50)
    c: Vertical(g52)
    c: Symmetric(g51,g49,g53)
    c: Distance(g50,g52) = 22.63
    c: Distance(g49,g51) = 22.63
    c: Coincident(g53,g8)
    c: Coincident(g54,g37)
    c: Symmetric(g49,g49,g54)
    c: Coincident(g55,g54)
    c: Coincident(g55,g35)
    c: Coincident(g56,g33)
    c: Symmetric(g50,g50,g56)
    c: Coincident(g57,g56)
    c: Coincident(g57,g31)
    c: Coincident(g58,g29)
    c: Symmetric(g51,g51,g58)
    c: Coincident(g59,g58)
    c: Coincident(g59,g43)
    c: Coincident(g60,g41)
    c: Symmetric(g52,g52,g60)
    c: Coincident(g61,g60)
    c: Coincident(g61,g39)
FEATURE [PartDesign::Pad] Pad
  Direction = (0,-1,2e-16)
  Length = 6
  Length2 = 10
  Placement = pos=(0,0,0) rot=(1,0,0;1.5708rad)
  Profile = -> Sketch
  ReferenceAxis = -> Sketch [N_Axis]
  Refine = true
  Reversed = true
  Suppressed = false
  Type = 0
FEATURE [Sketcher::SketchObject] Sketch001
  ArcFitTolerance = 1e-06
  AttachmentSupport = -> [Pad]
  FullyConstrained = true
  MakeInternals = false
  MapMode = 5
  Placement = pos=(179,0,0) rot=(0.707107,0,0.707107;3.14159rad)
  sketch-geometry (4):
    g0: LineSegment StartX=0 StartY=0 StartZ=0 EndX=-5 EndY=0 EndZ=0
    g1: LineSegment StartX=-5 StartY=0 StartZ=0 EndX=-5 EndY=-30 EndZ=0
    g2: LineSegment StartX=-5 StartY=-30 StartZ=0 EndX=0 EndY=-30 EndZ=0
    g3: LineSegment StartX=0 StartY=-30 StartZ=0 EndX=0 EndY=0 EndZ=0
  constraints (11):
    c: Coincident(g0,g1)
    c: Coincident(g1,g2)
    c: Coincident(g2,g3)
    c: Coincident(g3,g0)
    c: Horizontal(g0)
    c: Horizontal(g2)
    c: Vertical(g1)
    c: Vertical(g3)
    c: Distance(g1,g3) = 5
    c: Distance(g0,g2) = 30
    c: Coincident(g0,g-1)
FEATURE [PartDesign::Pad] Pad001
  BaseFeature = -> Pad
  Direction = (1,0,-2e-16)
  Length = 30
  Length2 = 10
  Placement = pos=(0,0,0) rot=(1,0,0;1.5708rad)
  Profile = -> Sketch001
  ReferenceAxis = -> Sketch001 [N_Axis]
  Refine = true
  Suppressed = false
  Type = 0
FEATURE [Sketcher::SketchObject] Sketch002
  ArcFitTolerance = 1e-06
  AttachmentSupport = -> [Pad001]
  FullyConstrained = true
  MakeInternals = false
  MapMode = 5
  Placement = pos=(0,6,0) rot=(-1,0,0;1.5708rad)
  sketch-geometry (5):
    g0: LineSegment [constr] StartX=0 StartY=0 StartZ=0 EndX=174 EndY=0 EndZ=0
    g1: LineSegment StartX=174 StartY=0 StartZ=0 EndX=179 EndY=0 EndZ=0
    g2: LineSegment StartX=179 StartY=0 StartZ=0 EndX=179 EndY=35 EndZ=0
    g3: LineSegment StartX=179 StartY=35 StartZ=0 EndX=174 EndY=35 EndZ=0
    g4: LineSegment StartX=174 StartY=35 StartZ=0 EndX=174 EndY=0 EndZ=0
  constraints (14):
    c: Distance(g0) = 174
    c: Coincident(g0,g-1)
    c: Horizontal(g0)
    c: Coincident(g1,g2)
    c: Coincident(g2,g3)
    c: Coincident(g3,g4)
    c: Coincident(g4,g1)
    c: Horizontal(g1)
    c: Horizontal(g3)
    c: Vertical(g2)
    c: Vertical(g4)
    c: Distance(g2,g4) = 5
    c: Distance(g1,g3) = 35
    c: Coincident(g1,g0)
FEATURE [PartDesign::Pad] Pad002
  BaseFeature = -> Pad001
  Direction = (0,1,2e-16)
  Length = 24
  Length2 = 10
  Placement = pos=(0,0,0) rot=(1,0,0;1.5708rad)
  Profile = -> Sketch002
  ReferenceAxis = -> Sketch002 [N_Axis]
  Refine = true
  Suppressed = false
  Type = 0
FEATURE [Sketcher::SketchObject] Sketch003
  ArcFitTolerance = 1e-06
  AttachmentSupport = -> [Pad002]
  FullyConstrained = true
  MakeInternals = false
  MapMode = 5
  Placement = pos=(0,0,-7e-16) rot=(0,0,1;3.14159rad)
  sketch-geometry (5):
    g0: LineSegment [constr] StartX=0 StartY=0 StartZ=0 EndX=-194 EndY=0 EndZ=0
    g1: LineSegment [constr] StartX=-194 StartY=0 StartZ=0 EndX=-194 EndY=-15 EndZ=0
    g2: LineSegment [constr] StartX=-194 StartY=-15 StartZ=0 EndX=0 EndY=-15 EndZ=0
    g3: LineSegment [constr] StartX=0 StartY=-15 StartZ=0 EndX=0 EndY=0 EndZ=0
    g4: Circle CenterX=-194 CenterY=-15 CenterZ=0 NormalX=0 NormalY=0 NormalZ=1 AngleXU=0 Radius=2.6
  constraints (13):
    c: Coincident(g0,g1)
    c: Coincident(g1,g2)
    c: Coincident(g2,g3)
    c: Coincident(g3,g0)
    c: Horizontal(g0)
    c: Horizontal(g2)
    c: Vertical(g1)
    c: Vertical(g3)
    c: Distance(g1,g3) = 194
    c: Distance(g0,g2) = 15
    c: Coincident(g0,g-1)
    c: Diameter(g4) = 5.2
    c: Coincident(g4,g1)
FEATURE [PartDesign::Pocket] Pocket
  BaseFeature = -> Pad002
  Direction = (0,0,-1)
  Length = 7
  Length2 = 5
  Placement = pos=(0,0,0) rot=(1,0,0;1.5708rad)
  Profile = -> Sketch003
  ReferenceAxis = -> Sketch003 [N_Axis]
  Refine = true
  Suppressed = false
  Type = 0
FEATURE [PartDesign::Chamfer] Chamfer
  Angle = 45
  Base = -> Pocket [Edge47,Edge16]
  BaseFeature = -> Pocket
  ChamferType = 0
  FlipDirection = false
  Placement = pos=(0,0,0) rot=(1,0,0;1.5708rad)
  Refine = true
  Size = 5
  Size2 = 1
  SupportTransform = false
  Suppressed = false
  UseAllEdges = false
FEATURE [PartDesign::Chamfer] Chamfer001
  Angle = 45
  Base = -> Chamfer [Edge57]
  BaseFeature = -> Chamfer
  ChamferType = 0
  FlipDirection = false
  Placement = pos=(0,0,0) rot=(1,0,0;1.5708rad)
  Refine = true
  Size = 5
  Size2 = 1
  SupportTransform = false
  Suppressed = false
  UseAllEdges = false
FEATURE [PartDesign::Chamfer] Chamfer002
  Angle = 45
  Base = -> Chamfer001 [Edge8]
  BaseFeature = -> Chamfer001
  ChamferType = 0
  FlipDirection = false
  Placement = pos=(0,0,0) rot=(1,0,0;1.5708rad)
  Refine = true
  Size = 5
  Size2 = 1
  SupportTransform = false
  Suppressed = false
  UseAllEdges = false
FEATURE [PartDesign::Chamfer] Chamfer003
  Angle = 45
  Base = -> Chamfer002 [Edge42]
  BaseFeature = -> Chamfer002
  ChamferType = 0
  FlipDirection = false
  Placement = pos=(0,0,0) rot=(1,0,0;1.5708rad)
  Refine = true
  Size = 10
  Size2 = 1
  SupportTransform = false
  Suppressed = false
  UseAllEdges = false
FEATURE [PartDesign::Chamfer] Chamfer004
  Angle = 45
  Base = -> Chamfer003 [Edge34]
  BaseFeature = -> Chamfer003
  ChamferType = 0
  FlipDirection = false
  Placement = pos=(0,0,0) rot=(1,0,0;1.5708rad)
  Refine = true
  Size = 10
  Size2 = 1
  SupportTransform = false
  Suppressed = false
  UseAllEdges = false
FEATURE [PartDesign::Chamfer] Chamfer005
  Angle = 45
  Base = -> Chamfer004 [Edge31]
  BaseFeature = -> Chamfer004
  ChamferType = 0
  FlipDirection = false
  Placement = pos=(0,0,0) rot=(1,0,0;1.5708rad)
  Refine = true
  Size = 10
  Size2 = 1
  SupportTransform = false
  Suppressed = false
  UseAllEdges = false
FEATURE [Sketcher::SketchObject] Sketch004
  ArcFitTolerance = 1e-06
  AttachmentSupport = -> [Chamfer005]
  FullyConstrained = true
  MakeInternals = false
  MapMode = 5
  Placement = pos=(0,6,0) rot=(-1,0,0;1.5708rad)
FEATURE [PartDesign::Body] Body  label="smc100c-bracket-body"
  AllowCompound = false
  Group = -> [Sketch,Pad,Sketch001,Pad001,Sketch002,Pad002,Sketch003,Pocket,Chamfer,Chamfer001,Chamfer002,Chamfer003,Chamfer004,Chamfer005,Sketch004]
  Origin = -> Origin
  Tip = -> Chamfer005
FEATURE [App::Part] Part  label="smc100c-bracket-part"
  Group = -> [Body]
  Origin = -> Origin001
